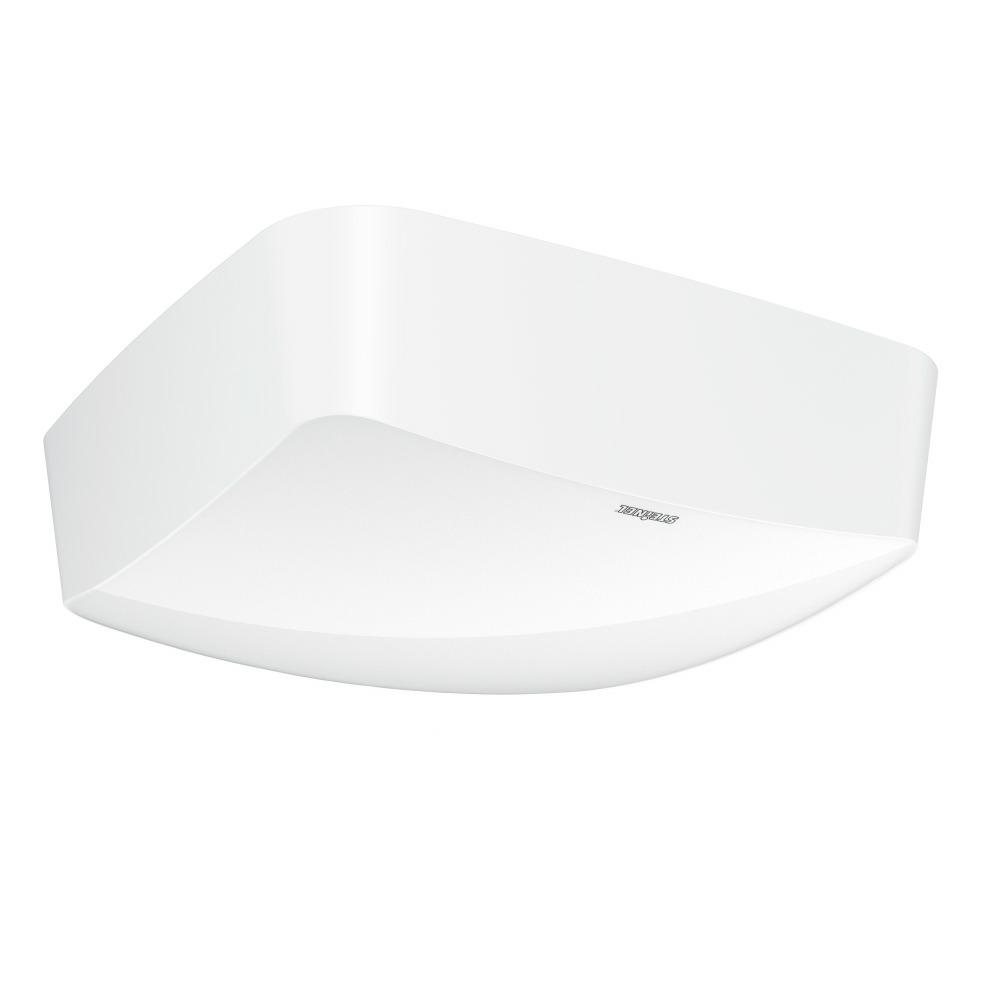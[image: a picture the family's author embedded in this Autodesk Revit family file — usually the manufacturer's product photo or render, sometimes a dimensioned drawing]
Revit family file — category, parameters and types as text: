
# Revit family: truepresence_057930
name_source: partatom
category: Electrical Fixtures
revit_build: Autodesk Revit 2016 (Build: 20151007_0715(x64)
units: mm (PartAtom-declared; Revit-internal decimal feet)

## family parameters
Cut with Voids When Loaded = No
Host = Face
Maintain Annotation Orientation = No
Part Type = Normal
Room Calculation Point = No
Round Connector Dimension = Use Diameter
Shared = No

## types (1)
- True Presence
    Apparent Load = 0 VA
    Default Elevation = 1800 mm
    Description = Type: Presence detector; Dimensions (L x W x H): 45 x 123 x 123 mm; Mains power supply: 220 – 240 V / 50 – 60 Hz; Power consumption: 1 W; Sensor Technology: High frequency; Application, place: Indoors; Application, room: classroom, lecture hall, one-person office, open-plan office, high-bay warehouse, production facilities, conference room / meeting room, hotel room, care room, duty room, recreation room, dining hall / staff restaurant, changing room, kitchenette, sports hall, reception / lobby, WC / washroom, warehouse, Indoors; Installation site: ceiling; Installation: Surface wiring; HF-system: 7,2 GHz; Electronic scalability: Yes; Mechanical scalability: No; Mounting height: 2 – 12 m; Optimum mounting height: 2,8 m; Detection angle: 360 °; Angle of aperture: 360 °; Sneak-by guard: Yes; Capability of masking out individual segments: No; Reach, radial: Ø 15 m (177 m²); Reach, tangential: Ø 15 m (177 m²); Reach, presence: Ø 15 m (177 m²); True Presence reach: Ø 9 m (64 m²); Twilight setting TEACH: Yes; Twilight setting: 2 – 1000 lx; Time setting: 30 sec – 30 min; Switching output 1, resistive: 2000 W; Switching output 1, number of LEDs / fluorescent lamps: 8 pcs.; Switching output 1, floating: No; Switching output 2, resistive: 230 W; Switching output 2, floating: Yes; Constant-lighting control: No; Basic light level function: No; Functions: Group parameterisation, Semi-/fully automatic, Lighting scenario, Manual ON / ON-OFF, Neighbouring-group function, Normal / test mode; Settings via: Bluetooth; With remote control: No; Interconnection: Yes; IP-rating: IP54; Material: Plastic; Ambient temperature: -20 – 50 °C; Colour: white; Colour, RAL: 9003; Manufacturer's Warranty: 5 years; Version: COM2 - Surface wiring; PU1, EAN: 4007841057930
    Height = 0 mm  [stored 0 ft]
    Length = 200 mm  [stored 0.656168 ft]
    Manufacturer = Steinel
    ModVariant = No
    Model = 057930
    Number of Poles = 1
    OnlyDefault = No
    Power Factor = 1
    Product Name = True Presence
    Product group = Sensor-switched outdoor light
    ProductGroupID = 3
    RLX_Detail_Level = 1
    RLX_LegendID = 2.1
    RlxData = Q
eAHsfQe8HUd99ZVluchyE3Jvz71fby/Se0/v2pJ7ky33Jhe5gFxw7wgXsKm2Y4xDL6YEQglx
CGA/yR+hGpKQ0PIFEgjhw0ACIeAkOBR958zOmIux8JvH1fPc+45+Om/+87///+zs7rl7dvbO
7s5orVnTwr81vzYFTfNvI2egXIN/rrrrsc5qcpjn0GqtXAisRoT5YxLXrPnBzHmtQy6/9LxL
Ljv36ksuv+zoay6FdcmVyzfaYH2mbrO0dWXrmtby1lDreFjLW1cBl7XON559WlErb5WtupXC
Gmrt2xpD67HtQ3cnZ8K3Zs2/z5zTOvqSiy6+evGll1x99fIrW0MzuIzZV7bObV3QOue3WmNL
ybO2tB5a+sHM9VvHLL/q4hmbmRbMctNniZ7RWt96f4KVn8g/r7ifHvfq93CD/p5/TXtbmohv
7tNqLYb1MuDyubfvfvG9l47vefu3Fvzru3YYd/Zff/GLj2afnTG+7U7rL9hn6wXj9x910fjf
/cWXF/z6vpPGia33fXjB9p/82qPE/e99eP7dd9013BU/4uLR5ohrc/bX37nHDgf907sOXrZ8
T+QNu1y0N+LaROwIO8n+0GafaKPtEfaJ/UHbI+wT+0M/l93lH6Hf5o4w1y5rmP20yxph/+16
mXi2zXa71tHE0H/Lt749XOz6mfnsL9ty6+v8XL7LRZtcd9OOXXfTB2znd7JPXdvZ2Igdd+tC
m8tjH9D2o7S5XNpcBm3G0GaMzXXrO87l2e023rUN6R/vWu449sMwP0d/jG37aexT1swfmXPS
RcZ2+4Xx8I3gM+N3+4V+2mzL2WyrK97YbpvTb9s3frtcY9v+OD956HIN32zuuOsby67+mHW0
fTDbwdmub+QX+0G/zTU22+C60f+TZW95FBjush+1tvmsyzYxbHsGsJ4FbR5hWGfJ7zwxC3Ax
tDewdZbuH+0NbYUlj1obA7MB5hC0GcdyE2uzTps5c4BNgc0saG9ubZaMI5jvYmhvYess2QZB
m0cL2iznAuzPCwDmELQZx3KetVmnzZytgK2BbSxob2ttlttZ0N7e2iy5HII22yZos12C9g7W
ZrmjBe2dLGjvbEGby2ad5S4WtF0fGcN+ELS5jCFgV8DtR9q72TpLt19o727rLF3/abt1pO22
A+09bJ3lnha097KgvbcFbS6bdZY4fBvQHgJYMob9IGhzGTMA/tvXgvZ+FrTJMdZZ7m9B+wAL
2uQV6ywPtKBNHrHOktyizbJtQZv8Y53lQbYkn2gTtCML2uQY6yxjC9qJBW3yinWWqQVt8oJ1
luQDbZaZBW1yg3WWuS3JCdoE7cKCNnnCOssSGALWByoL2jOtzbK2oM1tzzpLbn/mzAeGLGjv
Y0F7AcB9z308bEGbB1eCNuNps2Q8uUtOjVrQJpdYZ7nQgjbbZp0l22fMGMA2CNpcT4I215fr
zrJjQXvM2izdctmui6HN9llnyf7SZnmwBW32n3WWjp+03Tak7bYzbW4jxpGvrh3ah9g6S9cH
2otsnaXbp7S5nwnajhu0HZdoO77Rdjyk7bhKm8tgnaXjM21+j1hn6b4LtPn9IGjz+8S+02bO
oUD3v3/7s00+8bmfl6se+upNqxdd+z8Ldt56ZNUOr79p9VMfeenw3J0OW7Vq3k2r/+eQOeNv
uuKX4y/9f7es/tQNOz3y8K/+a/zUPW9dfdnNxz6y+j+b3GTuWz7xk8tXrJq71Q2rb375Lz9x
1ufHxhf+5UtWZ2OnDx95zNxVXzjtltUPrL7/0b964lDT5q9+XnKXtrjcf5g7Mjr3odYwl3vk
dw8d/fsnXjfM5R5/wi9GHp43zyz32Nn/zV3Z4nJ/9bNydNt793+EuX91xQrTDpf7kZ+OmRgu
98QT544m+588zOXaNh81bba2XfDRs84Z/eBXb1j9YGfm8JP37Tc6/MKbV8/b9ouPXvqmjUbf
8/ZbVi8ptljwpQ9/e2T+1beu/t77Tl3w3evHRtjm1z7ywCPpm+8c+dBVL1l97PH/teCcGUOj
e/7fm1f/6sh3P9L+s6adt879+Px3XL5ilP35m932qS/+dOO/5exzVj152foLuNwf3rPfqlP/
ZdYwl/v3P91o1WNbjD/K5X7+4W+Pjzzyg/lc7ifHxsZ/+L3bFnC5qw6/c/zRj33lES73a7OG
Vv38nB8s4HL3/cB+q9I5H32E7YxfsWLVseufWnO5p356v1Wf3+29Nf1/fN/+j3x2zUtWc9vd
uMfi0TX5Tcb+5KcPG+X2oP8f680Wxt9YauwP3bR04Xmf28zYm/7sxoUfvvDIVYxB7ELkGLtl
hlX0YoST37SQ7dK2McZGewvZLv1obyHbpY32RtkubdsHY7Pu2mVfkLuaHvYFucZmX5BrbPbF
9Z+l6xvXD/1x/TSxbIftsU+02R77RJvtsU+0bTvGtu2bGLbH9WTMb/6tXDgDlfWAmcD6wCyA
vg0A6hY1jb6NgdnAJgC1hxrFc6LNAfq2AKgr1Bz6XgBQW3is3BrgsZbnCtsB2wM7ADsC/Hyn
Z8HO8BG7AEPArsBuwO7AHoA7RvNzHuufCacV7ljpSncc4TGFcMcZHnt4HHLHLFfyeMbjmzve
uWMgj4nueM/jvAOPwe6Y7HSKPnds547pBnfImEUHJY/V9PE4x+Pm4ucJ52G5nwfceOXdb/yU
OS498Ys/GZn95q8Pt0/+ysjhr/jc/Hn3/svI6KzHFtx105+OrN5/vZGHjtjXfP6l/3vEMD/f
COMENGPaYVurEMO4CDnMc5+x5HhhI7S93v4bjnz2zSeMskTOKP1LWytGv4w2R++9aJR5jHvg
3x8cGcMy2Bfms49s/2705foNjhllyfit0Ee2x3gul/UlF84cXXj5D0eu/qNtTfnovU+N0M/6
Ja0PjTx04jYmf83oIaa+2YHJKPvPOvO+8LNlpnz51qfB/6OR5vMfjbzukE1M/d4//8kI+8uS
68H22e9sy62b9cIy6OdyuD3oZ/8uhp8ltyf7z+3LfnGZ9LM9V3K9uWyuN0v2jyW3F33H3thc
E2DJOv2MMdsZNv3cP6y/7ZQjTcn9dvEHv7yA24l+lqfWDy9gP1hnybpZNuKuOvQrxs/tzM9Z
8nNuH7bz439bZvzcTlweS8Zxe7HOknVuN9ZZss79w3xuN7bHkv72ZTPN525d3bpH57xlJAbY
n1uv/uHILcDVsOm//IKdjX98/mfn0/9erOtl8NHPknncDtx23A7MX4lY5rNkPP3MJ894fFzP
gjaPnay7Y6g7jroYHj95PGWdpfvnjrGsu2OtO84yh+Axl3Hu2Eub4DGXOc88FrvjMI/B7njM
WObzeE3Q5vGZNku2QbhjNm137GZ/ePxmDkGbcd3Hc9Z5TGeOO667YzqP8TyOs+6O5zxm0x4C
aLPc1YI22yZoUzMI2rtZmyV1gKBNPSBo72lBm8tmneVeFrRdHxnDfhC0hwDqCLXD6QXt/QDu
0/0B7pMDAPqoHbRZsv/cVk5HuF70c72pJfRTS1jv1hPaTlNoU1cI2lw2bZbUGoK26yNj2A+C
NpdHHerWINokLUGbB1zaLIctaI9Y0B61NktqEUF7DOgABwOHWJvlIgvaXD7rLKmD67o/i7GM
Q4HDANosD7egfYS1WR5p60dZm3XaR1vQPsbaLI8FjgOOB5YAvuvOnBMAtkHQZrsEbbbPfk22
P77rPpH+nIj+LAVOsqB9srVZuvOiU6yPcbTJYdosyVnaLE+1oE3+ss5yhgXt0yxo83tG0D4d
YBz/uXZon2HrLLkcgvaZ1mbJ9SBon2VB+2wL2ttb0D7HgvZWFrR5LCRocxm0WW5qQXsja7Nc
ZkF7Ewva5wL8R5s5/OfWjd/LFsYjrK9nbPfZSn71nvbx2OPiZsJiPLc9fcxzvqaNlQtZ57Zk
ndvIxTkfP6ePdbbNOo8lLs75+Dl9rFN7WOexzsU5n+sfP6HPxTOO9Q2tn9uFPv51Ppb0seQ2
YsljkotzPh676OPyZwP0zwPo4/Kcz/WPPtqMOwBgHPvCONcGfayzXyypnS7O+Vyf2S/ahFkB
5JIT5APLRQBzWd8McJ/RR9v5toTt4rg8xh9MF+IY43y06ePy6GN9DHA+1l08fey/q/NcwPlo
E+Q2fYxxPtcX9o8+1ucCjOuub2N9jHMx1H7GddePsD7GsR3GHGp93Oasc59RC13/nM/1j8ul
j/WtAca5GNZ3tj7GsS36XP/YF/pYPwpgrmtnW9T2tD6XQx/HpS6OefQtA+hjnIvZy/pcDPN4
HGGci2F9B+tjnItpWx/jXMze1udimLej9XFbMY51t63oYyx9BwJcLrcL4xjjtgvXnz7WdwEY
55bJulsu47hM+oYAxrk+sL4rXfAxjsscAo4GXByXyZjd6EKc6yt9x1of22M/GLO79bm+0ne8
9XE7M5YxbjvTx1z69gC4DPrYX9bdvnTrSR+1lXHc54xjzIUAfdz2XAbbd9tgCDb7uw+QA4xb
H3+db98u3xBsxi21PrfujCmsj7lcL/r2sz4eh+hjfX/rc9uD9dL6GMd1pe8A6+M+p491t8/J
AfpYd7wi1+hj/SCA68E6twnrbhmMc74INuNY53ZiPQboY5zznWt9jOO2Y0xifYxxvvOtj3Hc
voxJrc9tc/rOtD5uP8Yyxm0/+phLXwawL/Rxu7Pu9hFjnO9s2Iwbwl+3H0+nCz5uZy6D7btt
ANPsnwplzQriZuAv9xl9pwL08S/3GWPmswKf26/0XW19G6FkHGMWdPm4H1kftj63/+m70/qY
y33LmBHrc/ufvjusb0OUjGPMaJePHGDddBb9czyhz+VuAptxjBkDuB7UE/rGgA7gfOQP6wfT
hTjHMfput75NUTKOMYd0+cgz1hdZn+MifbdZ3xyUjGPM4i4fucf6odbHGOdbaX1zrY8xh3X5
yEfWD7c+x2P6brU+5pJ7jDnC+hyP6bvF+rZEyTjGHNnlIx9ZP8r6GON8N1vfPOtjzNHWt6P1
sX5Ml49cZv1Y63N8p+8m6+NxknGMOa7Lx+8A68dbH2Oc70br29n6GLOky8fvAesnWB/znO8G
6+Nxkz7GnNjl4/eH9Yusz32n6LvY+tZHye/QUuAk6xtC6XynWd9M62PMyV0+fq9YP8X6mOd8
V1ofv6v0McZ9V/m9pI/1FwPkLnP5nTwNuAqgbwh/ne90uuDbx/pYP4Mu+BjD7ynrLpdxzncO
bMbtjb/8np4JnAXQx2Od811gfYzjd5cxZ1sfY5zvUuvjMuhjjFsGl0kf65cDXMY2+DsKLAPO
BejbCn+db7n17Wl9jDmvy7fQ1s+3PuY534usj+tBH2PcerDP9LG+AuBymTsGcJkvBFxfxmDR
dyFA3y74Owaw7jhETtHH+iUA4+jj8Yaccj5yzfmuh824MfyljzFuuewLfay79WB/6WPd9Znr
QR/rbttzG9PH+mUAl0HfwQDrbtszxvmuhc047iP6GHMFQB85ST/rjpP0MY6+qwHGkbeMY4zj
OLlLH+uOf/vBZi7zrgGYS98hAOt3AvQxxvlc/9hn+li/DmAc64sA1l8C0Mc453PbmduePtZv
ABiX4y99rN8I0MfjEH2s3wTQl+IvfazfDNCX4C99rN8C0BfjL32s3wrQF+Evfay7/tHHfrO+
EmDcQfhL30rgpQB9++Mvfay77UIfY+m7DXBxbVu/vct3IGzW77C+Gb/41q++tXrNP635FeZu
HrT4683fd/3y6z875/GXjKx516NPfeucx9+45lf37tYZ2qk1dMTc9X9gx6amgdZpP7577LQf
b8zN27qrceGv18zFp7PWbvi3t2NXYzNgE2v/twE++uLBCYJmrZyxGWZ1YrLqGHzc8/y3UVOY
v2HN4zwFX2QeJ/4G+Mz5Lxp/90ELR45e9o0F977/tHFg5BflI0/b/K0Bn48jzsT82zYLx996
6YvMbxDXrdpl/Jd/8uKR3S98YoGzGY/PxxFnYvD5OD4zMc5mjLXHmUubm8nZbMvF0N/Vh/Gu
fo539dPE23UxMbYPxm/7bGzbT7NcZ7N99pH9YB8459LZzs8Y9oX+Ltusl/WPdLVj/DbX+Lk9
3Hbj9nbbk9ubYK6zuV783O0X5nVtzxG2a7eVsZmLfmGvPr0Nje38iDfrxRja9Ns2jW2X5bYt
+2P8tj9mO9s+mxi7LiaGy+Q/trlJftE4MDLrVV9esN1+l2JO6tEj2ap/XvBn4zeOj1111Mjf
nvfUgnd8Y+U4t++TX585bP3j9Nv4ccbbdsbZDuOf+MW+44y39ghttDfOfOa+7/KjRjqrbxz/
n+VPUSZajGMM85zNfrFdtgn/iPOjjRHXNxtj+o/PRxhnlzvi+mz9pn2ba/qAdR3HOpj1tX0z
62v7Y9qx/XE2+2BsLp9tcV24zVw7j6evMev+70uqkf/8h7vHT/n0SeO0R7974zhBmz5+Rpvt
M4f25XNnvtPZXA9nI960ZdsxbdFGG6Yt2og1bTmb6+BstmVt9u1p28XYvhm/7bOxbT+Nbfvp
bLM8tsk2uGzaaMeAtu2z8dt+Gvu8N4w/CgwzxtqPWnuY9S7bxLB9HtPXs6A909os17egPcva
LHmkZ86GgPtHm0d4gvbGwGxgE2COBe1NLWgzlnWWjN8M2BzYwoL2ltZmOdeCNttmnSXbZ84L
ALZB0J5nQZvnv1sD2wDbWtDezoI241lnyXiu6/YA15egvYMFbeoj6yx3sqC9swXtXazNcsiC
9q7WZrmbtVnubkF7D2uz3NPW97I267T3tqC9j7VZ8lySoM3zQII2z3NoszzAgjbPaVhn2bY2
S54TEbS5/Wiz5DbkfuZ24b4jaPMcjDZLt69pOw7Q5rZlnSX3Ddshn5hP0Cb3aHP7Moegze1M
myW3AUHbbTfaQxa0uS8Yw+3k2qHNbcM6S8cH2m59abvtQ5vbjHHkh2uHtluHLWC7daRNbs4A
+I/nrwT/8fyWNsvUgvZG1mbJ7wb/0XZx9PFMiqA929oscwvaPB9nnWVpQXtzC9r8/hC0XX4F
27Vfw2bfmMPvkmuH9nwL2vyesM6S35+tgQXWZp32sK2zHAEYQy7xM4L2qAVt8o/+hYDL4TLY
3l4AvwtjFrT5PWGdZceCNr9XBwOHAGMWtNkGy0XWZp32Yltnye8JQZvfDYI2+0mbJfs5EzgU
mGVB+zBrszzcgvYRAOPJCcYRtMkF2iwZdyRwFOByafNYwzpLLovreTTAzwjaPNbQZsk4rj+P
M4wlaDOOJWNoHwNwvx9rQZvcYZ3lcRa0yQHWWXJ/0GZ5vAVt7l/WWS6xJfchbYL2CRa0uY9Z
Z3miLbnvaRO0l1rQ5nZnneVJFrS5b1hnebIFbe5X1lmeYkvue9oE7VMtaJMvrLM8DeD3IANO
t6B9hgVtbi/WWXJbcv9xP55pQZvfI9ZZnmVBm22zzpLtM+ZsgG0QtMkZgvY5ALlBHiyzoH2u
BW3Gss6S8WMA9/15FrTJEdZZnm9Bm22zznIZwJgLgDEL2gdb0Ob2Yf/Z9+UWtLk9WGd5oQVt
bh/WWTq+kUMuhja5wzpLxxnyw8XQvsjWWbrl0r7Y1lm6bUJ7mQVtt760uX4Eba4PQZvrRdB2
3KDNZbDO0vGHtuMbbcdJ2uQpQZtcJmhzHdg/7h/Xf9rcx6yzdPzh9qWP26P7X/c85u75zXbO
8WrGds+Hnshc5+55zN3zmzFvmHOjR9lm93zoicx17p6fbeccm751z3XungPdPTd6IvOeu+c0
d8917p4D3T03egLznle/840XrEq2vLv+2d03/Na88/bXrl1130lnLdjpqutXb/nNa1fNfMFh
82l/4ZobVn3mqYvm33XE0/5P0P+iBy9Y9anLt1/Adp54z62rPvV3983f8r+uW51uufHH349l
0P/Sxa/8xBfe/eJV//Op61c/+MarPvGDb1y7irk/um+zR95/1Q2r2OZrd8seGX19E/+5f9rg
kaXvvnUV2zn3m9eafcL4Fe95sbHZzntff8HoQ7h/gO3f895bjZ/x5bU3GJttvvmdLx5djRjG
f/CNFxg/47vn9//3yf80/6v/eO0o2//2U0/UOyKfud/8u7nzl6PdrnUZZe5HW7svmPPgBca2
62JyD97p1QuO/vumnffffN3q/RYsWvVflxy4ataXlqzedWjOatqv+eCc1W+/Yomx7/3Goat2
PuM6Y1+/ZOiRHx108+qDNotWvfL0Q0Y/8/LGf/tPNln4hf9o4o/68JKFrz+uaedVL75u4W47
LDbtD0U3LyRnmbtLhDbmPlzTbmGZO3xpyUIu95VY5oc+OMfYW2OZ7W8eOmr6M3/Rqj+/+Trj
P2huVrMt5t65+QkL//mxTYx/r5fMWXjFPU07H/jF4tFTLmziv3rfdQu/c8PBph0uv/n3mzk8
68ExE1gfmAHMAjYANnwGNkJ9Y4vZKDcB6JsDbAps9gxsjno3tkB9S2CuxQtQEvOArQCeh3Vj
G9S3Bbaz2B4lsQOwI7DTOsbOaH8XYAjY1YL13bpA/+7AHoCL3xM2sRewt8U+KIl9LZx/P9T3
tzgA5YEWbZQHAZEFbX5O/SYSIAWo+TlQACVA3a9tnX5iPsA4gjHMIxZYDKMkRiz45SNI1m6M
oU50LA5GSRxisQhlNxaj3o1DUT/M4nCUBH08NyCo893gOQDPCQlqNEFft1Yfh/pU461YZj4D
++aqTwyfetXK+W+68k5uvhbLNw69cLje5BcjrqR/3hd+NMK4Bx/7kfE/vtU/j9z80w/PZ8m4
oTd/wuQdf9ZTw/SzpP+1xWtMHEvWT75tz1G2c8h3dubuabGk//6X72nKX5x54CjzWdJfDN9i
6g8efZIpWaefdZaf+eadT5dsb/xVt5n2d37Fbcb/kSdnjLLP7Ofet88c/eydM0dftcU/j7A/
S+LXjLDuypMPf2qYca//zn7DzPn2zw4x24HbgnW2xTy2w/Vjec+c/YfZHmMZw+3HeG4PxvNz
ts+S7TOP7fNz5pjtjRzau8DH9vm52f7wsw36uZ3o++trth/lvoheusPoh7/XGr1mve1H//L1
T4781Vu2Hv3pf/xsZLvvbGvWjyWXu/O/zDMl61w+4z7+rbcPM+99+791eKfPzzL1Fy1fz9TZ
5npfWTrM9lma/YN+cLltcIXtXfPX3zXl4oP+dYR9+fudFg1z2e0PbDD88JNvH2bJ9fj4u766
4PbsX01JnjGuhTbZ7orvfHeYn0eIZe6X8Bnb4ufsw2P4jO2z5Hqw5HIZz/4znv0hn17w0xmj
y7fbbZTrQN5wvzxx+W6jXDfy5JMv23D0rX+9nynv+8JLTPnkVnc8/bnZn69+udme31t4h2mH
PKOf/OJ2J6+4HLbz6h8PjbD84Ue2XXDMN3YxdS5vxcZPzT/0/q1Nndvvtb/szH/Dl2eZOteJ
da4r4/ba7qkRtsPtw3ZYss7txjpL1rmdWGfJOrcv87993KtNnduL7V4xawNT5/oxnuvNknXm
sc7yUzNfYcrjsb7M43Zgez89+07j/xi2Lev3zZoz+v0XPDXyk3SzUe6HB94wPvI6gHXuj6Y+
YurcL4x/Yv6rh7m+F6MvXL/rX7+JWS9+L7k+LB94wwjaGUE+y3GzvmyT68eS68W2uD5/jLZW
og32g7nsB0sunyWXy8+5XMZzucznctkeY7hd2S77w3bZP7bLz3D4a60HuPOGWdZmyXMHgjbP
IWiz3AhgDs8h3D/aPJcgaPOcgrFzAMYTtHl+QdBmLG2WjOd5x+YAzy98++POSdy5S/f5Ce1n
Oz/huQrPTQjaPJ+hzZLxvv3nOrj1d9sDrqe3E7cZwX/c7u6ciOdCtN05Ec+LaPN8ijZLnk+x
ZD/dudVz9Z/rwHXh+rvtwe1DmyW3GeG2u29/dkTuTsDOFrR5XsU6yyEL2rta0N7N2ix5zsV2
eN7FfIL2ntbeCyVzCNp7W5vlPha097WgvZ8F7f0Bxh0AuHZoH2jrLNsWtHl+RtCOLGjHAON4
vubaoe3Wgedhbh1p8xwtB9z5HM/XaPO8jjZLnt8RtHluR5slz+cYS9vF0ccvM0F7xNos+UUm
aC8ExoAOcDDAczr63Pkc7cUWtF3+obBd+4fBZl+4HocDbIegfYQF7d2szZLbgtvnSGuzTvso
W2d5NMCYYwB+RtA+1oI2tzn9PBd0OVwm2+N+47483oL2EmuzPMGC9n7AicBSwMXTZhssT7I2
67RPtnWW3N8E7VMsaLOfrLNkP08FTgNOt6B9hrVZnmlB+yyA8eQE4wja5AJtlow7GzgHcLm0
l9k6Sy7rXOA8gJ8RtM+3NstlwAXAcoCxBG3GsWQM7QuBi4CLLWhfYm2WL7Sg/SJgBXApcJm1
WV5uQfsKa7N8sa1faW3WaV9lQftqa7O8xtavtTbrtK+zoH29tVneAKzr/tyIZdwE3GxB+xYL
2txerLPktnTbidvtVuAlwEprs3ypBW22zTpLts8c7ge2QdBmuwRttu/bn9uQ47aVb3+4fbnt
2QZBm/uJoM39cztwB3CnBe2XWZvlyy1o32VtlndbvML6GEf7lbbO8lUWr7Y+xtB+ja2zdMul
/VpbZ3mPBe17LWjfZ0H7jyxo329B+3UWtB+woM1lsM7y9Ra0H7Sg/ccWtN9gQfuNFrS5Duzf
mwDXf9pvtnWWb7Hg9mUM/81oCnMMBqsmdd8W9x1z18PfmQDbpE0f6+sD7jMX53wlw2zcLFiM
5/ecPsY4H236WN8AYH1bwMU5n2uPy9sQYHwBMI5/nY/x9LG+EcA6bRfnfMdYHz/bGGAZWR9j
nG8T65uNkjY/O876WJ9jfYznMhjnfFtYH+M2BRjDzxnHGOejbtLHthnLmKMB52OcWz59bIc+
xiYAfZvh7+YA2z0VoI919sEty8U535YMs3G02eZSuuBjjPOxbfpYnwu4Zbk45zuMYYhjXxnL
5Z8EOB/jXJ/oY7/o47JcLu0XAMw/FGAcl+d8jKeP9XkA67RdnPOdbn38bCuAZW59jHG+baxv
a5S0+dmZ1sc6uejiuQzGOd9BXXHbwWab/JxxjHG+RdbHdtgmY87o8jHOLZ+5bIc+xi4G6CPf
twfY7g0AfeS28zGePtZ3AFin7eKcr7I+frYjwPJm62OM89FmLus7Ae4z+mg7Xw3bxe0My8XT
xxjnG2GYbW8XWPyMekcfY5yPNn2sDwHuMxfnfK49xu0KsLwFYNwQ/jofbfpY3w0YAi4CXJzz
8XP6WN8dcPEuzvmGGWbj9oDF+OV0wccY56NNH+t7Au4zF+d8Cxhm4/aCxfgL6IKPMc5Hmz7W
9wbcZy7O+UYZZuP2gcX4FXTBxxjno00f6/sC7jMX53wLGWbj9oPl4uljjPMdwjAbtz8sfnYp
XfAxxvlo08f6AYD7zMU5n2uPcQcCLC8HGMcY56NNH+ttgPVzARfnfPycPtb5vXXxLs75DmYY
4vh9ZCxxDuB8jHNt0MfvI31EB6BvA/zdEIiAAnC+jWHRF9Nl41zdfS+7YxIbtylKxrGeWt8c
62M9sz4eNxjH+mLrYxz99OVdPnc8PNT61kPJfrO/pfXxe8722Df3Pef3lj7W5wNcD/rIR9Yd
n1lnHH2Ok4zj94Ax7ntE35Ctj6Bke+Qic5nn+Ec+0cf6GMA4bnv6xwC37eljHH2LAMYxxu2f
g7t85Arrjms8ZjKXed3bbwvUuZ0OA9ge/3IfHg4cwQp8M/DX+a6xPhbcZ4w5hhXEMcb5jrQ+
t19ZP8r6GMd9S9+brW8jlIxljGuPPsbRdzTAZWyCv/SxfizgfOQA68fRhTjGON8p1jfb+hhz
fJeP3GF9ifU5PtF3svUxl/xhzEnWxzznO8H6HMdYP7Erjryj73br2xwlYxmztMvHOPpOtb4t
UTKOMd3LJW9PBl4KcH3ZZ+d7Q5ePXOb6P2h93C7O91br2wwll8tlntblI79ZP936GON8d1jf
POtjzBnWt431sX6+9W2Nkt+NM4FzrI9xzneW9bHO7w/r51kf45zvbOtjnd8p1u+yPsY5n1su
j2dsk8tcBnBb0cfv3zLgXIA+xjjfa6yPx1H6GHO59TGOXxL27VXWx7443yusj9uJfWE/XmZ9
e6AcAy4AlgNc7l74OwbQdwlA3274OwYw5kLA+Tq2fpH1jaF0vvda367Wx5hbrO9glIcAFwMP
WN8YSudzy6WPsYz7IOD6xzjGvJAu9I/1RQDr9wMuzvleZH2s81jD+n3Wx/V1vhXWt4/1sX6p
9e1vfaxfZn3cF8xl/R7rYxz99Ll9NBP2ocAVwNUA+zcLf53vxdbHOo97rF9rfYxzviutj/XD
Adavsj7GOd8N1sc4Hg8Z8w7rY4zzvdv6ZqDkstm3a6wvtj7WXV/oY5usvwngehyJv0cB1wHv
B+jjMpzv+i4fYxn3kPVtj5JxjLm5y8d8+tx6kFM8vt4I3ApwGcxzvpusj3H0M+5PrG9HlIxj
zEu6fIyjzy13F9jMJ0fdMuhjLusut4JNPVgJvBFgX+g7lhbwUoA+xjjfw9bH4zN9jLmty8fj
P+u3Wx9jnO8vrK+0PsbcYX38TjOO9Tu7fNQJ1l9mfYxxvo9aH48F9DHm5V2+JbZ+l/Uxxvn+
0vqGrY8xd3f5qCesv8L6mOd8H7O+hdbHmFd2+agxrL/K+pjnfJ+3vgXWx5hXd/mW2vprrI95
zvc56+N3kj7GvLbLd5Kt32N9jHG+z1rfYutjzL1dvpNt/T7rY57zfcb6FlkfY/6oy3eKrd9v
fcxzvk9bH49r9DHmdV2+U239AetjjPN9yvp43KSPMa/v8lE/Wf+Q9THG+T5pfRnK04EHgT+2
vrrL9zbrY9wZAGPeYH3Mc74/s77K+hjjvjP8fjCO9T8H+J2J8fdM4E3AmwH6eLxxvrdbX2p9
jHlLl+8sW3+r9THP+f7a+rge9DHmbQCXwT7T9zbgwwB9zD0b4DK/CLi+ON87rO8IlPSx/k7r
Y/0cW/+C9THO+d5jfTzOLQMeAt4FcBk8Ri4D6PtTgD7GnQsw5t0Afcvw1/nG6YKPy6CPMW4Z
XCZ9rD8OMK6Dv+cB7wX+BKBvDH+d7wN0wcdjJH2MeR/gfOfb+vutjzHOt9r6uB70McatxzLr
Y30VwPaYewHAZT4GuL443wet72CU9LHuuHua9bH+fwDmcl8uB7gfHf+4b53P8YDco48xHwGY
S9+FAOuOk4xxvk/AZtwx1seYh+mC71j8ZRzrfwHQdxz+0sf6RwH6jsdf+lj/S4C+JfhLH+sf
A+g7AX/pY/3jgPNdZOuftz7GOJ/rH/tMH+uPAMxl/WKA9b8C6GOc8z1qfeQKfaw7XtHHWPoc
h5bBZhxj3L7k/qaPdccD7l/6WH8M4HK5H+l7DHD7jfuSPtY/CTDuVPylj3XXZ/q4Lqx/CmDc
KfhLH+ufBug7GX/pY/0zAH08PtPH+mcB+pbiL32sfw6g70T8pY91t535PeI24Pq77zS/5/Sx
7o4RZ1of645rM3APeHMz+NP3hq+/8ae3PPywoZ0+/R9PnPTrNWs+tObjv17z1H/8+n9x8/SX
n7jumpG/fdeZf/uzMx9/16M3nH3W42984qtbPnT4jNZ9e3Tuu+Ahc4kUrZt/d6+4dGzFZd8b
Y+Uu4+Ef/1u+n059VsO/vZ2etZ21OTfAB80t5E2E//LW1vJk2tsCSWvWfH/mpq0Tb7j0vMtX
LLry3Osuueyiax+PZzTNrVz4wj2PGn38jOWjZMssEzzbBh967vnLZzJsDa9L8W7Tf7ii+SKd
dMc7hrvtLR6fu4CB3X7e9eliaBOMYTvOZn32Si4Di8BvJPzM5aBf4/scdKb54q78zM8e3XfD
O4190h27Pco45sIedjZihl0MckdcLpfl2mROszwucFaL7X73q58fpp/22bvvafp43czbfste
cddlxs8YZ/92W+ux2nJt0X72uA1baHvYxdF2y2T/1+bvjnHtMtfZXJ77N9sZplyz5kcz128d
cvTJR3GH83kG3f826qrc+V9vGCO6XNgo8SLWedftpU/8wgDXusZcnZ9dPIOawKtbxLIOfZZc
NCfwr7kK9ptAttMaw39gJfA24DHg2wAHNlsAQ0AEjAHHA1zuFcBK4C7gHuBB4G3Ae4EPAx8D
HgM+B3wJ+Afg28D3gZ8APwc4SF8f2AiYA2wBzAO2BXYEhoA9gH2AA4AIyIAKGAbGgEXA4cDR
wPHAUuBU4ExgGXABcDGwArgCuBq4HrgZWAncBtwBvAy4C3gF8CrgNcA9wH3A/cADwIPAG4A3
AW8B3ga8A3gIeDfwXuB9wJ8CHwQ+DHwEeBj4KPAx4BPAo8Aq4DHgk8CngM8AnwMeB74I/A3w
JeDvga8AXwP+AfhH4JvAPwPfBr4DfBf4HvB94IfAvwM/Bn4C/BR4Evhv4OfA/wK/BH4N8MLJ
DGA9YCawPjAL2ADYENgI2BiYDWwCzAE2BTYDNge2ALYE5gIvAOYBWwFbA9sA2wLbAdsDOwA7
AjsBOwO7AEPArsBuwO7AHsCewF7A3sA+wL7AfsD+wAHAgUAbOAiIgBhIgBTIgBwogBKogBqY
DywAhoERYBTgxZ8xoAMcDBwCLAIWA4cChwGHA0cARwJHAUcDxwDHAscBxwNLgBOAE4GlwEnA
ycApwKnAacDpwBnAmcBZwNnAOcAy4FzgPOB84AJgOXAhcBFwMXAJ8ELgRcAK4FLgMuBy4Arg
xcCVwFXA1cA1wLXAdcD1wA3AjcBNwM3ALcCtwEuAlYe0VgKtl6IEWrehBFq3owRad6AEWnei
BFovQwm0Xo4SaN2FEmjdjRJovQIl0HolSqD1KpRA69UogdZrUAKt16IEWvegBFr3ogRa96EE
Wn+EEmjdjxJovQ4l0HoAJdB6PUqg9SBKoPXHKIHWG1ACrTeiBFpvQgm03owSaL0FJdB6K0qg
9TaUQOvtKIHWO1ACrXeiBFoPoQRa70IJtN6NEmi9ByXQei9KoPUnKIHW+1ACrfejBFp/ihJo
fQAl0PogSqD1IZRA68MogdafoQRaH0EJtP4cJWD+6fis4/N64MJMYH1gFrABsCGwEbAxMBvY
BJgDbApsBmwObAFsCcwFXgDMA7YCtga2AbYFtgO2B3YAdgR2AnYGdgGGgF2B3YDdgT2APYG9
gL2BfYB9gf2A/YEDgAOBNnAQEAExkAApkAGLOu/acFHngZ0Xdb65aFHnZTcu6rxv9aLOefMW
d750/eLOjj9a3LnqxYd25mxwWGfX9x/W+e9lh3e+tvcRnbmtIzuzfnhkZ8vvHdV5+5NHd/bf
+tjOgUcd1zno/uM7n/7PJZ3XXnBip/rR0s71rzq5s80hp3Z+uOXpna8/dUbna784C+cZy34L
85ee2akfPLnzYLGk8729j+6sXH5Y5/ofHNy5+YOjnb/60PzOL79fdMZOTjsbPXlQZ6fVB3Tu
f3jfzqf+bq/O6Lw9Op+7YdfOqa1dOpu/e8dOdsn2nfjwbTuv7Wzd+e8T53X2unVu5+ertuic
sdXmnSUrN+385NebdM68Z3bni+nGndu/v2Hnyx/YoLPt7bM6j1y0fic+Y2bnyTPX67x6xYzO
K+5udWZetGZsz6/8auzTp/1ybPh//nfsx+9/auyY634+1hwD9DfsLSBOi9NhM9S/d+K0OO3P
mrAzxGlxOmyG+vdOnBan/VkTdoY4LU6HzVD/3onT4rQ/a8LOEKfF6bAZ6t87cVqc9mdN2Bni
tDgdNkP9eydOi9P+rAk7Q5wWp8NmqH/vxGlx2p81YWeI0+J02Az17504LU77sybsDHFanA6b
of69E6fFaX/WhJ0hTovTYTPUv3fitDjtz5qwM8RpcTpshvr3TpwWp/1ZE3aGOC1Oh81Q/96J
0+K0P2vCzhCnxemwGerfO3FanPZnTdgZ4rQ4HTZD/XsnTovT/qwJO0OcFqfDZqh/78Rpcdqf
NWFniNPidNgM9e+dOC1O+7Mm7AxxWpwOm6H+vROnxWl/1oSdIU6L02Ez1L934rQ47c+asDPE
aXE6bIb6906cFqf9WRN2hjgtTofNUP/eidPitD9rws4Qp8XpsBnq3ztxWpz2Z03YGeK0OB02
Q/17J06L0/6sCTtDnBanw2aof+/EaXHanzVhZ4jT4nTYDPXvnTgtTvuzJuwMcVqcDpuh/r0T
p8Vpf9aEnSFOi9NhM9S/d+K0OO3PmrAzxGlxOmyG+vdOnBan/VkTdoY4LU6HzVD/3onT4rQ/
a8LOEKfF6bAZ6t87cVqc9mdN2BnitDgdNkP9eydOi9P+rAk7Q5wWp8NmqH/vxGlx2p81YWeI
0+J02Az17504LU77sybsDHFanA6bof69E6fFaX/WhJ0hTovTYTPUv3fitDjtz5qwM8RpcTps
hvr3TpwWp/1ZE3aGOC1Oh81Q/96J0+K0P2vCzhCnxemwGerfO3FanPZnTdgZ4rQ4HTZD/Xsn
TovT/qwJO0OcFqfDZqh/78RpcdqfNWFniNPidNgM9e+dOC1O+7Mm7AxxWpwOm6H+vROnxWl/
1oSdIU6L02Ez1L934rQ47c+asDPEaXE6bIb6906cFqf9WRN2hjgtTofNUP/eidPitD9rws4Q
p8XpsBnq3ztxWpz2Z03YGeK0OB02Q/17J06L0/6sCTtDnBanw2aof+/EaXHanzVhZ4jT4nTY
DPXvnTgtTvuzJuwMcVqcDpuh/r0Tp8Vpf9aEnSFOi9NhM9S/d+K0OO3PmrAzxGlxOmyG+vdO
nBan/VkTdoY4LU6HzVD/3onT4rQ/a8LOEKfF6bAZ6t87cVqc9mdN2BnitDgdNkP9eydOi9P+
rAk7Q5wWp8NmqH/vxGlx2p81YWeI0+J02Az17504LU77sybsDHFanA6bof69E6fFaX/WhJ0h
TovTYTPUv3fitDjtz5qwM8RpcTpshvr3TpwWp/1ZE3aGOC1Oh81Q/96J0+K0P2vCzhCnxemw
GerfO3FanPZnTdgZ4rQ4HTZD/XsnTovT/qwJO0OcFqfDZqh/78RpcdqfNWFniNPidNgM9e+d
OC1O+7Mm7AxxWpwOm6H+vROnxWl/1oSdIU6L02Ez1L934rQ47c+asDPEaXE6bIb6906cFqf9
WRN2hjgtTofNUP/eidPitD9rws4Qp8XpsBnq3ztxWpz2Z03YGeK0OB02Q/17J06L0/6sCTtD
nBanw2aof+/EaXHanzVhZ4jT4nTYDPXvnTgtTvuzJuwMcVqcDpuh/r0Tp8Vpf9aEnSFOi9Nh
M9S/d+K0OO3PmrAzxGlxOmyG+vdOnBan/VkTdoY4LU6HzVD/3onT4rQ/a8LOEKfF6bAZ6t87
cVqc9mdN2BnitDgdNkP9eydOi9P+rAk7Q5wWp8NmqH/vxGlx2p81YWeI0+J02Az17504LU77
sybsDHFanA6bof69E6fFaX/WhJ0hTovTYTPUv3fitDjtz5qwM8RpcTpshvr3TpwWp/1ZE3aG
OC1Oh81Q/96J0+K0P2vCzhCnxemwGerfO3FanPZnTdgZ4rQ4HTZD/XsnTovT/qwJO0OcFqfD
Zqh/78RpcdqfNWFniNPidNgM9e+dOC1O+7Mm7AxxWpwOm6H+vROnxWl/1oSdIU6L02Ez1L93
4rQ47c+asDPEaXE6bIb6906cFqf9WRN2hjgtTofNUP/eidPitD9rws4Qp8XpsBnq3ztxWpz2
Z03YGeK0OB02Q/17J06L0/6sCTtDnBanw2aof+/EaXHanzVhZ4jT4nTYDPXvnTgtTvuzJuwM
cVqcDpuh/r0Tp8Vpf9aEnSFOi9NhM9S/d+K0OO3PmrAzxGlxOmyG+vdOnBan/VkTdoY4LU6H
zVD/3onT4rQ/a8LOEKfF6bAZ6t87cVqc9mdN2BnitDgdNkP9eydOi9P+rAk7Q5wWp8NmqH/v
xGlx2p81YWeI0+J02Az17504LU77sybsDHFanA6bof69E6fFaX/WhJ0hTovTYTPUv3fitDjt
z5qwM8RpcTpshvr3TpwWp/1ZE3aGOC1Oh81Q/96J0+K0P2vCzhCnxemwGerfO3FanPZnTdgZ
4rQ4HTZD/XsnTovT/qwJO0OcFqfDZqh/78RpcdqfNWFniNPidNgM9e+dOC1O+7Mm7AxxWpwO
m6H+vROnxWl/1oSdIU6L02Ez1L934rQ47c+asDPEaXE6bIb6906cFqf9WRN2hjgtTofNUP/e
idPitD9rws4Qp8XpsBnq3ztxWpz2Z03YGeK0OB02Q/17J06L0/6sCTtDnBanw2aof+/EaXHa
nzVhZ4jT4nTYDPXvnTgtTvuzJuwMcVqcDpuh/r0Tp8Vpf9aEnSFOi9NhM9S/d+K0OO3PmrAz
xGlxOmyG+vdOnBan/VkTdoY4LU6HzVD/3onT4rQ/a8LOEKfF6bAZ6t87cVqc9mdN2BnitDgd
NkP9eydOi9P+rAk7Q5wWp8NmqH/vxGlx2p81YWeI0+J02Az17504LU77sybsDHFanA6bof69
E6fFaX/WhJ0hTovTYTPUv3fitDjtz5qwM8RpcTpshvr3TpwWp/1ZE3aGOC1Oh81Q/96J0+K0
P2vCzhCnxemwGerfO3FanPZnTdgZ4rQ4HTZD/XsnTovT/qwJO0OcFqfDZqh/78RpcdqfNWFn
iNPidNgM9e+dOC1O+7Mm7AxxWpwOm6H+vROnxWl/1oSdIU6L02Ez1L934rQ47c+asDPEaXE6
bIb6906cFqf9WRN2hjgtTofNUP/eidPitD9rws4Qp8XpsBnq3ztxWpz2Z03YGeK0OB02Q/17
J06L0/6sCTtDnBanw2aof+/EaXHanzVhZ4jT4nTYDPXvnTgtTvuzJuwMcVqcDpuh/r0Tp8Vp
f9aEnSFOi9NhM9S/d+K0OO3PmrAzxGlxOmyG+vdOnBan/VkTdoY4LU6HzVD/3onT4rQ/a8LO
EKfF6bAZ6t87cVqc9mdN2BnitDgdNkP9eydOi9P+rAk7Q5wWp8NmqH/vxGlx2p81YWeI0+J0
2Az17504LU77sybsDHFanA6bof69E6fFaX/WhJ0hTovTYTPUv3fitDjtz5qwM8RpcTpshvr3
TpwWp/1ZE3aGOC1Oh81Q/96J0+K0P2vCzhCnxemwGerfO3FanPZnTdgZ4rQ4HTZD/XsnTovT
/qwJO0OcFqfDZqh/78RpcdqfNWFniNPidNgM9e+dOC1O+7Mm7AxxWpwOm6H+vROnxWl/1oSd
IU6L02Ez1L934rQ47c+asDPEaXE6bIb6906cFqf9WRN2hjgtTofNUP/eidPitD9rws4Qp8Xp
sBnq3ztxWpz2Z03YGeK0OB02Q/17J06L0/6sCTtDnBanw2aof+/EaXHanzVhZ4jT4nTYDPXv
nTgtTvuzJuwMcVqcDpuh/r0Tp8Vpf9aEnSFOi9NhM9S/d+K0OO3PmrAzxGlxOmyG+vdOnBan
/VkTdoY4LU6HzVD/3onT4rQ/a8LOEKfF6bAZ6t87cVqc9mdN2BnitDgdNkP9eydOi9P+rAk7
Q5wWp8NmqH/vxGlx2p81YWeI0+J02Az17504LU77sybsDHFanA6bof69E6fFaX/WhJ0hTovT
YTPUv3fitDjtz5qwM8RpcTpshvr3TpwWp/1ZE3aGOC1Oh81Q/96J0+K0P2vCzhCnxemwGTqZ
3q1Z885vb9w68erll1y2fMWms9OhTWdHQFrwb0xUzjp4+XXLL7rmsouuunT5iguWXzm0+MoL
z73qKjgQdfwhQ8efcNzQEScMLTmps3QpzMMXwR1FUZrVMJZeec3yoSuuXH7V8svOX37O1cuv
uhrORedefc2lKOPILGItf/lZN0ynmGX9rt5ZseKi5eddee4151981UUrfnnxinMvvWL5prPL
mMnXE/wTtcschUs2C7Z150sYZkJrdt2F0M3NkwFsogBKoAIYZ5YTm94wNGZszODYLJDhMeNj
JsTMSNh0woyEGQkzEmYkzEiYkTAjYUbCjJQZKTNS0x1mpMxImZEyI2VGyoyUGRkzMmZkzMjM
GjAjY0bGjIwZGTPMrsqZkTMjZ0bOjJwZOTNyZuTMyJmRcxmGKwUzCmYUzCiYUTCjYEbBjIIZ
BTNKLqNkRsmMkhklM8zOKZlRMqNkRskMw8KKGRUzKmZUzKi4jIoZFTMqZlTMqLmMmhk1M2pm
1MyomVEzo2ZGzQyzpx0PmRNHTIojZsUR0+KIeXHExDhiZhwxNY64tNjufpMbm9yGAQ0FGg7E
JrdhQUMDw4PYECE2TIgNFWLDhdiQITZsiA0dYsOH2BAiNoyIDSViw4nYkCJOTZ8NLWLDi9gQ
IzbMiA01YsON2JAjNuyIDT1iw484M+trGBIbisSGI7EhSWxYEhuaxIYnsSFKbJgSG6rEhiux
IUts2BIbusSGL3FzcDGMiQ1lYsOZ2JAmNqyJDW1iw5vYECc2zIkNdWLDndiQJzbsiQ194ubL
bQgUGwbFhkKx4ZA9lBkWxYZGseFRbIgUGybFhkqx4VJsyBQbNsWGTrHhU2wIFRtGxYZSseFU
bEgVG1bFhlax4VVijmxJRG4khleJ4VVieJUYXiWGV4nhVWJ4lRheJYZXiTmuJIZXieFVYniV
GF4lhleJ4VVieJU0x5fmAGOPMORk0hxjmoNMc5RpDjPNcaY50BheJYZXieFVYniVGF4lhleJ
4VVieJUYXiWGV4nhVWJ4lRheJYZXieFVYniVGF4lhleJ4VVieJUYXiWGV4nhVWJ4lRheJYZX
ieFVYniVGF4lhleJ4VVieJUYXiWGV4nhVWJ4lRheJYZXieFVYniVGF4lhleJ4VVieJUYXiWG
V4nhVWJ4lRheJYZXieFVYg5OieFVYniVGF4lhleJ4VVieJUYXiWGV4nhVWJ4lRheJYZXieFV
YniVGF4lhleJ4VVieJUYXqWGV6nhVWp4lRpepYZXqeFVaniVGl6lhlep4VVqeJUaXqWGV6nh
VWp4lRpepYZXqeFVaniVGl6lhlep4VVqjlep4VVqeJUaXqWGV6nhVWp4lTYK1khYo2FWxHi8
ShsZa3SsEbJGyRopM7xKDa9Sw6vU8Co1vEoNr1LDq9TwKjW8Sg2vmhOQ1PAqNbxKDa9Sw6vU
8Co1vEoNr1LDq9TwKjW8opCY7y77CfDoaJQNpdEclEYDTKBRACMA5jhsDqVGOczB3+iGkQ1m
6AwAW5DbSmcA2Ag6A1jnZwBJ255NoYTUFxFUP21ODvhRmRVFHZfwmy8rXEVRxTgbq7KyOR2C
q6xrnGnlOA9qzpPgqouyxtG4rl0eDppZWWRQubw5NUvaOG7VdZ4WOLdozhjhKqO0KssixbGo
OWy0swh6VJZ1VDennkk7S6u6zJFaRM15KFxljV7k6EXUnF4m7RxiXCbQl6huzpzgQh3iibOM
5swpaRdQV5xG5eyGOTjBVeF8AofyKGo0PU7aZZZiraMKa9Sc/CXtKqpLqDpyi+bcCq4qynCy
irbtaVLSrvMcWxNHYzRvjnNpO8L6lmWJM9ZGsuK0DZbn0OgS5z32vLSNE5soj/K6rOwqpm0o
Vo1zT5x62PPNFJumhipmMXrRnIal7RwnjtgQUQkZNcfYFOtYp2ValhFWzGzTFCtUZXWBxKg5
p0InqjKtK+heVGfNqXxzxssv4W8sZJZRXkAMscRmz6IX6D92WFXXzQkIGovKvIL6l9gZzfkn
tiFWJsMGKmN78o2dVmD3RNChvG7O0JN2XIES2GoZzjXMYuM22Id9HWH1s2Z0EbcLkAuDD9At
anZtDE5go2Otc2wds5JxGyeNeY4Vh+w3p7NRu67LCBu/KPNmS2DsC3JgH0UkUDOOaYPqeVWU
OE+2p7JRO8PJE8YeIH3VjAoifDWweJzxYnM3p/NRG3sDp4dVHRfNKKluY8Nj2djVBUhthmBY
IDqOvtZQZLOKdbvIo6LKcH4QVZUR9xq7sSxwWohtg2huiLqdYpWx7csSQmxO5Wp88aIMO40s
B69NFMYZZV3h65lnuflS1W1wFqzBvsAnZttU7RrbF2OdNMW2MSeBVRsdqHBSRzrn5gymAku4
yxDJVeTGqbDlI5yzRmmJTWvOyip8qfDFz9ET7E1zSlS1sWVwbonGKgxXuNpw4euPXYHTDXw/
+E2r8PVHF0H8OsPeaJpHB3AcwXcBHDSnJBX2Yo3DgSEqCGwSQSq0UWOPRaV14bsZ4ciV5RUO
TdwSFb5oOG+pcJjC18WcNJZt9AdnZPhKgfbmXBMufp2ws2scY8xpconvMQ4H2BEgYnPkgAvr
g4NcCRqAFWgergg722yrGvHGhcMbvhs4X8SONKeIPPsRwt0GOLRL/CR+Ej+JXy/Ez4x8JX4S
v74QfYmfRn4Y3En8JH79KX4ch2GY9xwjPw4sJzXy4yhSI78BHcFK/CR+Ej9d9tRlT1327IvR
Wi8vI0v8JH4SP4lfj8Svfy57Nj/T6Se/AR3UTUQjpX3SPmmftG/aaZ/mu4Q7D2UiwtWLGImf
xE/iJ/GT+D37VU/95DfAI0OJn8RP4jetxa+5yaA3dzpM/VXPic13aTRMdzpotNc9YpT4Sfwk
ftNa/Jq74nojfuaRMgHe6TDpyZ5Nom7zG8i5MBI/iZ/ET+LXo8ueEj/d494/o0uJn8RP4ifx
k/g9+29+GvnpNz893UxPNzMaqaebmcd06ulm/fV0M1327P6tS3YzOtXITyM/jfw08uvbkd86
nvCi2Z4a+Wnkp5GfRn56rrWea63nWvfPb3rPNcLVyE8jP438NPLr25Ff856H53q0p251eC4h
mI6fS/wkfhI/id+Ai59+85uO4vZc6yzxk/hJ/CR+Ej/N9hzIe/l+nwBK/CR+Ej+JX4/Eb+qf
8KLLnoPzG9zvE6p18ZnET+In8ZvW4sdLgnqRu17kPv1EVOIn8ZP4TWvxm/TjzTKjmnmZx1le
RlmRJPHUP+FlHd/q8Cw3uXOsidfbRkmSlkWeJHWVN69HKossL/SEl/4RUYmfxE/iJ/Hr0WVP
iZ/ET+JXF2WdRlFdRzx3gsSmcZnh1CjJijzl2RpdWVzXeVrEVRnx3ImuMkqrssT509NRWZTg
kkRZR3WUNkFZWtVljtQiinj2ibysrJOyzuM0iWLrypO0KJOEbRe2DznqSY6YrLDLK5Jc4oct
mLarMq2rNE6iOov4y02zGc22/M2ftK0nvOgJL1mUllV/PeGll7c6aOS3Ln5/ez7ahHAkZIYp
4wo3scZVnpZWG5K8zIqijkvd5K6b3I1GSvwkfkGJ39Rf9uQSddnz+RCrXi9T4qeRn0Z+uuzZ
o8uemu2py5667KnLnhxM13mOcXSaZbi4a64lpu0Il3nLsoyTKqnN+Dptx0mcJ/AmEcI4Ck/b
Ca4/5lFel5W9spu206isY8wqSJM4s4lZVCd1lsVxUdfmUnLazuMC4/Y8KpM6MiP6tF0kdVqm
GLJVSWyjyqzK6gKJES5zNkvUZc/EbPuoXURFXhVljAdZ1eaKb9TOkgJ7BJfbsd008gtq5Mfd
UbX1hJdej4qmQ3sa+Wnkp5GfRn49GvlN/YSXiYkfz2vKdveb3HnOBw9PJXGiU+tOh/4ZsPVK
l6V90j5pn7Rv2mlfJfGbdg90eaZoSvwkfhI/iZ/ET083m3ZiKPGT+En8JH4SP4mfxE93OmBa
SIpfAqIoSe09IGWWFrrTwWik7nTQfJffM99Fkz012bN/fjvUyE8jP438NPLr0chv6sVv6m/z
49mPbvN75u9n/ViX+En8JH4Svx6JX/9M9tSEl/4Zoa0rYZX4SfwkfhK/ARe/Xj7dTA94WVdi
NNXtSvwkfhI/iZ/ETxNeNOFFE1404cU8i+Y3T7P+jaXnWusBL0n2eya86LKnJrz0z+VUjfw0
8tPITyO/Ho38pn7Cy2Qf8KLf/PpHpNbV5VCJn8RP4ifx65H4Tf3Ib2KzPX/36WaTFz/N9lxX
YjTV7Ur8JH4SP4lf34rfxEZ+vZzwIvGbapFaV8uT+En8JH4SP4mfJrxowosmvGjCiya86I1G
eE1QmdVlFiVlnJZ5yQuHVRvvtO7LCS+9HPnpVod1NRKb6nY18tPITyM/jfx6NPLThBfN9uyf
iTQSP4mfxE/i1yPxm/oJLxP7za+XE1408pvqEdq6Wp7ET+In8ZP4Dbj49fKypya8rCsxmup2
JX4SP4mfxE/ipwkvmvCiCS+a8KIJL5rwMlgTXnp52VMjv6keoa2r5Wnkp5GfRn4a+Wnkp5Gf
Rn4a+Wnkp5GfRn6TG/lptqdme2q2Z12UdRpFdR3xigPGl2lcZmWRJVmRp5wvRVcW13WeFnFV
RrV1lVFalWWRpk9H4U6joi7LOqqjtAnK0qouc6QWUWQeupy0s7JOyjqP0ySKrStP0qJMErZd
2D7kqCc5YrLCLq9Ico38NPLTyE8jP438NPLTyE8jP438NPKb3Mgv1FsdNNtzXf1u1s/t6jc/
jfw08tPIb8BHfr2c8KL7/PpZ8Lr7LvGT+En8JH4DLn69HPlJ/LoFpJ9tiZ/ET+In8euR+GnC
iya8aMKLJrxwSk+d51WeplmGaT3mh7S0HWGCT1mWcVIltZl1k7bjJM4TeJMIYZzTk7aTGJUo
r8vKzulJ22lU1nFWJGkSZzYxi+qkzrI4LuraTCJK23lcpJj5E5VJHfF0F20VSZ2WaVlG+DHT
RpVZldUFEqOkmWqUtqsyrasUi62zSL/56Te/yf3mF6r49XLkp/v8+nm01913jfw08tPITyO/
Ho38Qp3w0svf/CR+3QLSz7bET+In8ZP49a348VpG1Y6qOsI89Syv4iTlMA8u3C5VVlVW4kJJ
LfHrZ5FaV32X+En8JH4Svx6JX6iXPXspfprwsq7EaKrblfhJ/CR+Er8eid90uOwp8ZtqkVpX
y5P4SfwkfhK/ARe/Xk54kfitKzGa6nYlfhI/iZ/ET+Knx5vp8WZ6vJkeb6ZbHXSrw+RuddBl
T93np/v8dJ+f7vOLSzxlvDR3GyZtPIm8zKIsLuO4uZkRTyMv8NzxKOX9jKl9Znlc4VnnuDsy
S8rUPKA8btcxH2Ie4TbHLOKxNY7bBZ6aHkd5hlsSm2eWx+0sjasKdzfmuAuS16UQlURVnuMG
xzTKK9NW1K7rMsJNlkWZN3c8Ru0STz3HvZgRn4xu7rGM2kUET1HGJfpi87KkwJ2XeKA67o/k
TPc4aidcfFynuK0yNycLURt3XSboRh0XsXkGe93GDZZYNm7pLPC0dt6cWWOB6Dj6WqdZs4p1
u8ijosrSpIiqKuUq1rhdsywS3B2aR4hmJ+p2ilWO8qIsU/SOnajbSRlluDmTj2/HA9uNK8Yq
11WSVnmWm1s46zYe4467Q7Ev8InZNlW7xvaNM8yHxLYpmsmR6ECVYEsXZZEnbL5qlxl3GSK5
itw4FbZ8lGRILLFpa+6zqp1jY2Y5eoK9GYcqfrrsOdWXFPthebrsqcueuuwp8dNlT1321GVP
XfbUZU9d9tTIb3IjP93qoMueuuypy5667KnLnrrsiQvU5uIorndnuAKd4hJpYa+X8ql/EZ7r
V2e4CN1cVcV11xRXrgtcki3z5tornreH13ua5/Dh+XymLVxLRxs1LlRHpXX53+TObpW4Lo3L
5LjEXeOVoYWdxlnldY7Lz7j83rwItMSoOMF61CUufuNauEmsIlziNleIa8QbF95WmuNFpGgv
qmKeBfTDlb/p3Edd9dRVT1311FXPAb/qqXvcp7PIrW3dJX4SP4mfxG/aiZ8GftN+YCrtk/ZJ
+6R9A659muu5tsHPdPZL/CR+Ej+Jn8RPP/lNu5GgxE/iJ/GT+PWt+HH2yXO/00Ejv+k8wlvb
ukv8JH4SP4lfj8RPNzposmf/THKV+En8JH4SP4mfLnvqsqducdct7rrFXbe4D9Yt7r287Mlb
DXHnn27z63ux1MhPIz+N/DTy69HIT0/21GVPXfbU8130fBc932XaPd8l1N/8ejny0wNe1jaB
pN/8Gvlp5KeRn0Z+Az7y0wNe+k2YpqK/Ej+Jn8RP4ifx04SXvv8Nz1cwJX4SP4mfxG/AxU+X
PX2FYTrES/wkfhI/iZ/ETyM/jfx0q4NuddCtDrrVYbBudZj0b37NkFFvNBpIYdTITyM/jfw0
8uvbkd/EHm82afFrEiV+Ej/O3k+KoorjJK2yMuNpEV14zWOMV1DGWZ1l1qVbHXSrg251mHa3
OoR6n5/Ebzr8hue7jhr5aeSnkZ9Gfn078mte7e7/HvdK7/MbyNGcjwBK/CR+Ej+Jn8RPE16m
nRhK/CR+Er9pLX68JFj1SPym/gkvE/vNT7c6+IyIpkusxE/iJ/Gb1uJHYehf8ZvYZc9Ji1+T
qAkvAzkqlPhJ/CR+Er++HfmtY/HTbE+cGg3qSFDiJ/GT+En8pp34ab7LwGraRLVa2iftk/ZJ
+3qkfaHe6TDpq54a+GngVxQRaUCp1G1+3AxVVJdJRuEsSrtlqirK4iTJijqueBBAVJ3nVZ6m
WZanhXlqStqO0iIuyzJOqqTmyWectuMkzhN4kwhhjSuJUYnyuqyiyNw5mbbTqKzjrEjSBLdT
NlFZVCe4szJGL2r+7o+28rhIyzqPyqSO+I2Hq0hwt1lalhGeXGOjyqzK6gKJURLZtqoyrasU
i62zSA940QNe+uUBLxOb79JoWF3hbuQMXynQfoJ3OugnPxxEJjqS6rc4jfw08jMSKfFLzIlH
1MZ5Xi7x6xfx009+gytO61pMJX4SP4mfLnvqsqdu8xvYEd7aRFTiJ/GT+En8eiR+U3+bn0Z+
GvmtTdyeyy/xk/hJ/CR+fSt++s1P4vdcIre2zyV+Ej+Jn8SvR+Kn2Z5pillpURVzDLy2g678
YWwbiZ/ET+In8euR+PXPZU/d5jfttVnaJ+2T9kn7pp32TfBOh+YWCT3cbCCFUuIn8ZP4Sfwk
fprsOZAC9/uuMEv8JH4SP4lfj8Rv6n/y03yXMH4++30iE+pnEj+Jn8RP4te34jexOx0m/YAX
XfYc4Hk7Ej+Jn8RP4jfg4qdHe4Y6+no++yXxk/hJ/Ka1+HFw06u3+U39ZU+N/HTZc7ICKvGT
+En8prX4cVQk8Ss04UUTXqIYryEozZP+8QaHvMwKvKSg1EsdigrPgU+jjOfJOGPQSx3q5jUf
aRtvssCbJNKqrkEXbh28uaLMqwT3+UZxVppXSyTtEm+oyPDWizKOmzdXJG28oSKpopQvr0jT
ZrPGVVzXeBVGlpSpeZlF3Ab78rqO8E6LLDLvyojbRYH3W0R5hvdPFGZ/xO0sxZs08CqLHK+8
MG+uiNt4cH+e420WaZRXpq2oXddlhDdqFGXevN4iapd1gadYS/z69rLnxCa8TPqyZ5OoWx0G
Uhg18tPITyM/iV/fit/ELntOWvw04QVnpZO9rBh6nsRP4ifxk/hJ/HTZc2BFbm0iLPGT+En8
JH4DLn7NAG4S77LVyE8jP/3mp9/8jEbiffB5kcY5Xh2v3/yyuE6LtGx+6YzaUZ0k+Omxjos4
4m+YdbvGh/i9qEqKqjS/o9f4kRE/VuL3yTrNmp8163aRR0WVpQkeh1yl/Fmzbuf4mT3Jcvwe
imj+YFm3U/zMiW1flinetMuLfXU7KaOsrtISP50mCa/s1e0YP3PWVZJWeZZH/OW+buN36iJJ
8fsrPjG/h1btGr+pxlmUpvg9tGDioE940WXPtY1+prNfIz+N/DTy08ivb0d+63jCi0Z+ODUa
VIGU+En8JH4Svx6JX6gvddBlz0EVsD9kvSR+Ej+Jn8SvR+I39Te5T/3Ij5ecS9zrhGvcZZEn
SV3lzeuRyiLDTwJ6nV/fjBQlfhI/iZ/ET+I34dmeEr8/ZLQVUq7ET+In8ZP49a34Tf19fhK/
kATsD+mLxE/iNy3Fz0yFjPWIl76f7jn11z25RF33/ENUJ5RcqZ/Ub1qqHw9hEr9e3+sQ6owX
3esQiuCE1A+Jn8RP4qfrnrruOeEf/TTyC0nA/pC+SPwkfhI/id+Ai5/udfhDRGJQcyV+Ej+J
n8Svb8VPv/kN7l3o61p0JX4SP4mfxK9vxW9i0z018lvXQtKP7Uv8JH4SP4lfj8Rv6ie8TGzk
J/HrR3Fa132W+En8JH4Svx6J39Q/4kUjP132nKxISvwkfhK/aS1+HBX16rUOUz/ym6z4NY8k
q9MkzooyrosJT/bUTe6T1ZrQ8qR90j5p37TWvunwSqNJX/Vs7g/Ea6mKsq7LpEjKSnc6hCZi
k+2PxE/iJ/GT+A34VU/d4z5ZgRjkPImfxE/iJ/HrkfiFetXzd8Vv0lc9NfAbFD2U9kn7pH3S
vmmnfZXEr2/ePLSuxFbiJ/GT+En8Blz8Jv2TX5Oon/wGUiglfhI/iZ/Er0fiNx1udNBkz3U1
EpvqdiV+Ej+Jn8RvwMXvd3/ym/xlT4nfVIvUulqexE/iJ/GT+PVI/PpnvovET7fGS/wkfhI/
iV+PxC/Uy569HPlptue6GolNdbsSP4mfxE/iJ/Gb8ANeJH5TLVLrankSP4mfxE/i17fiRymq
2lFVR1FcZXkVJymHeXClaV5WVVbGWV1rtue6EpB+blfiJ/GT+En8+lb8JvZkz15e9tSEl34W
vO6+S/wkfhI/iZ/ET5c9B/Jevm6xe6Yt8ZP4SfwkfgMufr287KmR3zNFpF/rEj+Jn8RP4jfg
4tfLy56a8NKvYvfMfkv8JH4Sv2ktfhwVTb+3+U3+Pj+J3zNFpF/rEj+Jn8RvWotfMzmyytIq
KfO6KIs8aWaRlFldZlFSxmmZl41EFkWUZFmUllWe16lRzbzM4ywvo6xIknjqb3LXbE/drD5Z
8ZX4SfwkftNa/Ho58uufm9wn/VIH/eQ3Wa0JLU/aJ+2T9k1r7evlwC9U7evlfBdd9QxNxCbb
H4mfxE/iJ/GbdvNdNPCbdjc2PFMjpX3SPmmftG/aaZ+mu+iXQomfxE/iJ/HrkfhN/XSXZmbO
cz3cTDc6PHPUozoOe0k7ITNMGVeYyxVXeVrymoBxlVlR1HEJP6+a01UUVYzH5+GReZlLLOs6
ThNM+aqzzEZhzlidRlFdu7w0LrOyyJKsyFNeNEdTaRbXdZ4WcVVGdoFpGaVVWRZ4Kp+Lwmyz
oi7LOqojTi5DHmal1ZiVVudFFNnlZWWdlHWOXkSxdeVJWpRJwrYL2/cc9SRHTFbY5RVJLvHD
Rk3bVZnWVRonUZ1FPIQ1m9Fsy9/8SdtlGeVFGueF27NpO4uTGDusquskN5lpOyrzKqniEjuj
tCTBDsPEwSwu4zi1u4OzA6sozSNMG7S7Nq5AiTrPs6RMzWLjNtiHfR2lEdL5i1IctwuQK45y
0C1qdm0MTsRVFZVJnsSZoVfcTiJMSCzTMo3yyrQVteu6jErQC9MTTVDULkGOvJL49Uj8Qv3J
T+Insfvdka5RuEZToF4Sv6RdVEmcpkkcRc0DcrGFyiyF5OPsMoVsNhuriuoyySicmBluXRWO
7QnUvcZxuHHhMI5TiTTLIPFOFyD2OP7GSZXURoHTNsQjT+BNIoQxMW0nUCGKQllZfU/bOPrX
MfQCXctsYhbVCc43YvSiNgfztJ1Dh3AWABmoIyM7abtIaigAVAsrZqPKrMrqAokRxK5ZosQv
Mds+auM8L6+KMi4hxFY0s6TAHsFJF7YbhxpxhFNGaG9cp9jcjeRHbeyNBBpcx0VsztPqNjY8
hBe7usAZHTd0DbWFaoMgdZo1+l63izwqcJ9BUkRVlZI5NXZjWSRgTR4hmp2o2yn0HiceZZmi
d+xE3U5wewHOWHiKh5M644qh93WFc9M8y82urdvgLFiDExF8Yk4MqnaNk4sY9yukODEomNir
u/xCFT/u2rJdVzg7zvCVAu112fN3xWC6CaTETyM/I7cSP4nfH36XX6jip5HfdBO2iayvxE/i
J/HTZc8Bv+ypkd9ExGC6xUj8JH4SP4nfgIufRn7TTdgmsr4SP4mfxE/iJ/HTC42m3X1/Ej+J
n8RP4te34scpXOvwPe7NkBGTljDBGFPcigTToMzkmSrC7CbzFNS6yjmXqWxjMjtmQqeYlRZh
pjNcExl9KOb5204SP4mfxE/i1yPx4yG/amMebFLgcdeYXQnNaFy40wlzjlPcD1XY52FzEnSE
ac51hhtP+KNchemruBGJM59xu03e3MGH6ci488lMS8Z0ZROF+2fQRo27m6JGip5b/Hp52ZOd
KNsSv+dPtHp1wiDxk/hJ/CR+PRI/zfbUyK9/RFHiJ/GT+En8Blz8NNuzV6OlQWpH4ifxk/hJ
/AZc/Hp52VO/+Q2KAEr8JH4SP4mfxE+zPafdBB2Jn8RP4ifxG3Dx+93Lns0EzZoPC8Sj7Go8
PriwQzpM3szxmDk8Y7Z5KDAmt2iy56AM9rrXQ9on7ZP2SfsGXPt01bP7oC+7mZMj8ZP4Sfwk
fj0Sv6m/06G5+UFvNJKg+U8ylfhJ/CR+Ej+Jny576ic/vc5PbzQyL18yL/N5xh+9zk9vNEoy
vAqpxJsS7a3quJc9znK8WwkvZ4x1m59u8/MfgT1fo1aN/DTy08hPI78BH/n1cL6Lnu/yfGlV
r5cr7ZP2SfukfT3Svqkf+E3syZ69nO8i8eu1CD1f7Un8JH7TUvya99dHeK96gde2S/36Vv00
4aV/LjM+Xyq3tuVK/aR+01L9OGSIJX5RXnBYVPWt+E390M/eDaiXOvT9BBmJn8RP4qeRX9+K
38RGfr/7m1+lm9z7XrzWNqKbqF/iJ/GT+En8Blz8evmjn0Z+ExWX0OMkfhI/iZ/ET+Kn+/ym
3UhQ4ifxk/hJ/CR+Ej+Jn25y103uusm9wrOO8ZLw2tzkH7XxXOMkTrK0ynST+/S6yb25XqoH
Ww+kMGrkp5GfRn4a+fXtyG9isz014SX039+ej/5J/CR+Ej+JX9+K38Rme2rCy/MhLqEvU+In
8ZP4Sfx6JH6hvtVBI7/Qhej56J/ET+In8ZP49Uj8pv75ZhMb+Un8ng9xCX2ZEj+Jn8RP4tcj
8Zv6kd/EfvPTZc/Qhej56J/ET+In8ZP49a34TWzkJ/F7PsQl9GVK/CR+Ej+Jn8RP9/kN5O0M
v0+AJX4SP4mfxK9H4hfqb369HPlxrFm2Kz3Yuu/FUuIn8ZP4Sfwkfhr59b2Y/b5R3rN9JvGT
+En8JH49Er9QJ7xMerZnM2TUE14GUhglfhI/iZ/Er2/FTxNe9DLbZxvVTcQn8ZP4Sfwkfj0S
v+nwm59eaTQRYemHGImfxE/iJ/HrkfhN/WVPjfw08pus0Er8JH4SP4lf34rfxG5yn/Rvfk2i
fvPTb36zKZVFUcVxgre7lBl/DaarrOs4TfI4qzPzDhi46qKs0yiq64j0QVAal1lZZElW5CkJ
S1cW13WeFnFVRrV1lVFalWWRpk9HZVFS1GVZR3WUNkF4tUxd5kgtosguLytr9CJHL6LYuvIk
LcokYduF7UOOepIjJivs8ookl/hJ/CR+fSt+Gvlp5KeRn8Rvdpy287hIcRYQlUkdmXOTtF0k
dVqmZRnhRYXmtCNtl3gvXV1kcRwlzWlH2q7KtK7SGPUs4sWr5hzCnEj85g8yyygv0jgv3GlN
2s7iBAvFCUmd5CYzbUdlXiVVXOJMpLRnSDhbKbMoi8s4Tu25SFbg3CRK8yivU3teE+Mdejir
ybOkTM1i43Yd80QnSiOk8yelOG4XOLOKoxznWlFzXhO3szSuKqx1nsSZWcm4nURVnmPF0yiv
TFtRu67LqMS5VZk3WyJqlzgzyiuJ37QTP579lu06BV/w7sYa59cFeYMb+Kq8zivSuW7OmuHC
+xxxgl/irY54yWMTpdv8+n4wyHGbG7/lcVUUepet3mUr7dO7bGdXOEPi6UpSxmmZlzxfqXDW
EU2vd9lytSV+2AiTHVyFnCfx01VPXfXUwG/aDfyqiY38ODCQ+En8sAUolfrJj5uhinARJKNw
FuakmK4KF/US/KZZ4wJcs7Fw/a7K0zTL8MOmuyCInzhx4S1OqqQ2vzumbVw1zBN4kwhhTEzb
CS4/8mpgWdlfNdM2LvvVuEKT8DqNTcyiOsGvrDF6UdvrmbrqqauedYVf5PMsNxe06zZ+4AZr
cAU6L2tzRbhq17iqHGdRmuKKcMHje9Uj8Zv6Ox3I+6odVXWEa1ZZXmE2QrNCWLu8rDAzAV+X
uhnA1RXmBGT4SuFiv8RvMEdzPiNNjfw08tPITyO/vhW/yc53mdjA71muenKBGAvqJ7++vxIq
7ZP2SfukfdNO+yY48HsW8dN8F5/BVcixEj+Jn8RP4jfg4jfpq54SP4xzQxawP6RvEj+Jn8RP
4ifx050OAytyaxNIiZ/ET+In8euR+HFSV9XG7ZdJkePmzCrG3XGNC0+4wA2XKZ6DUdS8pbPC
Ey4wJQcTveoM91xyhFXhYRl4AAXnfuFO07z5MQ+3neKJF+Z2VNymaqJw6yjaqPFUi6i0Ls13
WdsBXv61j1wlfhI/iZ/Er0fiN/WTPSc730W/+a1dFKaLYEr8JH4SP4lfj8Qv1JFfc7feJO50
eJbf/DTbc1DEUeIn8ZP4Sfx6JH6hjvw04WVQBKuX6yHxk/hJ/CR+Ay5+vRz56VaHXgrQ89mW
xE/iJ/GT+PVI/KbDZU+J3/MpWL1ctsRP4ifxk/gNuPjpsmcvRWNQ2pL4SfwkfhK/ARe/Xl72
1IQXiZ9eZavnWhvZ1Nv8zCPLozaeMp7gpYJ1XMTmrcs1XhaH1xpmeIR5gfcz84a3Gq8PxGsI
8eDzOs2aFxbW7SKPiipLkyKq8BY5E5XHZZHgaeh5hGi+irBup3iBIZ5CXZZpXhU8ANe4LS7K
8ApGvrAZr2g2rhgvMNRzrc2jrrufay3xGxTB6uV6aOSnkZ9Gfhr59e3Ibx2/1OFZbnXQb369
FKDnsy2Jn8RP4ifx65H4Tf2tDhMTv16O/CR+z6dg9XLZEj+Jn8RP4te34qcnvOhJLZMVRImf
xE/iJ/GT+OnB1nqwNV6HnKfmx3mjiyXeAl3j1/ci4tVvuvQid73IPc7x6viGEWlbE1404SXH
1JsiSeKpv+w5sZGfbnWY7OhokPM08tPITyM/jfw08tPITyM/jfyqJE7TBPPKk5S/k+P0AG9j
wXgXr01JcX7buCq8aUW3OhjZ1MhPIz+N/GaX7bLI8iJN8dKmqIrJiUEeNQ3Cumnkp5GfRn4a
+fVo5MdD/kC9z0+3OgywiEv8JH4SP4lfj8Qv1N/8dKvDIIzUer0OEj+Jn8RP4ifx029+0+4y
rcRP4ifxk/gNuPhptmevR02D0J7ET+In8ZP4Dbj46bLnIIhVr9dB4ifxk/hJ/CR+uuypy566
1UG3Opip+3yXQPyMP2m7LPFmgVQ3ubeTPKuz/8/ee8BZclRX42+1WuW4ynmU81N3dd6dmZ0n
rXLOWVoJrSRgFdAqJxYFkIiSLITISQSDCcYyBqTZ1R+TwTY2yZ/BBmP+CGODMcg2MkHfOdVV
0mNZoan53q5qZs785ry6dd+91dXd5/Xp6pg2WYkXN+hWh+fvVgc921O3VEx2RKiRn0Z+Gvlp
5DegkZ9uddB9flNHjCV+Ej+Jn8RvQOK35m91mNjITxe8THZ0NJ3zJH4SP4mfxG/Kit+af7Yn
p1h16wRvLq7KwpimLvieYj3hZcqdM5T4SfwkfhK/aS5+g7zaU+I3XUaDEj+Jn8RP4ifx09We
U27k9v8qwhI/iZ/ET+I3IPHTBS+64EUXvDRlhXcgJP6tb6abpVWOx56bvCwynqSG6ma4VLwp
sjKtq4RHzemqkqyuKjwb/emoPDFlU1VN0iRZG5RndVMVSC2TxF6Lb7p51ZiqKdLMJO3l+aZb
mKysjGHbpXsVQ4G6KRCTl256pSkkfhK/GS1+/HHUAxK/NX/By8TO+Q3ysCe3Xjrn9/866ooh
XyM/iZ/Eb0aLH4VB4ocd7NLJGi5gKWrsYOPP7jZD6XKDnXm8xKw0Va1zfjEI1yD6IPGT+En8
JH4a+U1Y/DTyG4TwxNCGxE/iJ/GT+E1z8RvkfX4a+cUgXIPog8RP4ifxk/hNWfHjOKzuJnWT
4MGMeVGnJmuP4ya4bqCq67xKcxy+tOfpmhoXBeR1kiQGCa0rM3jzepU2z3LYsz1ZqMOe0/JK
UImfxE/iJ/GbsuI3sQteJi1+baLET+LH6zFNWdYpdq+wS5Vzt4gunAvGLlWBXazcXX1pdLUn
l0xTFHWRZXmOa1rt04+zboKrW6uqSk1tGnvJadZNTVoYeE2CMC7SrGtSVJKiqbCbahdp1s2S
qsFOquGuqkvMk8ZgkadpiRXQJhYpnrTcFEllmsSunqxbmiarMjyRGk/sdlFVXudNiUTsAru2
6ipr6gyTbfLEdnWlZ1q7XujB1tzapokebF00vPi67hYVfvj+wdZr/laH1TzyW4X4cYq62nMQ
hx2f7zY08tPITyM/jfym+civPXo5icOeqxA/nfN7vkVrUNOX+En8JH4Sv2kufq2GDUb8NPIb
lPg83+1I/CR+Ej+J3zQXv98f+U3sehcN/HCM9/nWqNU1fWmftE/aJ+0bkPat+VN+E7ve5fe1
b4IXe65C/DTwW11itKbblfhJ/CR+Er8BiZ+ebqZHe06dkaLET+In8ZP4Sfwm/IAXXe+ypkdo
q2t6Ej+Jn8RP4jfNxU/Xu6wuAZnK7Ur8JH4SP4mfxG/CIz+d85vKgtffd4mfxE/iJ/Gb5uI3
6Qte2sTfecCLxK9fQKayLfGT+En8JH4zTvwmfaeDtG8q611/36V90j5pn7Rvxmmf7nSYOhdl
9gvWIG2Jn8RP4ifxk/jplN+0vZf92QRT4ifxk/hJ/CR+Ej+JH96JVeCtAHxwPd7WUFR5WTZp
VZYJLxamS+904GKok6YyOYWzrNySqeskT43Jsbxq3uuLKL3TIa94xQAWRYUXVORYQFWati+u
MF28oMLUScZ3V2R8PwCi0jptGiy13FSZfYtE2gX7iqZJ8EqLPLGLNe2WJV5vkRR4hUhS2oWf
dvMMCx1vsijwxguelEnTLt7YVhR4mUWWFLVtK+k2TZXghRolXkNgg5Ju1ZQl3ruR5FVjbFNJ
F1QvarzgrUJfXF5uSrxlI8eLTHDlA1vXOx2KVb7TYSbc467b/J5tJDXV/NjgGLd5whuJaoic
xM+kGd4ahPdd2pdicsOdZ5B8vP0yS3KvdBK/dnco60Lx8RalrG4a7CtRGfDWpqqoTZ1WSSrx
g1zWpqwru0PZQG2h2hDqJstbfW+6ZZGUdZ6ZMqnrjPLRdAvsbxq8BqtIEE0FbroZ9D4pyqrK
IM3cADd4k1iS4y1UFfYhjP0VN90Uet/UeN9YkRf2XVVNF5zFa7CwLvCN3TGouw12LtIcL3vF
jkHJn389zUd+/NVWXT3WWuf5+gVa4qfDnlav9DY/jfwMxtg4kFEYamuNfT4O1iGTWVXYwxs1
xtyJyaGaFQbVq3qb30wY+elqz34Bmcq2xE/iJ/HTYc9pPvJr79brH/npTocZd4pvZZ2W9kn7
pH3SvmmufZM+6tmK5u/c4q5TfiuLyFStS/wkfhI/id+UFT8eg6y7OB2f4GKFvKjT9kQ9XFlW
VHWd49wmrqDSKT8sgakqUqur3xI/iZ/ET+I3IPHT2/z0QqOpI7ISP4mfxE/iNyDxW/PXu2jk
N3XEZnWN4CbbrsRP4ifxk/hNc/Gb9Dm/NvF3zvnpYs/Jik1seRI/iZ/ET+I3zcVvkOf8dMFL
bCI22f5I/CR+Ej+Jn8Rvwk83k/hNVmxiy5P4SfxmpPjZp5/gKWV6vJme8JLjWXZNOWH103HP
2FRssv2R+kn9ZqT6cRMm8Zspjzcb5HFPid9kxSa2PImfxE/ip+OeU/a4Z/sktue60W/SV7ys
4i53iV9sIjbZ/kj8JH4SP4nfNBc/jfwmKxDTOU/iJ/GT+En8JH465zfjHgEj8ZP4SfwkfhI/
iZ/ET+/zq/U+P14MYt/jutJH1q0qvAEuS4sS75fliRS8vE/v87NvMUy6SWMM3qnbpGWa8OW8
TbfBy4D0Pj8+fRNvMc7xXuGsSPGyZy6cupvleOVgYcomx6uFyaUaLygsMryPuMS7BquiPZtn
8OJMEC5BmdStCy+JRBsNXj+cVM612s756S53rJjpeuhTIz+N/DTy08hPIz+N/KatyD2beEv8
JH4SP4nfNBe/SV/tqZGfRn54gzNpQKksyzrFi0PwspCc11DRVTVNisMVeHlIbo+TwYU3QjdZ
kviDY6ab4bhHVeYmL4vM3mMFV57ibSNZmdZVe88xXFWS1RWOc2RPR+Fd0rgBtWpw2IOHSzC9
PKsbvHO6KcokcdPLcQykagr0ImmP15luYbKyMoZtl67vBeoGB1YSHHppmypNIfGT+En8BiR+
sb7WQeL3bKOfmezXyE/iJ/GT+A1I/Nb8ax0mdp/f79/qoDe5z7ijnCvrvLRP2iftk/ZNWe3j
QaTV+DJb3eOO5buyaEyXusRP4ifxk/hNWfGb2MBv0kc9JX4SP53yK2tcTZ3hZGF7rrDGBdgm
p3CWlXfVCS76xznNJq159Af7FU1R1EXGS7px+pGurJvgFGdVVampTWPPO2bd1KS8ursyCcLa
KJOikhRNVbuzmlk3S6oGl4mbzODUahuV49p6nGXFdeI459q6irTMcO4zqUyT2DOyWbc0uOA+
wy0KuIXDRVV5nTclEnkBeZtYV1lTZ5hsg6vM6VrpJgdb1Z0OuG+BCyfpmgInuNMmw+IudKdD
UeGXYUwa6ym/3z/qWeuw57Qd0U10ZKqRn0Z+VpQlfsbueCRdXNpV1HjOf1WnjZX8pJubErsj
uM4KOw0SvzzJqroo3N16RYUL3bz4TZ1TfpMXPxKg6tYJ7umsysKYpi5aIcXlfLgFNsMealLb
3YCJboQV9/wcWpX4SfwkfjrsOWUPe67mc37cIYLSYe8HV7RX2AfCLpHED0tgOgi2xE/iJ/GT
+A1I/Nb8Yc+JiV+rYU2NW6FynEnA0f7Jj/wkftNB+DgPEj+Jn8RP4jdlxW9iF7zonN90EaxB
zofET+In8ZP4DUj8ZsI5P438BilAz2dbEj+Jn8RP4jcg8Vvzhz018pse59+eDxGU+En8JH4S
vykrfqv5nJ/u85smF7esSlwlfhI/iZ/Eb0Dip8OeutVh6oxEJX4SP4mfxG/Kit/ERn6TvuBF
Iz+N/PSEFz3hxWqk3mWrm9xn+E3uuuBlVYcQp6JPIz+N/DTy08hPI79Vv8tWIz+N/DTy08hP
Iz893gzbAZP/gZHfTLjaU483m4qjvFX1WSM/jfw08tPIb8qO/CZ2q4Oe8LKqjf9M90n8JH4S
P4nfNBe/SV/womd76rCnDnvqsKcOe+qw53Md9oz1VgeN/Gb6KG9V86+Rn0Z+Gvlp5DfNR34S
v1Vt/Ge6T+In8ZP4SfwGJH6xXvAyafHT1Z467KnDnjrsqcOeOuw5VQ976pzfTB/lrWr+NfLT
yE8jP438BjTy0zk/Pd5Mjzdr8ObjLEmaJuERB0hsllZ5VeYmL4uMz0igK0+bpsjKtK6Sxrmq
JKurqsyyp6PyxJRNVTVJk2RtUJ7VTVUgtUyS3LmqxlRNgXdVJqlzFSYrK2PYdun6UKBuCsTk
pZteaQqJn8RP4jfNxU8jv1WNfGa6TyM/iZ/ET+I3zcVP5/xmutCtav4lfhI/iZ/Eb0DiF+sF
Lxr5rWrjP9N9Ej+Jn8RP4jcg8dM5P53z0zk/nfPjWc2mKOoiy/IcZza5U5xm3QTnOKuqSk1t
GnviMeumJi0MvCZBWBtlUlSSoqlqd1oz62ZJ1aR5aTKT5i4xTxrT5Hmalk1jz6Nm3SItM5z8
TCrTJNzdxRRL02RVhtcx1CZ1UVVe502JxMS0Z1uzbl1lTZ1hsk2e2K7aU6crfWRdvdVBb3X4
A8/2jFX8Bjny07M9p8uIUSM/jfw08tPIb8qO/Lg7V3eTukmStM6LOjUZlQ4uXDRX1XVeYV+x
mfQ5vzaxzg0u4GsqU5qqlvhJ/PIqt0ML08V1lg2usyzAstxdamk08tPIL61w6W3lSILLc6s8
ydMqTdvhreliGGvqJOMIN3MX8qY1LgDGeDk3VWaplHablFf2Jhj45gkHFmnaLbElSpMCdEva
C3nTbp6ldY3xboFxsR3epl2T1EWBIW+WFLVtK+li+5Vg2F1WRTsGTroVLgXG6DzJcbmwHXUn
3TKBp6zSCn1xedj2YSyOq4wxYtbI7w+M/GI95zdI8SO9qm6dGJNVZWFMUxc8ElN1cTF7gevU
cXgmqVMuiekiEtN1PjTy08hPIz+J3zQf+Q3ysKfEb7qIocRP4ifxk/hJ/Fb9MttVHPaU+En8
dNjT5BTOsrKHy0wXh93y1OAu/gZH4Hh8The86LBnhUOuuLapxJMbeGyswXFWHK8FQZosb4/s
Nt2ySMo6zwyOltUZmdPguqWqNLhMqkgQzWOvTTfDkd6kKKsqw0FZHnttcL4hyXGVEh/lgIc3
WFeKI71NbbK6yAt7LVPTxSMdcJkUDkHjG3tIuO42OKyc4uhlhkPCJRPrKSt+XBLPfc5PI7/p
IliDnA+N/DTy08hPI79pLn6DPOenC14GKUDPZ1sSP4mfxE/iJ/HTYc8Zd4GOxE/iJ/GT+A1I
/KbO1Z7tBZoN75rFlb0NHh9cupN5uHizwOFnXHXcPhQYV3b23+mgU37P52BtkNOW9kn7pH3S
vgFpX6z3uA/yqKfEb5AC9Hy2JfGT+En8JH5TVvwoRbreRbcUTkZEJX4SP4mfxG/Kip8u9pTw
TUb4mCPxk/hJ/CR+01z8dNhzsgIxnfMkfhI/iZ/Eb8qKnw57auQ3WYGW+En8JH4Svykrfqv5
sGd7c7yu9pyWd0FI/CR+Ej+J35QVv4mN/HTYc7Kjo+mcJ/GT+En8JH4DEr+pc5tfrfv8puVo
LkSsJX4SP4mfxG9A4hfrfX56tGeIKMyUWImfxE/iJ/GT+E34CS96tOd0EUeJn8RP4ifxm7Li
N7Fzfhr5TRfBGuR8SPwkfhI/iZ/Eb8IjP8qtXuQ+SBF6vtqS+En8ZqT42XfdpQler1eWRS31
k/pJ/WbcFTBSP6nfjFQ/7sBL/GbKy2x1r8PzNbyKeboSP4mfxE8jvyk78pvsXe661WHGDfRW
1mFpn7RP2jejtY+DonrGad/k7/PT1Z4ri8hUrUv8JH4SvxktfrwScrqL3yCPekr8pqrYrdxv
iZ/ET+In8ZvmI79Bip+u9lxZRKZqXeIn8ZP4SfymufjpPr+pKlCrs98SP4mfxE/iJ/HTnQ4z
7gIYiZ/ET+I3o8VPF7yUVdqUExY/nfNbnaOxNdm2xE/iJ/Gb0eI3My940Z0OM26gt7KuSvuk
fdI+ad+MO+op7ZP2ma7hjp/VwLQuyySti6wiM6yrysuySSv4eWyErrKs09RkdV7lPrFqmjQz
RZo3ee6imrJqsiRpGp+XpVVelbnJyyKzj9Yw3SxPm6bIyrSu2kdNwVUlWV1VZZY9HZUnBgck
qiZpkqxtPM/qpiqQWiaJm15eNaZqCvQiSZ2rMFlZGcO2S9f3AnVTICYv3QyWppD2SfukfQPS
vljf5qfLXVYe9KjuFM4rncQP6l7WJs0ykyaJyZy6V3kGyU9qyHnudLROmsrkFM6y8q46yVMD
dW/Smm81Q1tNgYdGZlmeQ+K5XUizbgKxr6oqNbVprAJn3dSkhYHXJAhro0yKSlI0Ve30Petm
SdWkeWnQtdwl5kljsL+RoheN3aHIukVaYtelSCrTJLb3Wbc0TVZlVZVgxlxUldd5UyIxMe1u
R9atq6ypM0y2yRPbVbsPsdJH1kUzRZmlBabY7tZkXcw0JoodksYUfiarojZ1WmFPpPLLEDOT
YwFVadrOpOliZkydZJzPzO3XpDX2h7DUclNldtppF7te2NFJMPt5Yhdr2i2xZ5UmBfa1kna/
Ju3mGRY65rrA0rEzmXZNUhcFZhzP76ptW0m3aaoEC7+sinZJ6MGeWJtcQdP9Lj/OY9Vtauwd
5/hJgfa6xX1jjfw08oN0FByAuu2vxE/iV9S4AqKCEDvRzE2J3REcccBOA692wBNBDbU3bUCb
qpX8pItdEQMNbtIytQcpmi72OiC82M8pcTiDeywNHqMN1YZQN1ne6nvTLYukrPPMlEldZ9T3
BvswVWmwy1QkiGYnmm4GvYdUVVWG3rETTddUSY49Fh7fwBEN60qh902NAzNFXtj9mqaLHTbs
MmFHBN/YHYO622DnIs2TLJspD/aU+Gmk9/tib49t4mdjS438NPLTyA9H+CV+HAxWOQfrkEnq
Ow9J1BhzJyaHalYYVDfcW6y7BYbReQEZxjg+XfPvcecwv+5iIJfghE1e1Dgj0w5lIe1FVePs
DA6UNOz9pEZ+rWpiBwYHG3CspzTYJbJt1Qn2dKqyMKapC+7XVF2c1cFRkQyHZxIc9YBLghP3
MpD46ZyfPRyrw57GHnJOuhI/w4GlxA8H4O1Rdby6T+I3HYVc4ifxk/jpgpcBXfCy5kd+rU4/
18hv0oc9NfKbxiNYiZ/ET+In8Ztx4tceqWx4+VjYHe466jldBoHSPmmftE/aN+O0b/IXe0r8
JH66zU93OljZ1J0O9v4OXez5vFzvspqPerYXyuiU37S8dkcjP438NPLTyE8jvwk/2FMjP438
NPLTyE8jP93m9zzf6aCRX9x3E8QslBr5aeSnkZ9GfgMa+fEAcN3F3f+mhCjigSq4O6514eGG
eNZOhlsCS3d/IJ97lODJRk2Ox+20dxGaCs8e5MOO8JChopU1PHEIDzu0TyLCE4psW3hqENpo
8EDDpHKu1Xaxpw576mJPPdpTTzezGqmnm3EDrAe8RHOP+8RGfq2GDebpZjrsGfNoLqRvGvlp
5KeRn0Z+Axr5Tbvb/DTy08hPIz+N/DTy06M943u6mUZ+OucXMtrrj9XITyM/jfw08pvmI79J
H/ZcxQNeKLd44Jke7Tnlb3+Q+En8JH4Sv2kufpN+upkOe+qwpw576rCnDnvqsGd8hz15+clq
fKmDxE/iJ/GT+En8JH7xid/Ezvlp5Nd/rkt2e55Uhz112FOHPXXYc8oe9pzYyG+Q4qdzftNF
PCV+Ej+Jn8RvMuLHF8xPkXfZSvymi2ANcj4kfhK/GSl+CZ88gpvVK7yvtKilfpNRvyje5D6x
456TvtxTJ/100k8n/XTSz4qkHvHCra0e8TLFHvEyyKGfHvEyyOHX89mWhn4a+s3IoR83YRr5
ZUlRUhjqaT7ym7T4tYl6p9GUv6lvVSIr8ZP4Sfx02FPip3caTUuBW5XoeZ/ET+In8ZP4TXPx
0zk/v8FX+czz4CR+Ej+Jn8RvmovfpA976oIXXfCiC150wYvVSF3wogte8iSrptgFLxr5acT3
zIjPLwuN/DTy08hPIz+N/HTOT+f8krQuMvv+ZauLVV6WTVpp5KeRn0Z+er7ZVH2+mUZ+frSj
8pkRoEZ+Gvlp5KeR34BGfpW9bSJvclMWVYFXp5d2P7ru5mmVZ1WWFWleNu3d8VmeF0lhyiYv
0pTqVHdNVWQGrjRPqqK9fd0kGJJlaYIyqVtXmldoo6kak1TOldRNgt32vKhTk7X3biSYWFXX
eZXmTaNzfhK9Z0TPLwuJn8RP4ifxG5D4TZ1XufMJP1W3yQzUuEqbUkc9ddRTRz1rk2b4SSRJ
uwuJvQPss5Y66qmjnjrqGd9Rz9X8YGvd466LPXXKT+In8ZP4PZf4xXrUc9Kn/CR+Ej+Jn8RP
4ifxm6rip1N+/jSXymdO/emUn0756ZSfTvlN81N+kx75tYm/82hPXnRTdevEmKwqC2OaumjP
H1ZlXpRZhnOISZ1yDCyhiXsZSPwkfhI/id+UFb/VfM5vFeKnlzpMF1GX+En8JH4SvwGJ35o/
5zcx8RvkyE/iJ/HLq5xH0qmeVdOkuD0H99PkfLszXQ3u78mSpGkS8g6eDPf54LiAycsiI33o
ylPcgJOVaV21rxaFq0qyusJ9PdnTUXmCO4GqqsFtPrw9CHl5Vje4h6gpyiRx08txz0/VFOhF
kjpXYbKyMoZtl64PBeoGNxIluNWobao0hcQPCzXr1lXW1FmKu6lwixUXjl2MK31kXT3dTE83
+wNPN1vz4tfe+afb/KaLIK3J+aBQFUMd/C1bsRaLzrIF/Hxq5b/fPsXvVhAb9X3PWP7NAvpT
2naWrXjK5tmQ3/tYz+X4L3belxan34JtEr5uzQl9HN/BdNc9uXN1Z3HnhZ3L8bmEHmLTqzoX
dC7qnA/vBZ3L8M35naRTdKpO08lgIWIDH7GS37fAcnbPR89dijYuRCuryupiuhehF27aW5yA
qCvguabzYnjTlabd7byoc2XnEh+9crlVD60twfecHqd2TecFnUs7S+FZ0vnNU5fik3N0Jb7H
9Ob42lLfzuzrO9d3hlhby5XrXouMq7CErkBbNm7TvGMQU3VyfKZYHklfWfiWYilnL8VSfHrN
DqxXs2xLm3Zmr4Jrs1bh63f577fpd8L+EX9V7/joeVuM/e4X1t/pJC93/p8x7nn9OwBTnxvQ
gwcR2wPuAebYvLGxO2zZbi3w611xNeruNzDh0jbhPpj7XH+bPVfAs3w/Zx1+4dfbaX1RR1n7
me1R/3ao2xdnzZ1WdqA+C3/tIkFl9rLO0Fqc+w2uxq/u8pV++2OIKAD+cbvo/2Z31urMWTZr
k5aTY3CX7qv+qFlPr7GJ8ico7ufHv+Z9K3yPVl227W1uv/zOPp3OobBeDlwx9/bdL733svE9
b//u/H95zw7j3v6rr3zl0fzzs8a33Wnt+ftsPX/8/qMvGf/bP//a/N/ed+o4sfW+D8/f/tPf
fJS4//0Pz7v7rruG++JHfDzaHPFtbvCtd++xw0H/+J6DFy3eE3nDPhftjfg2ETvCTrI/tNkn
2mh7hH1if9D2CPvE/tDPaff5R+h3uSPMddMaZj/dtEbYfzdfNp5ts92+ebQx9N/y3e8Nl7t+
bh77y7b8/Ho/p+9z0Sbn3bbj5t32Acv53exT33K2NmLH/bzQ5vTYB7T9KG1OlzanQZsxtBnj
cv38jnN6brmN9y1D+sf7pjuO9TDM79Efa7t+Wvv0p+aNbHTqJdb264Xx8I3gO+v364V+2mzL
22yrL97afpnT79q3fjdda7v+eD956HMt31zuuO8by77+2Hl0fbDLwdu+b+QX+0G/y7U22+C8
0f+zRW97FBjusx91tv2uz7YxbJvbJe6XEbSpSbRZru3ATYyPoc0NGut2w4aSf7TXtVZbcuux
PrABwByCNuNYbuhs1mkzl/t9GwObONDe1NksGUcw38fQ5paZdZZsg6DNrQVtllQc9mcLgDkE
bcax3NLZrNNmzlbA1gC1lqC9rbNZbudAe3tns+R0CNpsm6DNdgnaOzib5Y4OtLmZJ2jv7ECb
02ad5S4OtH0fGcN+ELQ5jSFgV8CvR9q7uTpLv15o7+7qLH3/aft5pO2XA+09XJ3lng6093Kg
vbcDbU6bdZbYfFvQHgJYMob9IGhzGrMA/u3rQHs/B9rkGOss93egfYADbfKKdZYHOtAmj1hn
SW7RZkndJWiTf7RZHuRK8ok2QTtxoE2Osc4ydaBtHGiTV6yzzBxokxessyQfaLPMHWiTF6yz
pJazJCdoE7RLB9rkCessK2AIWBuoHWjPdjbLxoE2lz3rLLn8mTMPGHKgvY8D7fkA1z3X8bAD
7REH2oxnnSXjyV1yatSBNrnEOssFDrTZNuss2T5jxgC2QdDmfBK0Ob+cd5Y9B9pjzmbpp8t2
fQxtts86S/aXNsuDHWiz/6yz9Pyk7Zchbb+caXMZMY589e3QPsTVWfo+0F7o6iz9OqXN9UzQ
9tyg7blE2/ONtuchbc9V2pwG6yw9n2nzd8Q6S/9boM3fB0Gbvyf2nTZzDgP6//7tTzf81Bd+
WS1/6Bs3rVh47f/M33nrkeU7vOGmFU9+7GXDc3c6fPnyLW9a8T+HbDT+lit/Pf6y//+WFZ+5
YadHHv7Nf42fseetKy6/+bhHVvxnm2vmvu1TP7tiyfK5W92w4uZX/PpT535xbHzBX7x0RT52
1vBRx85d/uUzb1nxwIr7H/3Lxw+zbf7mlxVXaYfT/fu5I6NzH+oMc7pH/eCw0b97/PXDnO4J
J/1q5OEtt7TTPW6D/+aq7HC6v/lFNbrtvfs/wty/vHKJbYfT/djPx2wMp3vyyXNHzf6nDXO6
rs1HbZudbed//NzzRz/8jRtWPNibPfzEffuNDr/o5hVbbvuVRy97y3qj73vnLStOLDeb/9WP
fm9k3tW3rvjhB86Y/4Prx0bY5jc/9sAj2VvvHPnI0peuOO6E/5p//qyh0T3/z80rfnPUex/p
/mnbztvnfnLeu65YMsr+/PVu+zSXfrb133Le+cufuHzt+Zzuj+/Zb/kZ/zxnmNP9u5+vt/yx
zcYf5XS/+PD3xkce+dd5nO6nx8bGf/zD2+ZzusuPuHP80U98/RFO95tzhpb/8vx/nc/p7vuh
/ZZnG338EbYzfuWS5cetfUbD6Z7x2f2Wf3G39zf0v/G+/R/5/FMvXcFld+Meh44+Vdxk7U9/
9vBRLg/6/6HZZEH67VOs/ZGbTllw4Rc2sfbGv7hxwUcvPmo5YxC7ADnWbsc+9GIkV9y0gO3S
djHWRnsL2C79aG8B26WN9kbZLm3XB2uz7ttlX5C7gh72BbnWZl+Qa232xfefpe8b5w/98f20
sWyH7bFPtNke+0Sb7bFPtF071nbt2xi2x/lkzDN/yxbMQmUtYDawNjAHoG8dgLpFTaNvfWAD
YEOA2kON2gTYFKBvM4C6Qs2hbwuA2sJt5dYAt7XcV9gO2B7YAdgR4Pc7rQI7w0fsAgwBuwK7
AbsDewB+G83vua1fGV4r/LbSl347wm0K4bcz3PZwO+S3Wb7k9ozbN7+989tAbhP99p7beQ9u
g/022esUfX7bzhXTD66QMYceSm6r6eN2jtvNQ58nXIjpfhHw45X3vvkzdrv0+K/+eGSDt35r
uHva10eOeOUX5m157z+PjM55bP5dN/3JyIr91xp56Mh97fdf/T9HDvP79TBOQDO2Hba1HDGM
S5DDPP8dS44X1kPba+2/7sjn33rSKEvkjNJ/SmfJ6NfQ5ui9l4wyj3EP/PuDI2OYBvvCfPaR
7d+Nvly/zrGjLBm/FfrI9hjP6bJ+4sWzRxdc8eORq/9oW1s+eu+TI/Sz/sLOR0YeOnkbm//U
6CG2vsmBZpT9Z515X/7FIlu+Yusz4f/JSPv9T0Zef8iGtn7vn/1shP1lyflg++x3vvnW7Xxh
GvRzOlwe9LN/l8LPksuT/efyZb84TfrZni8535w255sl+8eSy4u+425sjwmwZJ1+xtjlDJt+
rh/W33H6Ubbkerv0w1+bz+VEP8szmofnsx+ss2TdThtxSw/7uvVzOfN7lvyey4ft/PTfFlk/
lxOnx5JxXF6ss2Sdy411lqxz/TCfy43tsaS/e/ls+72fVz/vyflvG0kB9ufWq388cgtwNWz6
r7hoZ+sfn/f5efS/H/N6OXz0s2QelwOXHZcD85chlvksGU8/88kzbh/XcqDNbSfrfhvqt6M+
httPbk9ZZ+n//DaWdb+t9dtZ5hDc5jLOb3tpE9zmMmflbbHfDnMb7LfHjGU+t9cEbW6fabNk
G4TfZtP22272h9tv5hC0Gde/PWed23Tm+O2636ZzG8/tOOt+e85tNu0hgDbLXR1os22CNjWD
oL2bs1lSBwja1AOC9p4OtDlt1lnu5UDb95Ex7AdBewigjlA7vF7Q3g/gOt0f4Do5AKCP2kGb
JfvPZeV1hPNFP+ebWkI/tYT1fj2h7TWFNnWFoM1p02ZJrSFo+z4yhv0gaHN61KF+DaJN0hK0
ucGlzXLYgfaIA+1RZ7OkFhG0x4AecDBwiLNZLnSgzemzzpI6uLr7cyimcRhwOECb5REOtI90
NsujXP1oZ7NO+xgH2sc6m+VxwPHACcCJQOi8M+ckgG0QtNkuQZvts1+T7U/ovE+kPyejP6cA
pzrQPs3ZLP1+0enOxzja5DBtluQsbZZnONAmf1lnOcuB9pkOtPk7I2ifBTCOf74d2me7OktO
h6B9jrNZcj4I2uc60D7Pgfb2DrTPd6C9lQNtbgsJ2pwGbZYbO9Bez9ksFznQ3tCB9gUA/2gz
h39+3vi77OAcMetrWdt/t4w/vad93Pb4uNmwGM9lTx/zvK9tY9kC1rksWecy8nHex+/pY51t
s85tiY/zPn5PH+vUHta5rfNx3uf7x2/o8/GMY31d5+dyoY+f3seSPpZcRiy5TfJx3sdtF32c
/gYA/VsC9HF63uf7Rx9txh0AMI59YZxvgz7W2S+W1E4f532+z+wXbcLOAHLJCfKB5UKAuaxv
Avjv6KPtfZvD9nGcHuMPpgtxjPE+2vRxevSxPgZ4H+s+nj7239e5L+B9tAlymz7GeJ/vC/tH
H+tzAcb117dxPsb5GGo/4/rrRzof49gOYw5zPi5z1rnOqIW+f97n+8fp0sf61gDjfAzrOzsf
49gWfb5/7At9rB8NMNe3sy1qezqfz6GP41Ifxzz6FgH0Mc7H7OV8PoZ53I4wzsewvoPzMc7H
dJ2PcT5mb+fzMczb0fm4rBjHul9W9DGWvgMBTpfLhXGM8cuF808f67sAjPPTZN1Pl3GcJn1D
AON8H1jflS74GMdpDgHHAD6O02TMbnQhzveVvuOcj+2xH4zZ3fl8X+k7wfm4nBnLGL+c6WMu
fXsAnAZ97C/rfl36+aSP2so4rnPGMeZigD4ue06D7ftlMASb/d0HKADGrY1P79u3zzcEm3Gn
OJ+fd8aUzsdczhd9+zkft0P0sb6/8/nlwXrlfIzjvNJ3gPNxndPHul/n5AB9rHtekWv0sX4Q
wPlgncuEdT8NxnlfAptxrHM5sZ4C9DHO+y5wPsZx2THGOB9jvO8Fzsc4Ll/GZM7nlzl95zgf
lx9jGeOXH33MpS8H2Bf6uNxZ9+uIMd53HmzGDeHTr8ez6IKPy5nTYPt+GcC066dG2bCCuFn4
5Dqj7wyAPn5ynTFmHivw+fVK39XOtx5KxjFmfp+P65H1Yefz65++O52PuVy3jBlxPr/+6bvD
+dZFyTjGjPb5yAHWbWfRP88T+nzuhrAZx5gxgPNBPaFvDOgB3kf+sH4wXYjzHKPvdufbGCXj
GHNIn488Y32h83ku0neb822EknGMObTPR+6xfpjzMcb7ljnfXOdjzOF9PvKR9SOcz/OYvlud
j7nkHmOOdD7PY/pucb7NUTKOMUf1+chH1o92PsZ4383Ot6XzMeYY59vR+Vg/ts9HLrN+nPN5
vtN3k/NxO8k4xhzf5+NvgPUTnI8x3nej8+3sfIw5sc/H3wHrJzkf87zvBufjdpM+xpzc5+Pv
h/VLnM//pui71PnWRsnf0CnAqc43hNL7znS+2c7HmNP6fPxdsX668zHP+65yPv5W6WOM/63y
d0kf6y8ByF3m8jd5JrAUoG8In953Fl3w7eN8rJ9NF3yM4e+UdZ/LOO87Hzbj9sYnf6fnAOcC
9HFb530XOR/j+NtlzHnOxxjvu8z5OA36GOOnwWnSx/oVAKexDT5HgUXABQB9W+HT+xY7357O
x5gL+3wLXP0Fzsc873ux83E+6GOMnw/2mT7WlwCcLnPHAE7zRYDvyxgs+i4G6NsFn2MA655D
5BR9rL8QYBx93N6QU95Hrnnf9bAZN4ZP+hjjp8u+0Me6nw/2lz7WfZ85H/Sx7pc9lzF9rF8O
cBr0HQyw7pc9Y7zvWtiM4zqijzFXAvSRk/Sz7jlJH+PouxpgHHnLOMZ4jpO79LHu+bcfbOYy
7xqAufQdArB+J0AfY7zP9499po/16wDGsb4QYP2lAH2M8z6/nLns6WP9BoBxBT7pY/1GgD5u
h+hj/SaAvgyf9LF+M0CfwSd9rN8C0Jfikz7WbwXoS/BJH+u+f/Sx36wvAxh3ED7pWwa8DKBv
f3zSx7pfLvQxlr7bAB/XdfXb+3wHwmb9Dueb9avv/ua7K576x6d+gyvDDzr0W+3ne379rV+c
/6WXjjz1nkef/O75X3rzU7+5d7fe0E6doSPnrv2vbmxqG+ic+dO7x8786fpcvJ27Whc+g65c
fDrr2Y3w9nbsa2wWbOLZ/9bBV1852CCI13HaK0A7Y/DxF8u/9drCfsZ1Hefp+CFzO/HXwOde
8OLx9x60YOSYRd+ef+8HzxwHRn5VPfK0zXMN+H4ccTbm37ZZMP72y15sz0Fct3yX8V//8UtG
dr/48fneZjy+H0ecjcH34/jOxnibMc4eZy5tLiZvsy0fQ39fH8b7+jne108b7+bFxrg+WL/r
s7VdP+10vc322Uf2g33gNZfe9n7GsC/099l2vpx/pK8d63e51s/l4Zcbl7dfnlzeBHO9zfni
9369MK9veY6wXbesrM1c9Atr9ellaG3vR7ydL8bQpt+1aW03Lb9s2R/rd/2xy9n12ca4ebEx
nCb/2OaGxSXjwMicV39t/nb7XYZrUo8ZyZf/0/w/Hb9xfGzp0SN/c+GT89/17WXjXL5PfGv2
sPOP0+/ixxnv2hlnO4x//Ff7jjPe2SO00d4485n7gSuOHumtuHH8fxY/SZnoMI4xzPM2+8V2
2Sb8I96PNkZ831yM7T++H2Gcm+6I77Pz2/Zdru0D5nUc82Dn1/XNzq/rj23H9cfb7IO1OX22
xXnhMvPtfCl7rZ33fz+xHvnPv797/PTPnjpOe/QHN44TtOnjd7TZPnNoXzF39ru9zfnwNuJt
W64d2xZttGHboo1Y25a3OQ/eZlvOZt+etn2M65v1uz5b2/XT2q6f3rbTY5tsg9OmjXYsaLs+
W7/rp7UvfNP4o8AwY5z9qLOHWe+zbQzb5zZ9LQfas53Ncm0H2nOczZJbeuasC/g/2tzCE7TX
BzYANgQ2cqC9sQNtxrLOkvGbAJsCmznQ3tzZLOc60GbbrLNk+8zZAmAbBO0tHWhz/3drYBtg
Wwfa2znQZjzrLBnPed0e4PwStHdwoE19ZJ3lTg60d3agvYuzWQ450N7V2Sx3czbL3R1o7+Fs
lnu6+l7OZp323g6093E2S+5LErS5H0jQ5n4ObZYHONDmPg3rLLvOZsl9IoI2lx9tllyGXM9c
Llx3BG3ug9Fm6dc1bc8B2ly2rLPkumE75BPzCdrkHm0uX+YQtLmcabPkMiBo++VGe8iBNtcF
Y7icfDu0uWxYZ+n5QNvPL22/fGhzmTGO/PDt0PbzsBlsP4+0yc1ZAP+4/0rwj/u3tFlmDrTX
czZL/jb4R9vH0cd9aIL2Bs5mWTjQ5v446yy550XQ3tSBNn8/BG2fX8P27Tew2Tfm8Lfk26E9
z4E2fyess+TvZ2tgvrNZpz3s6ixHAMaQS/yOoD3qQJv8o38B4HM4Dba3F8DfwpgDbf5OWGfZ
c6DN39XBwCHAmANttsFyobNZp32oq7Pk74Sgzd8GQZv9pM2S/ZwNHAbMcaB9uLNZHuFA+0iA
8eQE4wja5AJtlow7Cjga8Lm0ua1hnSWnxfk8BuB3BG1ua2izZBznn9sZxhK0GceSMbSPBbje
j3OgTe6wzvJ4B9rkAOssuT5oszzBgTbXL+ssT3Ql1yFtgvZJDrS5jllnebIrue5pE7RPcaDN
5c46y1MdaHPdsM7yNAfaXK+sszzdlVz3tAnaZzjQJl9YZ3kmwN9BDpzlQPtsB9pcXqyz5LLk
+uN6PMeBNn9HrLM814E222adJdtnzHkA2yBokzME7fMBcoM8WORA+wIH2oxlnSXjxwCu+wsd
aJMjrLN8gQNtts06y0UAYy4CxhxoH+xAm8uH/WffFzvQ5vJgneXFDrS5fFhn6flGDvkY2uQO
6yw9Z8gPH0P7Eldn6adL+1JXZ+mXCe1FDrT9/NLm/BG0OT8Ebc4XQdtzgzanwTpLzx/anm+0
PSdpk6cEbXKZoM15YP+4fnz/aXMds87S84fLlz4uj/6//uuY+69vdtccr2Bs//XQE7nWuf86
5v7rm3HdMK+NHmWb/ddDT+Ra5/7rs901x7Zv/dc6918D3X9t9ESue+6/prn/Wuf+a6D7r42e
wHXPK9795ouWm83vbn5x9w2/c91595vXLr/v1HPn77T0+hWbf+fa5bO3OHwe7S9fc8Pyzz15
yby7jnza/yn6X/zgRcs/c8X289nO4++7dfln/va+eZv/13Urss3X/+QHMQ36X3boqz715fe+
ZPn/fOb6FQ++eemn/vXb1y5n7k/u2+SRDy69YTnbfN1u+SOjb2jjv/CP6zxyyntvXc52LvjO
tXadMH7J+15ibbbz/jdcNPoQ7h9g+/e8/1brZ3x17Q3WZptvffdLRlcghvEffvNF1s/4/uv7
//u0f5z3jX+4dpTtf+/Jx5sdkc/c7/zt3HmL0W7fvIwy9+Od3edv9OBF1nbzYnMP3uk184/5
u7adD9583Yr95i9c/l8vPHD5nK+euGLXoY1W0H7thzda8c4rT7T2vd8+bPnOZ19n7etPHHrk
JwfdvOKgTZLlrzrrkNHPvaL13/6zDRd8+T/a+KM/euKCNxzftvPql1y3YLcdDrXtDyU3LyBn
mbtLgjbmPtzQ7mCaO3z1xAWc7qswzY98eCNrb41pdr9z2Kjtz7yFy//s5uus/6C5ecO2mHvn
pict+KfHNrT+vV660YIr72nb+dCvDh09/eI2/hv3Xbfg+zccbNvh9Nu/Z67hWQuO2cDawCxg
DrAOsO5KWA/19R02QLkhQN9GwMbAJithU9T7sRnqmwNzHbZASWwJbAVwP6wf26C+LbCdw/Yo
iR2AHYGdVjN2Rvu7AEPArg6s79YH+ncH9gB8/J6wib2AvR32QUns6+D9+6G+v8MBKA906KI8
CEgcaPN76jdhgAyg5hdACVQAdb9xdfqJeQDjCMYwj5jvMIySGHHgj48gWfsxhjrRczgYJXGI
w0KU/TgU9X4chvrhDkegJOjjvgFBne8H9wG4T0hQown6+rX6eNTXNN6OaRazsG6Wfmr4jKXL
5r3lqju5+Dos3zz0ouFmw1+N+JL+Lb/8kxHGPfjYT6z/S1v908jNP//oPJaMG3rrp2zeCec+
OUw/S/pfV77WxrFk/bTb9hxlO4d8f2eung5L+u9/xZ62/NU5B44ynyX95fAttv7gMafaknX6
WWf5ue/c+XTJ9sZffZttf+dX3mb9H3ti1ij7zH7uffvs0c/fOXv01Zv90wj7c2L62hHWfXna
EU8OM+4N399vmDnf+8UhdjlwWbDOtpjHdjh/LO/ZaP9htsdYxnD5MZ7Lg/H8nu2zZPvMY/v8
njl2eSOH9i7wsX1+b5c//GyDfi4n+v7qmu1HuS6Sl+0w+tEfdkavWWv70b94wxMjf/m2rUd/
/h+/GNnu+9va+WPJ6e78z1vaknVOn3Gf/O47h5n3gf3fPrzTF+fY+osXr2XrbHOtr58yzPZZ
2vWDfnC6XXCF7V3zVz+w5aEH/csI+/J3Oy0c5rS7H1pn+OEn3jnMkvPxyfd8Y/7t+b/Ykjxj
XAdtst0l3//BML9PEMvcr+I7tsXv2YfH8B3bZ8n5YMnpMp79Zzz7Qz5t8fNZo4u3222U80De
cL08fsVuo5w38uTTL1939O1/tZ8t7/vyS235xFZ3PP29XZ+veYVdnj9ccIdthzyjn/ziciev
OB2285qfDo2w/PHHtp1/7Ld3sXVOb8n6T8477P6tbZ3L73W/7s1709fm2DrniXXOK+P22u7J
EbbD5cN2WLLO5cY6S9a5nFhnyTqXL/O/d/xrbJ3Li+1eOWcdW+f8MZ7zzZJ15rHO8jOzX2nL
EzC/zONyYHs/P+9O6/8Eli3r983ZaPRHWzw58rNsk1GuhwfeND7yeoB1ro+2PmLrXC+Mf3ze
a4Y5v5eiL5y/69+woZ0v/i45PywfeNMI2hlBPstxO79sk/PHkvPFtjg/b0Rby9AG+8Fc9oMl
p8+S0+X3nC7jOV3mc7psjzFcrmyX/WG77B/b5XfY/HXWAvx+wxxns+S+A0Gb+xC0Wa4HMIf7
EP6PNvclCNrcp2DsRgDjCdrcvyBoM5Y2S8Zzv2NTgPsXof3x+yR+36V//4T2qvZPuK/CfROC
NvdnaLNkfGj/OQ9+/v3ygOvp5cRlRvCPy93vE3FfiLbfJ+J+EW3uT9Fmyf0pluyn37d6rv5z
HjgvnH+/PLh8aLPkMiP8cg/tz47I3QnY2YE296tYZznkQHtXB9q7OZsl97nYDve7mE/Q3tPZ
e6FkDkF7b2ez3MeB9r4OtPdzoL0/wLgDAN8O7QNdnWXXgTb3zwjaiQPtFGAc99d8O7T9PHA/
zM8jbe6jFYDfn+P+Gm3u19Fmyf07gjb37Wiz5P4cY2n7OPr4YyZojzibJX/IBO0FwBjQAw4G
uE9Hn9+fo32oA22ffxhs3/7hsNkXzscRANshaB/pQHs3Z7PksuDyOcrZrNM+2tVZHgMw5liA
3xG0j3OgzWVOP/cFfQ6nyfa43rguT3CgfaKzWZ7kQHs/4GTgFMDH02YbLE91Nuu0T3N1llzf
BO3THWizn6yzZD/PAM4EznKgfbazWZ7jQPtcgPHkBOMI2uQCbZaMOw84H/C5tBe5OktO6wLg
QoDfEbRf4GyWi4CLgMUAYwnajGPJGNoXA5cAlzrQfqGzWb7IgfaLgSXAZcDlzmZ5hQPtK53N
8iWufpWzWae91IH21c5meY2rX+ts1mlf50D7emezvAFY3f25EdO4CbjZgfYtDrS5vFhnyWXp
lxOX263AS4Flzmb5MgfabJt1lmyfOVwPbIOgzXYJ2mw/tD+3Iccvq9D+cPly2bMNgjbXE0Gb
6+d24A7gTgfaL3c2y1c40L7L2Szvdnil8zGO9qtcneWrHV7jfIyh/VpXZ+mnS/t1rs7yHgfa
9zrQvs+B9h850L7fgfbrHWg/4ECb02Cd5RscaD/oQPuNDrTf5ED7zQ60OQ/s31sA33/ab3V1
lm9z4PJlDP9mtYXdBoNVk7pvi+uOuWvhczbANmnTx/ragP/Ox3lfxTAXNwcW4/k7p48x3keb
PtbXAVjfFvBx3ufb4/TWBRhfAozjp/cxnj7W1wNYp+3jvO9Y5+N36wMsE+djjPdt6HwboKTN
7453PtY3cj7GcxqM877NnI9xGwOM4feMY4z3UTfpY9uMZcwxgPcxzk+fPrZDH2MNQN8m+NwU
YLtnAPSxzj74afk479ucYS6ONts8hS74GON9bJs+1ucCflo+zvsOZxji2FfGcvqnAt7HON8n
+tgv+jgtn0t7C4D5hwGM4/S8j/H0sb4lwDptH+d9Zzkfv9sKYFk4H2O8bxvn2xolbX53jvOx
Ti76eE6Dcd53UF/cdrDZJr9nHGO8b6HzsR22yZiz+3yM89NnLtuhj7GHAvSR79sDbPcGgD5y
2/sYTx/rOwCs0/Zx3lc7H7/bEWB5s/MxxvtoM5f1nQD/HX20va+B7eN2huXj6WOM940wzLW3
Cyx+R72jjzHeR5s+1ocA/52P8z7fHuN2BVjeAjBuCJ/eR5s+1ncDhoBLAB/nffyePtZ3B3y8
j/O+YYa5uD1gMX4xXfAxxvto08f6noD/zsd533yGubi9YDH+IrrgY4z30aaP9b0B/52P875R
hrm4fWAxfgld8DHG+2jTx/q+gP/Ox3nfAoa5uP1g+Xj6GON9hzDMxe0Pi99dRhd8jPE+2vSx
fgDgv/Nx3ufbY9yBAMsrAMYxxvto08d6F2D9AsDHeR+/p491/m59vI/zvoMZhjj+HhlLnA94
H+N8G/Tx90gf0QPoWwef6wIJUALetz4s+lK6XJyv+99lf4xxcRujZBzrmfNt5Hys587H7Qbj
WD/U+RhHP31Fn89vDw9zvrVQst/sb+V8/J2zPfbN/875u6WP9XkA54M+8pF1z2fWGUef5yTj
+DtgjP8d0Tfk6iMo2R65yFzmef6RT/SxPgYwjsue/jHAL3v6GEffQoBxjPHr5+A+H7nCuuca
t5nMZV7/8tsMdS6nwwG2x0+uwyOAI1mBbxY+ve8a52PBdcaYY1lBHGO87yjn8+uV9aOdj3Fc
t/S91fnWQ8lYxvj26GMcfccAnMaG+KSP9eMA7yMHWD+eLsQxxvtOd74NnI8xJ/T5yB3WT3Q+
zyf6TnM+5pI/jDnV+ZjnfSc5n+cY6yf3xZF39N3ufJuiZCxjTunzMY6+M5xvc5SMY0z/dMnb
04CXAZxf9tn73tTnI5c5/w86H5eL973d+TZByelymmf2+chv1s9yPsZ43x3Ot6XzMeZs59vG
+Vh/gfNtjZK/jXOA852Pcd53rvOxzt8P6xc6H+O87zznY52/Kdbvcj7GeZ+fLrdnbJPTXARw
WdHH398i4AKAPsZ432udj9tR+hhzhfMxjj8S9u3Vzse+eN8rnY/LiX1hP17ufHugHAMuAhYD
nO5e+BwD6HshQN9u+BwDGHMx4H09V7/E+cZQet/7nW9X52PMLc53MMpDgEuBB5xvDKX3+enS
x1jGfRjw/WMcY15EF/rH+kKA9fsBH+d9L3Y+1rmtYf0+5+P8et8S59vH+Vi/zPn2dz7WL3c+
rgvmsn6P8zGOfvr8OpoN+zDgSuBqgP2bg0/ve4nzsc7tHuvXOh/jvO8q52P9CID1pc7HOO+7
wfkYx+0hY97lfIzxvvc63yyUnDb7do3zpc7Huu8LfWyT9bcAnI+j8Hk0cB3wQYA+TsP7ru/z
MZZxDznf9igZx5ib+3zMp8/PBznF7euNwK0Ap8E877vJ+RhHP+P+2Pl2RMk4xry0z8c4+vx0
d4HNfHLUT4M+5rLuc2vY1INlwJsB9oW+42gBLwPoY4z3Pex83D7Tx5jb+nzc/rN+u/Mxxvv+
3Pkq52PMHc7H3zTjWL+zz0edYP3lzscY7/u483FbQB9jXtHnO9HV73I+xnjfXzjfsPMx5u4+
H/WE9Vc6H/O87xPOt8D5GPOqPh81hvVXOx/zvO+Lzjff+Rjzmj7fKa7+Wudjnvd9wfn4m6SP
Ma/r853q6vc4H2O87/POd6jzMebePt9prn6f8zHP+z7nfAudjzF/1Oc73dXvdz7med9nnY/b
NfoY8/o+3xmu/oDzMcb7PuN83G7Sx5g39Pmon6x/xPkY432fdr4c5VnAg8Abna/p873D+Rh3
NsCYNzkf87zvT52vdj7G+N8Mfx+MY/3PAP5mUnyeA7wFeCtAH7c33vdO58ucjzFv6/Od6+pv
dz7med9fOR/ngz7GvAPgNNhn+t4BfBSgj7nnAZzmVwDfF+97l/MdiZI+1t/tfKyf7+pfdj7G
ed/7nI/buUXAQ8B7AE6D28hFAH1/AtDHuAsAxrwXoG8RPr1vnC74OA36GOOnwWnSx/qXAMb1
8Hkh8H7gjwH6xvDpfR+iCz5uI+ljzAcA73uBq3/Q+RjjfSucj/NBH2P8fCxyPtaXA2yPuRcB
nOZjgO+L933Y+Q5GSR/rnrtnOh/r/x/AXK7LxQDXo+cf1633eR6Qe/Qx5mMAc+m7GGDdc5Ix
3vcp2Iw71vkY8zBd8B2HT8ax/ucAfcfjkz7WPw7QdwI+6WP9LwD6TsQnfax/AqDvJHzSx/on
Ae+7xNW/6HyM8T7fP/aZPtYfAZjL+qUA638J0Mc473vU+cgV+lj3vKKPsfR5Di2CzTjG+HXJ
9U0f654HXL/0sf4YwOlyPdL3GODXG9clfax/GmDcGfikj3XfZ/o4L6x/BmDc6fikj/XPAvSd
hk/6WP8cQB+3z/Sx/nmAvlPwSR/rXwDoOxmf9LHulzN/R1wGnH//m+bvnD7W/TbiHOdj3XNt
Fu4Bb28Gf/re8LXX/+zmRxw+tNNn/+PxU3/71FMfeeqTv33qyf/47f/i9Tlfe/y6a0b+5j3n
/M0vzvnSex694bxzv/Tmx7+x+UNHzOrct0fvvosesodI0br9u3vJZWNLLv/hGCt3WQ8/wm/5
fjp1lUZ4ezutsp1nc66DL9pbyNuI8Ok9W8uTaW8zJK237NovpbPa7GULXrTn0aNfOnvxKMkx
p7PBstn84ikeeOLtpH9/ZftLOfWOdw3325t9ae58Bvb7eVunj6FNMIbteJv1dhqYBE6C8Duf
g56M73PQOfaXuexzv3h033XvtPapd+z2KOOYC3vY24gZ9jHIHfG5nJZvkznPzNOcDtv9wTe+
OEw/7fN239P28brZt/2OveSuy62fMd7+3bbWYrXj26K96rh1O2h72MfR9tNk/5/N3x/j22Wu
tzk9/7eBN2y52TKu2pVfurVeX8yd//WmMaLPhYWRLmSdt9Ne9vivLHAQa8zX+d2ls7ix52Er
YlGPPkcjmhP4aw9vPRPIdjpj+AeWAe8AHgO+B3DEshkwBCTAGHACwOleCSwD7gLuAR4E3gG8
H/go8AngMeALwFeBvwe+B/wI+BnwS4Cj77WB9YCNgM2ALYFtgR2BIWAPYB/gACABcqAGhoEx
YCFwBHAMcAJwCnAGcA6wCLgIuBRYAlwJXA1cD9wMLANuA+4AXg7cBbwSeDXwWuAe4D7gfuAB
4EHgTcBbgLcB7wDeBTwEvBd4P/AB4E+ADwMfBT4GPAx8HPgE8CngUWA58BjwaeAzwOeALwBf
Ar4C/DXwVeDvgK8D3wT+HvgH4DvAPwHfA74P/AD4IfAj4MfAvwM/BX4G/Bx4Avhv4JfA/wK/
Bn4L8IjILGAtYDawNjAHWAdYF1gPWB/YANgQ2AjYGNgE2BTYDNgcmAtsAWwJbAVsDWwDbAts
B2wP7ADsCOwE7AzsAgwBuwK7AbsDewB7AnsBewP7APsC+wH7AwcABwJd4CAgAVLAABmQAwVQ
AhVQAw0wD5gPDAMjwCjAozpjQA84GDgEWAgcChwGHA4cARwJHAUcDRwDHAscBxwPnACcCJwE
nAycApwKnAacDpwBnAmcBZwNnAOcC5wHnA8sAi4ALgReAFwELAYuBi4BLgVeCLwIeDGwBLgM
uBy4ArgSeAlwFbAUuBq4BrgWuA64HrgBuBG4CbgZuAW4FXgpsOyQzjKg8zKUQOc2lEDndpRA
5w6UQOdOlEDn5SiBzitQAp27UAKdu1ECnVeiBDqvQgl0Xo0S6LwGJdB5LUqg8zqUQOcelEDn
XpRA5z6UQOePUAKd+1ECndejBDoPoAQ6b0AJdB5ECXTeiBLovAkl0HkzSqDzFpRA560ogc7b
UAKdt6MEOu9ACXTeiRLovAsl0Hk3SqDzEEqg8x6UQOe9KIHO+1ACnfejBDp/jBLofAAl0Pkg
SqDzJyiBzodQAp0PowQ6H0EJdD6KEuj8KUqg8zGUQOfPUAL2T9tnbZ/XAhdmA2sDc4B1gHWB
9YD1gQ2ADYGNgI2BTYBNgc2AzYG5wBbAlsBWwNbANsC2wHbA9sAOwI7ATsDOwC7AELArsBuw
O7AHsCewF7A3sA+wL7AfsD9wAHAg0AUOAhIgBQyQATmwsPeedRf2Hth5Ye87Cxf2Xn7jwt4H
VizsXbjlob2vXn9ob8efHNpb+pLDehutc3hv1w8e3vvvRUf0vrn3kb25naN6c358VG/zHx7d
e+cTx/T23/q43oFHH9876P4Tep/9zxN7r7vo5F79k1N617/6tN42h5zR+/HmZ/W+9eTZvW/+
6lzsZyz6Hcw75Zxe8+BpvQfLE3s/3PuY3rLFh/eu/9eDezd/eLT3lx+Z1/v1j8re2GlZb70n
DurttOKA3v0P79v7zN/u1Rvdco/eF27YtXdGZ5fepu/dsZe/cPteesS2vdf1tu7998lb9va6
dW7vl8s365291aa9E5dt3PvZbzfsnXPPBr2vZOv3bv/Rur2vfWid3ra3z+k9csnavfTs2b0n
zlmr95ols3qvvLvTm33JU2N7fv03Y58989djw//zv2M//eCTY8de98uxdhugz7iXgDgtTsfN
0PDeidPidDhr4s4Qp8XpuBka3jtxWpwOZ03cGeK0OB03Q8N7J06L0+GsiTtDnBan42ZoeO/E
aXE6nDVxZ4jT4nTcDA3vnTgtToezJu4McVqcjpuh4b0Tp8XpcNbEnSFOi9NxMzS8d+K0OB3O
mrgzxGlxOm6GhvdOnBanw1kTd4Y4LU7HzdDw3onT4nQ4a+LOEKfF6bgZGt47cVqcDmdN3Bni
tDgdN0PDeydOi9PhrIk7Q5wWp+NmaHjvxGlxOpw1cWeI0+J03AwN7504LU6HsybuDHFanI6b
oeG9E6fF6XDWxJ0hTovTcTM0vHfitDgdzpq4M8RpcTpuhob3TpwWp8NZE3eGOC1Ox83Q8N6J
0+J0OGvizhCnxem4GRreO3FanA5nTdwZ4rQ4HTdDw3snTovT4ayJO0OcFqfjZmh478RpcTqc
NXFniNPidNwMDe+dOC1Oh7Mm7gxxWpyOm6HhvROnxelw1sSdIU6L03EzNLx34rQ4Hc6auDPE
aXE6boaG906cFqfDWRN3hjgtTsfN0PDeidPidDhr4s4Qp8XpuBka3jtxWpwOZ03cGeK0OB03
Q8N7J06L0+GsiTtDnBan42ZoeO/EaXE6nDVxZ4jT4nTcDA3vnTgtToezJu4McVqcjpuh4b0T
p8XpcNbEnSFOi9NxMzS8d+K0OB3OmrgzxGlxOm6GhvdOnBanw1kTd4Y4LU7HzdDw3onT4nQ4
a+LOEKfF6bgZGt47cVqcDmdN3BnitDgdN0PDeydOi9PhrIk7Q5wWp+NmaHjvxGlxOpw1cWeI
0+J03AwN7504LU6HsybuDHFanI6boeG9E6fF6XDWxJ0hTovTcTM0vHfitDgdzpq4M8RpcTpu
hob3TpwWp8NZE3eGOC1Ox83Q8N6J0+J0OGvizhCnxem4GRreO3FanA5nTdwZ4rQ4HTdDw3sn
TovT4ayJO0OcFqfjZmh478RpcTqcNXFniNPidNwMDe+dOC1Oh7Mm7gxxWpyOm6HhvROnxelw
1sSdIU6L03EzNLx34rQ4Hc6auDPEaXE6boaG906cFqfDWRN3hjgtTsfN0PDeidPidDhr4s4Q
p8XpuBka3jtxWpwOZ03cGeK0OB03Q8N7J06L0+GsiTtDnBan42ZoeO/EaXE6nDVxZ4jT4nTc
DA3vnTgtToezJu4McVqcjpuh4b0Tp8XpcNbEnSFOi9NxMzS8d+K0OB3OmrgzxGlxOm6GhvdO
nBanw1kTd4Y4LU7HzdDw3onT4nQ4a+LOEKfF6bgZGt47cVqcDmdN3BnitDgdN0PDeydOi9Ph
rIk7Q5wWp+NmaHjvxGlxOpw1cWeI0+J03AwN7504LU6HsybuDHFanI6boeG9E6fF6XDWxJ0h
TovTcTM0vHfitDgdzpq4M8RpcTpuhob3TpwWp8NZE3eGOC1Ox83Q8N6J0+J0OGvizhCnxem4
GRreO3FanA5nTdwZ4rQ4HTdDw3snTovT4ayJO0OcFqfjZmh478RpcTqcNXFniNPidNwMDe+d
OC1Oh7Mm7gxxWpyOm6HhvROnxelw1sSdIU6L03EzNLx34rQ4Hc6auDPEaXE6boaG906cFqfD
WRN3hjgtTsfN0PDeidPidDhr4s4Qp8XpuBka3jtxWpwOZ03cGeK0OB03Q8N7J06L0+GsiTtD
nBan42ZoeO/EaXE6nDVxZ4jT4nTcDA3vnTgtToezJu4McVqcjpuh4b0Tp8XpcNbEnSFOi9Nx
MzS8d+K0OB3OmrgzxGlxOm6GhvdOnBanw1kTd4Y4LU7HzdDw3onT4nQ4a+LOEKfF6bgZGt47
cVqcDmdN3BnitDgdN0PDeydOi9PhrIk7Q5wWp+NmaHjvxGlxOpw1cWeI0+J03AwN7504LU6H
sybuDHFanI6boeG9E6fF6XDWxJ0hTovTcTM0vHfitDgdzpq4M8RpcTpuhob3TpwWp8NZE3eG
OC1Ox83Q8N6J0+J0OGvizhCnxem4GRreO3FanA5nTdwZ4rQ4HTdDw3snTovT4ayJO0OcFqfj
Zmh478RpcTqcNXFniNPidNwMDe+dOC1Oh7Mm7gxxWpyOm6HhvROnxelw1sSdIU6L03EzNLx3
4rQ4Hc6auDPEaXE6boaG906cFqfDWRN3hjgtTsfN0PDeidPidDhr4s4Qp8XpuBka3jtxWpwO
Z03cGeK0OB03Q8N7J06L0+GsiTtDnBan42ZoeO/EaXE6nDVxZ4jT4nTcDA3vnTgtToezJu4M
cVqcjpuh4b0Tp8XpcNbEnSFOi9NxMzS8d+K0OB3OmrgzxGlxOm6GhvdOnBanw1kTd4Y4LU7H
zdDw3onT4nQ4a+LOEKfF6bgZGt47cVqcDmdN3BnitDgdN0PDeydOi9PhrIk7Q5wWp+NmaHjv
xGlxOpw1cWeI0+J03AwN7504LU6HsybuDHFanI6boeG9E6fF6XDWxJ0hTovTcTM0vHfitDgd
zpq4M8RpcTpuhob3TpwWp8NZE3eGOC1Ox83Q8N6J0+J0OGvizhCnxem4GRreO3FanA5nTdwZ
4rQ4HTdDw3snTovT4ayJO0OcFqfjZmh478RpcTqcNXFniNPidNwMDe+dOC1Oh7Mm7gxxWpyO
m6HhvROnxelw1sSdIU6L03EzNLx34rQ4Hc6auDPEaXE6boaG906cFqfDWRN3hjgtTsfN0PDe
idPidDhr4s4Qp8XpuBka3jtxWpwOZ03cGeK0OB03Q8N7J06L0+GsiTtDnBan42ZoeO/EaXE6
nDVxZ4jT4nTcDA3vnTgtToezJu4McVqcjpuh4b0Tp8XpcNbEnSFOi9NxMzS8d+K0OB3Omrgz
xGlxOm6GhvdOnBanw1kTd4Y4LU7HzdDw3onT4nQ4a+LOEKfF6bgZGt47cVqcDmdN3BnitDgd
N0PDeydOi9PhrIk7Q5wWp+NmaHjvxGlxOpw1cWeI0+J03AwN7504LU6HsybuDHFanI6boeG9
E6fF6XDWxJ0hTovTcTM0vHfitDgdzpq4M8RpcTpuhob3TpwWp8NZE3eGOC1Ox83Q8N6J0+J0
OGvizhCnxem4GRreO3FanA5nTdwZ4rQ4HTdDw3snTovT4ayJO0OcFqfjZmh478RpcTqcNXFn
iNPidNwMDe+dOC1Oh7Mm7gxxWpyOm6HhvROnxelw1sSdIU6L03EzNLx34rQ4Hc6auDPEaXE6
boaG906cFqfDWRN3hjgtTsfN0PDeidPidDhr4s4Qp8XpuBka3jtxWpwOZ03cGeK0OB03Q8N7
J06L0+GsiTtDnBan42ZoeO/EaXE6nDVxZ4jT4nTcDA3vnTgtToezJu4McVqcjpuh4b0Tp8Xp
cNbEnSFOi9NxMzS8d+K0OB3OmrgzxGlxOm6GhvdOnBanw1kTd4Y4LU7HzdDw3onT4nQ4a+LO
EKfF6bgZGt47cVqcDmdN3BnitDgdN0PDeydOi9PhrIk7Q5wWp+NmaHjvxGlxOpw1cWeI0+J0
3AwN7504LU6HsybuDHFanI6boeG9E6fF6XDWxJ0hTovTcTM0vHfitDgdzpq4M8RpcTpuhob3
TpwWp8NZE3eGOC1Ox83Q8N6J0+J0OGvizhCnxem4GRreO3FanA5nTdwZ4rQ4HTdDw3snTovT
4ayJO0OcFqfjZmh478RpcTqcNXFniNPidNwMDe+dOC1Oh7Mm7gxxWpyOm6HhvROnxelw1sSd
IU6L03EzNLx34rQ4Hc6auDPEaXE6boaG906cFqfDWRN3hjgtTsfN0PDeidPidDhr4s4Qp8Xp
uBka3jtxWpwOZ03cGeK0OB03Q8N7J06L0+GsiTtDnBan42ZoeO/EaXE6nDVxZ4jT4nTcDA3v
nTgtToezJu4McVqcjpuh4b0Tp8XpcNbEnSFOi9NxMzS8d+K0OB3OmrgzxGlxOm6GhvdOnBan
w1kTd4Y4LU7HzdDw3onT4nQ4a+LOEKfF6bgZGt47cVqcDmdN3BnitDgdN0PDeydOi9PhrIk7
Q5wWp+Nm6GR699RT7/re+p2Tr178wssXL9l4g2xo4w0SICv5mRK1tw5efN3iS665/JKlly1e
ctHiq4YOveriC5YuhQNRJxwydMJJxw8dedLQiaf2TjkF5hEL4U6SJMsbGKdcdc3ioSuvWrx0
8eUvWHz+1YuXXg3nwguuvuYylGliJ/Esn/yuH7ZTzHJ+X+8tWXLJ4guvuuCaF1y69JIlv750
yQWXXbl44w2qlMnXE/xIulXB4vfzfXuGX9vIhj2nya/o5tLJAbZQAhVQA4yzk0ltZxiaMjZl
cMrolOEp41MmpMwwbNrYtplhmGGYYZhhmGGYYZhhmJExI2NGZrvDjIwZGTMyZmTMyJiRMSNn
Rs6MnBm5nQNm5MzImZEzI2eGXVMFMwpmFMwomFEwo2BGwYyCGQUzCk7DUqVkRsmMkhklM0pm
lMwomVEyo2RGxWlUzKiYUTGjYoZdNxUzKmZUzKiYYUlYM6NmRs2Mmhk1p1Ezo2ZGzYyaGQ2n
0TCjYUbDjIYZDTMaZjTMaJhh17SnIXPShElpwqw0YVqaMC9NmJgmzEwTpqYJp5a61W9zU5vb
MqClQMuBlgQtC1oaWB6klgipZUJqbK7lQmrJkFo2pJYOqeVDagmRWkaklhKp5URqSZFmts+W
FqnlRWqJkVpmpJYaqeVGasmRWnaklh6p5Uea2/m1DEktRVLLkdSSJLUsSS1NUsuT1BIltUxJ
LVVSy5XUkiW1bEktXVLLl7TdtljGpJYyqeVMakmTWtakljap5U1qiZNa5qSWOqnlTmrJk1r2
pJY+qeVPagmUWgallkKp5ZDbklkWpZZGqeVRaomUWiallkqp5VJqyZRaNqWWTqnlU2oJlVpG
pZZSqeVUakmVWlalllap5ZWxGzaTkBvG8spYXhnLK2N5ZSyvjOWVsbwyllfG8srY7YqxvDKW
V8byylheGcsrY3llLK9Mu31pNzBuC0NemXYb025k2q1Mu5lptzPthsbyylheGcsrY3llLK+M
5ZWxvDKWV8byylheGcsrY3llLK+M5ZWxvDKWV8byylheGcsrY3llLK+M5ZWxvDKWV8byylhe
GcsrY3llLK+M5ZWxvDKWV8byylheGcsrY3llLK+M5ZWxvDKWV8byylheGcsrY3llLK+M5ZWx
vDKWV8byylheGcsrYzdOxvLKWF4ZyytjeWUsr4zllbG8MpZXxvLKWF4ZyytjeWUsr4zllbG8
MpZXxvLKWF4Zy6vM8iqzvMosrzLLq8zyKrO8yiyvMsurzPIqs7zKLK8yy6vM8iqzvMosrzLL
q8zyKrO8yiyvMsurzPIqs7zK7PYqs7zKLK8yy6vM8iqzvMosr7JWwVoJazXMiRi3V1krY62O
tULWKlkrZZZXmeVVZnmVWV5llleZ5VVmeZVZXmWWV5nlVbv/kVleZZZXmeVVZnmVWV5llleZ
5VVmeZVZXmWWVxQS+9tlPwFuHa2yobSag9JqgA20CmA34nY7bDelVjmscFjdsLLBDO0BYAly
WWkPAAtBewCrfQ/AdN3eFEpIfZlA9bN254BfVXlZNth9KNu9PLjKsk5TiFtetbtDcFVNgz2t
AvtB7X4SXE1ZNdgaN43Pw0Yzr8ocKle0u2ami+1W0xRZiX2Ldo8RrirJ6qoqM2yL2s1GN0+g
R1XVJE2762m6eVY3VYHUMmn3Q+GqGvSiQC+SdvfSdAuIcWWgL0nT7jnBhTrEE3sZ7Z6T6ZZQ
V+xGFeyG3TjBVWN/ApvyJGk1PTXdKs8w10mNOWp3/ky3TpoKqo7cst23gqtOcuysom23m2S6
TVFgaWJrjObtdi7rJpjfqqqwx9pKVpp1wfICGl1hv8ftl3axY5MUSdFUtZvFrAvFarDviV0P
t7+ZYdE0UMU8RS/a3bCsW2DHEQsiqSCjdhubYR6brMqqKsGM2WWaYYbqvCmRmLT7VOhEXWVN
Dd1LmrzdlW/3ePkjfMZCZpUUJcQQU2zXLHqB/mOF1U3T7oCgsaQqaqh/hZXR7n9iGWJmciyg
KnU731hpJVZPAh0qmnYP3XTTGpTAUsuxr2Enm3bBPqzrBLOft6OLtFuCXBh8gG5Ju2pTcAIL
HXNdYOnYmUy72GksCsw4ZL/dnU26TVMlWPhlVbRLAkNfkAPrKCGB2nFMF1Qv6rLCfrLblU26
OXaeMPYA6et2VJDgp4HJY48Xi7vdnU+6WBvYPaybtGxHSU0XCx7TxqouQWo7BMME0XH0tYEi
21lsumWRlHWO/YOkrq24N1iNVYndQiwbRHNBNN0Ms4xlX1UQYrsr1+CHl+RYaWQ5eG2jMM6o
mho/zyIv7I+q6YKzYA3WBb6xy6buNli+GOtkGZaN3Qmsu+hAjZ060rmwezA1WMJVhkjOIhdO
jSWfYJ81ySosWrtXVuNHhR9+gZ5gbdpdorqLJYN9SzRWY7jC2YYLP3+sCuxu4PfBX1qNnz+6
COI3OdZG2zw6gO0IfgvgoN0lqbEWG2wOLFFBYJsIUqGNBmssqZwLv80EW668qLFp4pKo8UPD
fkuNzRR+LnanseqiP9gjw08KtLf7mnDx54SV3WAbY3eTK/yOsTnAigAR2y0HXJgfbOQq0ACs
QPNwJVjZdlk1iLcubN7w28D+Ilak3UXk3o8Q7zLApl3iJ/GT+En8BiF+duQr8ZP4TQnRl/hp
5IfBncRP4jc1xY/jMAzznmPkx4HlpEZ+HEVq5DdNR7ASP4mfxE+HPXXYU4c9p8RobZCHkSV+
Ej+Jn8RvQOI3dQ57tqfpdMpvmg7qJqKR0j5pn7RP2jfjtE/Xu8R7HcpEhGsQMRI/iZ/ET+In
8Vv1UU+d8pvGI0OJn8RP4jejxa+9yWAwdzqs+aOeE7vepdUw3emg0V7/iFHiJ/GT+M1o8Wvv
ihuM+NlHykR4p8OkL/ZsE3Wb37S8FkbiJ/GT+En8BnTYU+Kne9ynzuhS4ifxk/hJ/CR+qz7n
p5Gfzvnp6WZ6upnVSD3dzD6mU083m1pPN9Nhz/5zXbLb0alGfhr5aeSnkd+UHfmt5gtedLWn
Rn4a+Wnkp5Gfnmut51rrudZT55zec41wNfLTyE8jP438puzIr33Pw3M92lO3OjyXEMzE7yV+
Ej+Jn8RvmoufzvnNRHF7rnmW+En8JH4SP4mfrvaclvfy/SEBlPhJ/CR+Er8Bid+af8KLDntO
n3Nwf0ioVsd3Ej+Jn8RvRosfDwnqRe56kfvME1GJn8RP4jejxW/SjzfLrWoWVZHmRZXkpTHp
mn/Cy2q+1WEVN7lzrInX2ybGZFVZGNPURft6pKrMi1JPeJk6Iirxk/hJ/CR+AzrsKfGT+En8
mrJqsiRpmoT7TpDYLK1y7BqZvCwy7q3RladNU2RlWlcJ953oqpKsrirsPz0dlScGhySqJmmS
rA3Ks7qpCqSWScK9T+TlVWOqpkgzk6TOVZisrIxh26XrQ4G6KRCTl256pSkkfliCWbeusqbO
UpM0ecIzN+1itMvymY+sqye86AkveZJV9dR6wssgb3XQyG91nH97PtqEcBgyw5ZpjZtY07rI
KqcNpqjysmzSSje56yZ3q5ESP4lfVOK35g97coo67Pl8iNWgpynx08hPIz8d9hzQYU9d7anD
njrsqcOeHEw3RYFxdJbnOLhrjyVm3QSHeauqSk1tGju+zrqpSQsDr0kQxlF41jU4/lgkRVPV
7shu1s2SqklxVUFm0twl5kljmjxP07Jp7KHkrFukJcbtRVKZJrEj+qxbmiarMgzZapO6qCqv
86ZEYoLDnO0UddjT2GWfdMukLOqySvEgq8Ye8U26uSmxRnC4HctNI7+oRn5cHXVXT3gZ9Kho
JrSnkZ9Gfhr5aeQ3oJHfmr/gZWLix/2aqtv/Jnfu88HDXUns6DS602HqDNgGpcvSPmmftE/a
N+O0r5b4zbgHuqwsmhI/iZ/ET+In8dPTzWacGEr8JH4SP4mfxE/iJ/HTnQ64LCTDmYAkMZm7
B6TKs1J3OliN1J0Out7lD1zvoos9dbHn1Dl3qJGfRn4a+WnkN6CR35oXvzV/mx/3fnSb38rn
z6ZiXeIn8ZP4SfwGJH5T52JPXfAydUZoq0tYJX4SP4mfxG+ai98gn26mB7ysLjFa0+1K/CR+
Ej+Jn8RPF7zoghdd8KILXuyzaJ55mvUzlp5rrQe8mPwPXPCiw5664GXqHE7VyE8jP438NPIb
0MhvzV/wMtkHvOic39QRqdV1OFTiJ/GT+En8BiR+a37kN7GrPX//6WaTFz9d7bm6xGhNtyvx
k/hJ/CR+U1b8JjbyG+QFLxK/NS1Sq2t6Ej+Jn8RP4ifx0wUvuuBFF7zoghdd8KI3GuE1QVXe
VHliqjSriooHDusu3mk9JS94GeTIT7c6rK6R2JpuVyM/jfw08tPIb0AjP13woqs9p86FNBI/
iZ/ET+I3IPFb8xe8TOyc3yAveNHIb02P0FbX9CR+Ej+Jn8RvmovfIA976oKX1SVGa7pdiZ/E
T+In8ZP46YIXXfCiC150wYsueNEFL9PrgpdBHvbUyG9Nj9BW1/Q08vu/7J0HYBRV/sc3FUgo
CSUoUnKoKAjDm3kz8+ZRJPEA0aMEIYJ0wh1CUIqA0sQE8KRIsSOo5EADhuod7TzUoBT/GlAI
KCKHFAERUZoKivD/vdmNcoga4xKyu99VdrNvp76dnc/7/sr7QflB+UH5QflB+UH5QflB+UH5
QfkVTfkh2hPRnoj2lLaQnDEpmbI4kL7kujCFbRqmbXEVL6WaTF1Ki9u6I5j0NQnGHSFszn9c
ijKNbCmEZJJx70Imd6SwaFWbMXfSZUMzhTSEtHRuMN3XZBncFoahtm37jsGi94ZFy5i2b3+2
YUH5QflB+UH5QflB+UH5QflB+UH5FU35ldRUB0R7Xi6/WSBvFz4/KD8oPyi/IFd+/gx4QZ5f
IAPvwmMH/AA/wA/wC3L4+VP5AX4XAiSQ/wb8AD/AD/DzE/wQ8IKAFwS8IOBFhfRIy3Iszk2T
wnpcRxrXGAX4CCF0wzGkG3XDNd3QLYNaDUaLqZgerhk6vWGWFI4vpodrnAmpm7bBDd30rWgy
aUjT1HVbSjeIiGuWbnOK/GHCkEwNd2lbtiG54EIwcmb6lhKmY0qbVmSGN9SIa47g0uG0W2ky
+Pzg8yuaz6+kws+fyg95foGs9i48dig/KD8oPyg/Pym/khrw4k+fH+B3IUAC+W/AD/AD/AC/
gIWfsmU4GnMkozh103J0gyuZR02ULiUcxxRkKJGAXyBD6nIdO+AH+AF+gJ+f4FdSzZ7+hB8C
Xi4XjIp7u4Af4Af4AX5+gl8omD0Bv+KG1OXaH+AH+AF+gF+Qw8+fAS+A3+WCUXFvF/AD/AA/
wA/ww/RmmN4M05thejOkOiDVoWipDjB7Is8PeX7I80Oeny5olnHhZhsaGs1ELkxm6kLXvcmM
NBu5TfOOM67yGblvznLdobnOKTvSNAR3JyjXNamrScwZpTmaTN1bdV2zadZ0nVkmpSR65yzX
NZPrjkPZjRZlQSq7FC1lMMeyKMGRM8txt8U0KQWjJEtbWN6MR6YJmvWccjGZmhndzbFkms2o
xRa6oGPxrWcaNmVe0oTqlB+pIt11phlq97rklFZpuYMFplHWpUGHIXVbd+dglxolWNK+KaXT
ptnaVXKmpB3SgdOxSm56T1FqtsVsx+SGzRyHq1OUlK4pbIOyQy1GS6uDkBqnU2aWLQSno1MH
ITVDMJOSM9X07TRhu9uk0ylLx+COZVpuCqfUaBp3yg6l74I+cfvG0ST1r25SPCT1je0NjqQD
cAzqaVvYlqE272jCVF8ZLalOUXWOQz3PDJNWFNS1Un1njmZRZ5oWHQl9m3pJhR/MnsVtUgyE
/cHsCbMnzJ6AH8yeMHvC7AmzJ8yeMHtC+RVN+SHVAWZPmD1h9oTZE2ZPmD3JQO0aR8nebZIF
mpOJ1PbZS9Wsf4zm9ZMmGaG9VlWyu3KyXNtkkhWW1/ZK8+1ReU93Hj6an8/dFtnSaRuSDNVM
+Jp+f5K7OixBdmkyk5OJW1LJUNsXxulY0iLzM5nfvYVABalig85DCjJ+ky3cXdFhZOJ2LcSS
lnebqFqpRYVIaXvM0dUoIBAsf6F8jLB6wuoJqyesnkFu9USOeyhD7pfOHfAD/AA/wC/k4Afh
F/LCFOwD+8A+sC/I2YdYz18SP6HcDvgBfoAf4Af4weUXckoQ8AP8AD/AL2Dhp6JPfrumA5Rf
KCu8Xzp3wA/wA/wAPz/BD4kOCPYMnCBXwA/wA/wAP8APZk+YPZHijhR3pLgjxT24Utz9afZU
qYaU+Yc0v4CHJZQflB+UH5Sfn5QfZvaE2RNmT8zvgvldML9LyM3vUlJ9fv5Ufpjg5ZcCSAKt
HcoPyg/KD8ovyJUfJngJNDAVx/ECfoAf4Af4AX4IeAl4H97vBSbgB/gBfoBfkMMPZs/fC4ZQ
WB7wA/wAP8AP8IPyg/JDqgNSHZDqgFSH4Ep1KLLPzysZUdEoKMEI5QflB+UH5Rewyq9w05sV
GX7eFQE/wE9F7xu27ei6wR1TmGpYpJqozKNOJSh1U5qmrwmpDkh1QKpDyKU6lNQ8P8AvFHx4
v/ccofyg/KD8oPwCVvl5S7v//jruDur5BaWa+z0ABPwAP8AP8AP8EPAScjAE/AA/wC+k4adM
go6f4Ff8M7wUzueHVIffo4hCZVnAD/AD/EIafgoMgQu/wpk9iww/74oIeAlKVQj4AX6AH+AX
sMrvMsMP0Z40NApWJQj4AX6AH+AXcvBDvEvQMq2wrAb7wD6wD+zzE/tKaqZDka2eEH4QfrbN
1GWgUIk0P9UNDpPCMBU4beHrGcdhpm4Ypi11R90EaClpWY7FuWla3HZnTeEa47YuhNANx5Bq
8KlzTTd0y6BWg9Fi3iZDpzfMksJhzM2c5BpnQuqmbXCD0im9S5lMGpRZqdNRSOX3p21Zus2F
tJgwJFO/eGqyDco240IwmrnGt5QwHVPatCIzmG9bjuDS4bRbaTJM8IIJXgJlgpfCxbt4GSYd
ykY26SdFl30hMx3g8qObSGGVVKAtB+UH5eciEvAz3IEH02icZwF+gQI/uPyCF06XG6aAH+AH
+MHsCbMn0vyCVuH9EkQBP8AP8AP8/AS/4k/zg/KD8vsluP1WO+AH+AF+gF/Awg8+P8DvtyD3
S58DfoAf4Af4+Ql+iPbknKLSmKMrDfxLN120l4y+AfwAP8AP8PMT/ALH7Ik0v5BnM9gH9oF9
YF/Isa+QmQ7eFAlMbhaUoAT8AD/AD/AD/BDsGZSA+zULM+AH+AF+gJ+f4Ff8Lj/Eu5QM99mv
Qaakfgb4AX6AH+AXsPArXKZDkSd4gdkziON2AD/AD/AD/IIcfpjas6Sqryt5XIAf4Af4hTT8
lLjxVzW/4jd7QvnB7FlUgAJ+gB/gF9LwU6oI8LMR8IKAF6ZTGQLhzvRPFRwsYdpUpECgqIPt
0DzwnJlqnEwjBhR1kN4yH1yjShZUSYI7UtLlonqHKlcIyzEoz5fppnBLSxiaoAoVJlW9ELru
rVxhaFShwnAYV8UrOPd2q+7oUlIpDNMQ3C1moWt09VlSMqppYTK3Voau2TbVt2CWSfUnbPf7
0DWTUyUNKmVhUckLt3KFrtHE/ZZF1Sw4sxx3W0yTUjCqqGELy1vegmlC2jSLNeAXsGbPwgW8
FNns6V0RqQ5BCUYoPyg/KD/AL2DhVzizZ5Hhh4AXGpUW1axY0tcD/AA/wA/wA/xg9gxayP0S
hAE/wA/wA/yCHH5eAVeEWrZQflB+8PnB5+cykurBWzbXLSodD5+fqUtuc+H1dDKNScMg16PU
bZ0pH6bUJH1I/iLHsB3h+tElORnJWUn+SclNr1tTarbFbMfkBk2H7HDl1pSaRW52w7TIH0pL
K4el1Di5OanvheBUaVcZ+6RmCGZKhwtynRqGsuxJTSc3p3QM7limxZTnXmrkp7YNTv5X+sT1
hzqaJJ+qbjLOyR9qqxWDPeAFZs9fUj+h3A7lB+UH5QflF7DK7zIHvED50dAoWAEJ+AF+gB/g
5yf4ldSiDjB7BivA/sh5AX6AH+AH+PkJfsWf5F78yk+ZnAXlOpGNW9iWYUjH8pZHErZJLgGU
8wsYpQj4AX6AH+AH+BU62hPw+yNqqyStC/gBfoAf4Bew8Cv+PD/AryQB7I8cC+AH+IUk/NxQ
SB1TvAR8uGfx2z3VHmH3/CPUKSnrgn6gX0jST93CAD9/5zqU1IgX5DqUFOCUpOMA/AA/wA92
T9g9C+30g/IrSQD7I8cC+AF+gB/gF+TwQ67DH4FEsK4L+AF+gB/gF7Dwg88veLPQLzd0AT/A
D/AD/AIWfoUL94Tyu9wgCcTtA36AH+AH+PkJfsUf8FI45Qf4BSKcLvcxA36AH+AH+PkJfsU/
xQuUH8yeRYUk4Af4AX4hDT+livxV1qH4lV9R4eedkkxyQzdtoUu70MGeSHIvKmtK2npgH9gH
9oU0+0KhpFGRrZ7e/EAqS2ULKYVhG8JBpkNJg1hRjwfwA/wAP8AvyK2eyHEvKiCCeT3AD/AD
/AA/P8GvpFo9fw6/Ils9IfyChYdgH9gH9oF9Icc+B/ALmMpDlwu2gB/gB/gBfkEOvyK7/Lwr
wuUXlKAE/AA/wA/w8xP8QiHRAcGel0uJFfd2AT/AD/AD/IIcfj93+RXd7An4FTekLtf+AD/A
D/AD/PwEv8CJdwH8kBoP+AF+gB/g5yf4lVSzpz+VH6I9L5cSK+7tAn6AH+AH+AF+hZ7gBfAr
bkhdrv0BfoAf4Af4BSz8FIocjTmSMd0xLUc3uJJ51MS5JRzHFLopJaI9LxdAAnm7gB/gB/gB
fgELv8LN7OlPsycCXgIZeBceO+AH+AF+gB/gB7NnUObyXQi7i/8G/AA/wA/wC3L4+dPsCeV3
MUQC9T3gB/gBfoBfkMPPn2ZPBLwEKuwuPm7AD/AD/EIafkoVhV41v6Ln+QF+F0MkUN8DfoAf
4BfS8PMGRzomdwxhSVvYluGNIhGmFCYzhM6FJbyItG1mmCbjwrEsyV1qWsLSTUsw0zYMvfiT
3BHtiWT1osIX8AP8AL+Qhp8/lV/gJLkXuagDXH5FZU1JWw/sA/vAvpBmnz+FX0llnz/jXWD1
LGkQK+rxAH6AH+AH+IVcvAuEX8glNlzMSLAP7AP7wL6QYx/CXeApBPwAP8AP8PMT/Io/3MUb
mfNbk5sh0eFi1YP3dNszNENdGe6r7lAsl+5YXCibgNskTNuWuqB2ZTVXTbbt6DR9Hk2ZZxas
KKTUuUEhX9I0fUtRzJjkjElZsB7XhSls0zBtiyujOW2Km7qUFrd1RzDfDrlg3BHCpln5Cpai
aDNbCiGZZCq4jNajqDRJUWnSshnz7c8U0hDSoqNguq/JMrgtDENt2/Ydu0XvDYuWMW3f/mzD
AvyoU7nmCC4drhtMmkzdwrzd6PblT09cE4JZNtctu+Cb5ZqpGzp9YY6UhuWuyTUmLMdwdEFf
hvBdJPSFUeCgqQtd576vQ0UHOoxbjMIGfV+t7tAlIS3LNAR3d6trdPXRd804o9WVR0nXNZsu
Lp1ZdLkx71er0zWhOw4ThmXopnt56ZrBKCBRcMGZ5bjbYpqUggm6vCg80V2IaYIuDssB/PwE
v5Lq8gP8ALufK12XcF6mEL0AP0OzHUPn3NAZ806QSz0kTE7Ip9ElJ2x6O8thUhimAidFhvua
HLq3G0R3SfdhbxPdxmkowU2TEF/ABYI93X91wzGkS2CuETwsg1oNRoupFblmEIUUFITj4zvX
6O4vdeIFHZrpW9Fk0qDxhk5HId2bOdcs4hCNAggDkrnY4ZptSCIAUYtOzLeUMB1T2rQiI9h5
9wj4GW7fM43GeZZjC10QiH3QNA2bvhEadFG/KamhMxoyEnt1yam7vchnGn0bBjFY6rbujtOk
Rh1P4KWv2qYRnepoSbQlatMFIrnp5bvUbIvZlGdg2MxxuLpyJH2NwjboqrEYLa0OQmqceE8D
DyE4HZ06CKkZlF5AIxY1xKNBndukE++lQ2NTy7Tcr1ZqdM3SVUMDEfrEHRg4mqTBhU75CpwG
BrZa0V9ZfiUVfuqrFZp0aHRs0k+KLnuYPX8Og1ADJOAH5efiFvAD/P54ll9JhR+UX6iBrTDn
C/gBfoAfzJ5BbvaE8isMDEJtGcAP8AP8AL8ghx+UX6iBrTDnC/gBfoAf4Af4oaBRyOX9AX6A
H+AH+AUs/FQI12Ws4+6VjBS0RAHGFOJmGxQG5QbPOIyim9xZUKVjqVgmoVEwO0VCc4pKYxTp
TE2FUR9Y5sr1E+AH+AF+gJ+f4Kdu+Y5GcbCGTdNdU3QlMcPbRJlOFHPMKR/K9s2HrYKgGYU5
S5MST5RTzqHwVUpEUpHPlG5jeTP4KByZMp/csGQKV3aXovwZ2oak7CbmRdFvw8+fZk91EEID
/K4ctPw1YAD8AD/AD/DzE/wQ7QnlFzhQBPwAP8AP8Aty+CHa019qKZi2A/gBfoAf4Bfk8POn
2RM+v2ABIOAH+AF+gB/gh2jPkAvQAfwAP8AP8Aty+P3c7OkN0JRqskCayk7S9MG2T9JR8KZF
08zRHLPeSYEpuAXBnsEi9i48D7AP7AP7wL4gZx+snhfe9PG3NyYH8AP8AD/Az0/wK/5MB2/y
AyoaAWi/P8gU8AP8AD/AD/CD2RMuP5TzQ0Ujt/iSW8znoieU80NFI8OkUkiCKiX6UtUpl103
LaqtRMUZdaT5Ic3v9yuwK6Vaofyg/KD8oPyCXPn5Md4F87tcKVb5e79gH9gH9oF9fmJf8Qu/
ws3s6c94F8DP3xC6UtsD/AC/kISft349o7rqNpVtB/0Cln4IeAkcM+OVotwv7Rf0A/1Ckn5K
MuiAH7NsJYucgIVf8Us/XzYgijoEfIAM4Af4AX5QfgELv8Ipv5/7/BwkuQc8vH5J0RW2HfAD
/AA/wC/I4edPpx+UX2HhUtKXA/wAP8AP8AP8kOcXckoQ8AP8AD/AD/AD/AA/JLkjyR1J7g7N
dUxFwqWb5M80mtfY0A2TOyaS3EMryd1rL8XE1kEJRig/KD8oPyi/gFV+hYv2RMBLSfe/XYnj
A/wAP8AP8AtY+BUu2hMBL1cCLiV9n4Af4Af4AX5+gl9JreoA5VfSQXQljg/wA/wAP8DPT/Ar
/vnNCqf8AL8rAZeSvk/AD/AD/AA/P8Gv+JVf4Xx+MHuWdBBdieMD/AA/wA/wC1j4FU75AX5X
Ai4lfZ+AH+AH+AF+gB/y/IIyneHXAAz4AX6AH+DnJ/iVVJ+fP5Wf0ppCczCxdcDDEvAD/AA/
wA/wg/ILeJj9msq71GeAH+AH+AF+foJfSQ14KXK0p1cyYoaXoAQj4Af4AX6AX8DCDwEvKGZ7
KVVXmDbAD/AD/AA/P8EvFHx+KGlUGLAEwjKAH+AH+AF+foJf8Zs9ofyg/IoKWsAP8AP8AL+A
hV/hktyL7PPzrgifH3x+MQqVtu3oukHVXYSpvMGqSUipc8PSTWm6NWCoSdpCcsakZOryoYW4
Lkxhm4ZpW1xdsKrJ1KW0uK07gklfk2DcEcLm/MelTGbYUgjJJOPehai0jBQWrWoz5tufKSQd
hUVHwXRfk2VwWxiG2rbtOwaL3hsWLWPavv3ZhgX4AX6AX8DCD8oPyg/KD/CL0blm6TanUQAT
hmTu2IRrtiG54EIwKlToDju4JqgunbRNXWeGd9jBNUdw6XCd3ptMGa+8Ywh3IPHTE60pmGVz
3bILhjVcM3WDdkoDEmlY7ppcY8JyDEcXNBIRvhESjVaEyUxd6Dr3jUVMm8YmjFvMktw3rtGp
hh6NaizTENzdra5JXQ10GGe0unIp6bpm08hKZxaNtZh3XKNrJtcdh87aMnTTPUldM5hjWXTi
nFmOuy2mSSmYoLGVsLw9wTRBIyPLAfxCDn5q9Cs0yel6odqNksbXtrpuKIHPsaTlqMtZekfN
1ET1HGmAL6iqIxV59C6FNL+AF4NKtxXoN0t3bBu1bFHLFuxDLdsYh0ZIarhiCJ0LS6jxikOj
DhZatWzVaQN+1AlFFVcleT3AD1ZPWD0h/EJO+DmFU35KGAB+gB/1gEIlXH6qGxxGRhBTgdN2
B8WqySGjnkE+TUkGOG9nkf3OsTg3TXJsFhgEycVJhjfdcAzp+h25RlZDy6BWg9FiakWuGWR+
VNZA4fi8mlwjs58kC42h7DS+FU0mDfKy6nQU0mfPhNUTVk/pkEfeMi3XoC01cnDTVUMWaEtI
1yLsaJKsyrrJOCeLsK3u746f4Ff8mQ7qunc05khGNivTcigawXtCdHaWcCgygX4u0ivgpEMx
ASb9pMjYD/gFp5r7PUoTyg/KD8oPyi9g4VfUeJfCCb9LWD3VDkkLwuUX8JZQsA/sA/vAvpBj
XyGF3yXgh3iX3yOuSvKygB/gB/gBfkEOvyJbPQE/0rklGWB/5NgAP8AP8AP8AD9kOgQt5H4J
kIAf4Af4AX5+gp8K6nI0Sr80bIuSMx2dsuO8TTTDBSVccpoHw5YqpdOhGS4oJIcCvaRJOZdK
YTk0WQZNQKFivyjT1PI68yjtlGa8cNNRKU3VXYpSR2kbkma1YMLXhHiXX7rBo/2XlSvgB/gB
foCfn+BX/MGeRY13gc/vl6EQKsAE/AA/wA/w8xP8Sqry82brFSHT4RI+P0R7BgscAT/AD/AD
/PwEv5Kq/BDwEizA8ud5AH6AH+AH+AU5/Pyp/JDq4E8AXcltAX6AH+AH+PkJfqFg9gT8riSw
/LlvwA/wA/wAvyCHH8ye/oRGsGwL8AP8AD/AL8jh50+zJwJeAD+UssW81i42Uc3PnbKcaTTL
uEFFBaVu627VZUnF4qisoUlTmNtUn1klvEkqH0hlCGnic8lNb8FCqdkWsx2TGzZzqIqcu5Sl
C9ug2dAtRkurUoRS41TAkGahFoJbjq1uwJLS4phJJRhVwWYq0ew26VTAEPNau1NdXzivNeAX
LMDy53lA+UH5QflB+QWs8rvMRR0ukeoAn58/AXQltwX4AX6AH+DnJ/gVf6pD4eDnT+UH+F1J
YPlz34Af4Af4AX4BCz/M8IKZWooKRMAP8AP8AD/ADxNbY2JrKodscdc573JRUBVoSd53mynr
t2pCIXcUctctKh3vvSK4hoAXBLxYFHpjG4Ze/GbPwik/pDoUVR0F83pQflB+UH5QflB+UH5Q
flB+jqFzblBcucGVn5yGB1SNhfQulU3hNL71NjlUaQWpDi42ofyg/KD8YoQmbNOyOaeiTczR
1TURzKopGM4Nyg/KD8oPys9Pyk/d8oOqnh9SHYIY4oAf4Af4AX5+gl9J9fkh1SEYlJq/zwHw
A/wAP8AP8IPPL+TMtIAf4Af4AX5BDj9Ee/pbNQXD9gA/wA/wA/yCHH4wewYDrPx9DoAf4Af4
AX6AH8yeMHsi1QGpDm7ovqoloF/0xDUhqLIAR5K7ZlimNHXJbSrcgFSHK5fqgLk9kVJRVEUI
5QflB+UH5ecn5YdUB+T5BQ6MAT/AD/AD/PwEv+JPdSic8kPAS1HVUTCvB/gBfoAf4Bew8Cv+
uT3VHoXmMKpcLGzLMKRjqTrFmOEl4HyGgB/gB/gBfkEOP39GewJ+waIGAT/AD/AD/AA/RHsG
nHL7oxAG/AA/wA/w8xP8EPCCgBcEvEhbUA0EVlD1zdC4Lkya9twwbYsrJzVRl1OouLS4rTuC
Kau5ahKMO0LQ3Og/LmUyw5ZCSCYZ9y5kckcKi1a1GXNj8Q3NFNIQ0tK5wbzh+YZmGdwWhqG2
bftKMVj03rBoGdP27c82LMAP8Atp+Kkfh+Mn+BV/wEvhfH7+NHuquxd8fn9UdZWE9aH8AD/A
L6Thp8AA+NEA2/ZhjQJYLIcG2PRwh81EOtOgwTwVMbMN4cDnVxLA5Y9jAPwAP8AP8IPyKzT8
oPz8AZ6SsA3AD/AD/AC/IIefP/P8oPxKArj8cQyAH+AH+AF+AQs/pcMcjTmS0cSMpuXoBvfa
cRnFDQjHMYVukvnS9dNJh4ICTIcxZtAK3iZuUOV1octfMHt6nYUwewZlJCjgB/gBfoBfwMKv
cAEvRYafd0XAD/BT8ZiGbTs6Da9oSGWqYZFqIl8wDaksGmKZvuhLA9GeqmekZTkW56ZJMa3u
7MdcYxTdKoTQDceQbsgp13RDtwxqNRgtprqUa4ZOb5glBQ1T3S7lGmdC0iDVUENV34omkwZ1
ua7b9AV4V7R0mmlZWkwYkrlfD9dsQ3LBaUZqmrHbt5QwHVPatCINgX3bcgSXDqfdSpO5h3rR
nNa+o8DE1upuqzNMbG1JFXztaJagH37BxNbFn+pwmZXfJeCn9ohoT3+YHa/0NqD8oPyg/KD8
glz5ea2XRTB7XgJ+8PldaWj5a/+AH+AH+AF+QQ4/L8P8Az8oP3/B50pvB/AD/AA/wC/I4fdz
5Ve4eBcIP7LxXmlGXa79g31gH9gH9vmJfcXv8itcvMvP2VfIYM9LwA/C73LBqLi3C/gBfoAf
4Ocn+GF2M0ztGThKEfAD/AA/wA/wK/QEL4h3KW6Fdrn2B/gBfoAf4Bfk8EO8y+UCSCBvF/AD
/AA/wA/wK7Tyg88vkIF34bEDfoAf4Af4BTn8ihzw4l3xfyZ4AfwuBEgg/w34AX6AH+AXcvAr
cqYD2BfIvLvw2ME+sA/sA/tCjn3IdAicoMwLgeXPvwE/wA/wA/wAP7j8gjaX/ZeACfgBfoAf
4Af4AX6AH9XEsqgqgJq4nqo1WMK0bakL22YqWFg1oaaD6gaHSWGYCpy28PWM4zBTNwyT+stR
ub60FGo6mEJFDFBXCCpQYVIHCV33Fq4wNCpQYTiMq9oVXNUHoKV0R5eSes00BHerSOgaXX2W
lIxKWpjM7VZds20qb8EsKiHCbLfzdc3k1OlUycKiihfKKaPrGlVssywqZsGZ5bjbYpqUglFB
DZvKELgLMU1I26a6G8wU0nA3xTS61C2HCrwJOhbfeqZhU5UNkwqZUOSD2jpqOliXrOkQCjnu
SPP7JSUVaO10wzF8tyeqSOQQ5AA/Q+dUNYjqXbpFMdWN2+SEfKp+yZlZQDrAzzsc4hoRn6oo
cUdKGispMlDVJmE5hqMLpgN+hEvHsB3hDigl0ZaoTaCW3PTyXWq2xWzH5IbNHIcrfEjNovGm
QWWwLEZLKwJLjRPvmWULwQnN6gYsqZIYM6kKlaAxhOH+iqWmE++lQ/XGLNNya1VJja5ZKoNF
3wV94g4MHE3S4EI3qdgrDQxs9fN3glz5qV+t0DCtNfx8FwIa8IPZ0+UVqvlB+RmkscmQYRmK
rQ6N+ZRYJ0xyYbnmDYc0NzNMoqYgUX2pan6hoPwQ7XkhQAL5b8AP8AP8YPYMcuXnzda7UPkh
0yHkXHwXcxrsA/vAPrAvyNlXZKunF5r/k+IOl9/FEAnU94Af4Af4AX4BCz9lg3Q0csczClYw
LUf3OuqpiXNLOI5Jvk2KoILLj3ogUCF1uY4b8AP8AD/Az0/wQzU/FDQKHMgCfoAf4Af4+Ql+
xR/vAuUXOLC5XAquqNsF/AA/wA/wC3L4Fdnn513xf3x+CPYsKmxK2nqAH+AH+AF+QQ4/f/r8
EPBS0iBW1OMB/AA/wA/wA/wKPbsZ4FdU2JS09QA/wC8k4efOfkKzlGF6M8zwYtJcdtIuNP1g
9yxpFCvq8YB+oF9I0k/dwgC/UJnezJ92T8CvqLApaesBfoAf4Ae7Z8DaPb0zsf1Wol+RI14u
keUO+JU0iBX1eAA/wA/wA/yCHH5QfkUFRDCvB/gBfoAf4Af4wecXclPAAH6AH+AH+AF+gB/g
h3p+Dur5qWAQt47rRU9cE4IqwHHdsqm+rHKkUPE+1PNzqxgyjUnDoJq6Urd1porzSk1SMSDU
81Ozb1IVY5PqCnNLp2LPqnMcjZtUctAybGlSaWF1LTlUoNDiVI/YplqDwvJ68wwqnEkXHKNX
5nibqEgkbUNS+WEmfE2XzeeHLHf6YoLV9AnlB+UH5QflB+UH5Re0kPsleAN+gB/gB/gFOfyK
HO0J5QflRxWc1WWgUGnbjk6FQ6hYiKliqFSTkFIncwUVDzFdOxk1UUVoyRkrMI4ZGie7h7BN
w7Qt7uZYUZOpU7URbuuO8OYcU5Ng3BFk5+A/LkW1pCkBVUgyeyhzCe3P5I6kmtPSshnz7c8k
G4iQFh0F89rrDM0yuC0MQ23b9h27Re8NMqwwMr14N2UbFuAH+AF+foJfSS3rAPj9kvoJ5XYo
P8AP8AP8/AS/4i/rULg8v5+nOqCSe8hZOS/mPNgH9oF9YF/Ask8ZkS5jMVvkuFP/XgyNYHkP
+AF+gB/gF7DwK5zwK7LVE/AD/ODysx2KpubkLPT6Ch0KwDZMBU5bFDQ5jIL+yacpdUdZf2hc
IS3LsbgK6Sb3o2riGiMXpxBCNxxDun5HrumGrqK7hcFoMe9Shk5vmCWF4/Nqco0zISlM3OAG
uVa9S5kUW09eVooTJ5+rt8nSbU6+TyYMyVyPLNdsgwLuOaUoUAqHbylhOqa0aUUVQO5d0RFc
Opx2KynKXDVdlOTgvkWmA+UtqM5hmmGRg1uXnLrbQqaDJeiXYRh6SXX5/dzq6cDsGbSKrrDK
FMoPys+FMuBnuAMPplFol+XQPP/C0aWLfKaZhk3DEYqzokED4GcyLhzL8mXrWYIC3QrgFzgu
v6LDT10AQnMY5XQK2zIM6VhekFI4H6XAchqhMscdBhT2JozlroxpFfAD/AA/mD0D1ux5mX1+
akBEpKPRD0W0CxoD0ZAI8KMeCAZgA36AH+AH+PkJfsVv9iwc/LwMkw6lQpnkSSBrf9GVH+AX
DOBT5wD4AX6AH+AXsPArXMALfH7BAix/ngfgB/gBfoCfn+AXCj4/KD9/AuhKbgvwA/wAP8DP
T/ArfrMnlF9w+N+uBAQBP8AP8AP8AhZ+l9nnhzy/IAluuRRcAT/AD/AD/PwEP5g9keoQOEoU
8AP8AD/AL2DhVzjlV+SAFyg/KD/M8IIZXlxGopYtktxDPMkdAS+XMiEGYhuUH5QflB+UH5Tf
pWvZQvlB+UH5QflB+WF6M7oPGOavKL9QiPbE9GaBqPIudcxQflB+UH5QfgGr/AqX6oAZXi51
8w/1NsAP8AP8AL8gh1+RA14wtyfMnjB7wuwJsyfMnr9l9iypqQ5QfqGu8i51/lB+UH5QflB+
Qa78AL9L3fxDvQ3wA/wAP8DPT/ArqQEvRYYfoj1h9oTZE2ZPmD1h9gxUsyd8fqGu8i51/lB+
UH5QflB+flJ+8PlhejNMbyap8jFnTEqmLA6EWK4LU9imYdoWV3MkqCZTl9Litu4IJn1NgnFH
CJvzH5cymWFLISSTjHsXMrkjhUWr2oyZviYhDSEtqlXJdF+TZXBbGIbatu07BoveGxYtY9q+
/dmGBfgBfoBfkMMPyu9SyifU26D8AD/AD/ALcvjB5xfqoLvU+QN+gB/gB/j5CX4lNeAFyu9S
N/9QbwP8AD/AD/DzE/zg84PPDz4/+PyUV1NalmNxbprk2VSDYp1rjHycQgjdcAzpOh65phu6
ZVCrwWgx71KGTm+YJYXjc2tyjTMhddM2uKGbvhVNJg1pmrpuS+n6Ublm6TYn5ycThmRquEt7
tA3JBadyDI6h+5YSpmNKm1ZkhtfbyjVHcOlw2q00mXuoruv0oieuoaoDqjr8ytyeJRV+/lR+
mNszWBQjlB+UH5QflF/AKj81nHM05kjGdMe0HN3ginTUREFzwnFMQWNFWWSfn3dFxzQogE8K
wzaEA/gBfqYwXWlhaBRnKSnO0qKrzPSFWhpQflB+uqDQW+G7SCg8V5jM1IWue+WtoZGMNRzG
lcLlvkBe3aEAYNLLpiG4eynpmtRVZC8j4WsyJSx0XbPpTqQziy435g3k1TWT645DetciXezK
W10zmGNZJHk5sxx3W0yj+xcj2W0Ly6uBmSYoFJjUOTMpXNhV3UyzGbXYQhd0LL716N5HWpyi
jEkxQ/n9ivIrqT4/f8JPXV5Cc5hhcGFbhiEdS1lihEbB7BbFqZN5hjm66olggUSwngeUH5Qf
lB/gF+TKz59mT8AvWGAI+AF+gB/gB/hdupjtJcyegB/gB7OnYSpw2sI1lxkamd1M3aAsfkkW
OGWfQ8ALzJ6CTK4U22TTzA3KNibJzkr2WrpAJDe9ll2p2RazHZMbZC1zuLpyJMUtCdugMCmL
0dLK9io1TpZeZtlCcDLKKturJH8DMylKSU3lQJM3uE06WXqlY3DHMi03lklqNKUDhUmRCZo+
cU3CjibJrKyT9ZKTSdhWKzoBCz/VE7/t84PyCxZg+fM8oPyg/KD8oPyCHH7+9Pkh4MWfALqS
2wL8AD/AD/AD/GD2DLkAHcAP8AP8AD8/wS9woj29AZpSZc1SZK+k6YNtnzOPgjctMj9T1LF3
UmCK7Lww0wEuvysp1vy5b7AP7AP7wD4/sa+k5rj70+oJ+PkTQFdyW4Af4Af4AX4BCz+FIsS7
IKWwKBAF/AA/wA/wC1j4IdgT4CsK+NQ6gB/gB/gBfkEOP5g9iwqIYF4P8AP8AD/AL2DhB7Mn
lF9RAQ34AX6AH+AXsPC7zGZPb3I8oj2DMgsC8AP8AD/AL2DhVzjlB7NnUdVRMK8H+AF+gB/g
5yf4BU6an4M8v6BUc78H1oAf4Af4AX5+gl9JzfPD1J6/BwqhsizgB/gBfoAf4FfoGV4wtWew
wBHwA/wAP8AvYOFXOJ8flF+wAMuf5wH4AX6AH+AH+BVa+SncopC7PyF0pbYF+AF+IQk/t9ad
zqi8nm1bDugH+oF+IRcBA/qBfiFJPzWAB/xCpZgtch2ulLwqyfsF/AA/wA/KL2CVX1Gz3JHq
EHJC72IOg31gH9gX0uxTosgJOfYVPc8P0Z4XQyRQ3wN+gB/gF9LwU5GQwQ4/f1o9Ab9Ahd3F
xw34AX6AH+AX5MrPn/BDtOfFEAnU94Af4Af4AX5BDj/k+QUqoC7ncQN+gB/gB/gBfsh0CLkA
GMAP8AP8Qhp+CHixhS7tQsMPPr/LqcaKc9uAH+AH+IU0/EIz4AWZDiEn9C7mKtgH9oF9YF/I
WT3BPrDP0Aw18HMZqDu2zXTH4kJdGW6TMG1b6oLalW1ENdm2o+sGd0xhFqwopNS5YemmNE3f
UtIWkjMmZcF6XBemsE3DtC3uTq1haNzUpbS4rTvCO9UUNQnGHSFszn9cymQGGSSEZJJx78ZN
7khh0ao2Y779mUIaQlp0FEz3NVkGt4VhqG3bvmO36L1h0TKm7TtB27DAPrAP7PMT+0pqNT+E
u1wsevDeR7gC0gF+RHfbMXTODZ0xg/voLkxOyGcO4dz0cdRhUhimAqctCpocZuoG0V3qjqpq
RtuSFk0ayblpEuLVfUHnGiPYCyF0wzGkS2Cu6YZuGdRqMFrMu5Sh0xtmSeH4+M41zoTUTdug
QzN9K5pMGjTe0OkopDug4Jql2zR0sZgwJHOPnmu2IbngQjA6Md9SwnRMadOKzPAOO7jmCC4d
TruVJnMP1R1DXPTENdqMZXPdoj16hzVco5OmndKARBpWwUkKyzEcXdBIRBT0IZ2MSR0kdN17
koZGJ2M4jKvz5L5xje7QeIh6zTQEd/etazT0ooEOo9M3mdutumbTyEpnFo21mHdco2smp06n
s7aod9yT1DWDOZZFJ07zdznutpgmpWDU+bawvD2BiT3p21RfULBn+alzFJp0aHRs0k+KLnuk
uJeD8oPyI3RYSoD67r+AH+BnORQBIQjEPmiahk3DEbI40KBBRTvQjKCGYq8u6bIRXuQzjYYi
BjFY6rbuGimkRqMOAi+Nc2wyZ6gRi6RptInaBGrJTS/fpWZbzHZMbtjMcbjiu6QxjLANGjJZ
jJZWByE1TrwnVAnB6ejUQUjNEMykEYuyb5BFw23SiffSIcOMZVruuEZqNGCjIRMNROgTd2Dg
aJIGF7rJOA+ViT0BPyi9n8PetW3Sz8Z9hfKD8oPyIws/4KfEoDCVWCdMKr4rk4RDmpsZJlFT
kKiWarToaBbJaNMiDJOO14u/jruS+Y5GQo6Rw8a0HPLIeKUsod0SDnlnyFAi1dEXSfl5qUkD
GDI2kK3HNmhI5G7LYTTSEbZlGNKx1LhGaOTVIasIJ/MMI6sHNQE4JbsPAD/4/FxzLMyehmty
ZhrgZyhhCfiRAd61qlPpPsAvGEEO+AF+gB8CXvwU8FL8ys/L6d9SfkU2e0L5BbGCBfwAP8AP
8As5+HktlVKFj/2+DHdYPYNFBIJ9YB/YB/aFHPuKHuwJ+AF+SPNDpoOLTWQ6uPkdCPa8IvEu
l9nq6Q2UgcsvKGN3oPyg/KD8oPyg/Ao9sSeUH5QflB+UH5Qf0vyucKYDlF/JziYoyaCE8oPy
g/KD8vOT8lMGYEej7H/DJijShCqUHedtoskNaa4dTimBti8/UM17xGhmI2nSdDveLEJD0NyD
arIjmmTI8mKNZhyiyQ7dmYhohiJ3WzRrEG1D0oSGTPiaLluwJ8yeCPbE1J6Y3cxlJGY3Uzdg
TPBSYnLcC6f8vAzzz+xmMHuWZDX3e44Nyg/KD8oPys9Pyi/o0vyg/KD8oPyg/KD8MLVnyZvd
DMoPPr/fo/YuXBbKD8oPyg/KL8iVX5HNnpeY4EXhliY8w9SeAZ/+APgBfoAf4Bfk8Cvy7GYw
e8LsCbMnzJ4we8LsWfLMnir85DIWdQD8AD/AD/AD/AC/kge/wvn8oPwu9HXhb6+fFGZPmD1h
9oTZM2DNnoVTfv6EH3x+wQJPwA/wA/wAv6LATxWYD5BatoBfsADLn+cB+AF+IQk/pmYeoWR1
QfVKLQf0Kwr9SkQl98LZPYsc7gmnH5x+cPrB6edCElO8qLstpngJsCle/Cn9MMWLP+XXldwW
pB+kX0hKP3ULg/LjzLIVGJwgV35Fhp93RdQ0CvikvktBFvAD/AA/mD0BP9Q0CkrAXQp6BW2A
H+AH+AF+QQ4/+PwKbvh4/Wk+OMAP8AP8AL8gh1+RzZ4IeEHACwJeEPDiMhIBLwh4MRkXARbw
AuUHxfeT4ivoCyg/KD8oPyg/KD/4/ODzY7pjcbf+sstFYdq21AWUH5QflB/mNwvU+c2g/ArU
Dl5/UoBQflB+UH5Qfn5SfsJNmzCladiWsKh0uu2Oox3N1IXJBeeWbtrSmx3PTdNilmFL09J1
RSdHM4TFDWrSTSYsb/q6wUiScZ3RK3O8TbopaBtSSIMJXxNzJKNhu2k5usG9uRuMdiYcxxS6
KSV8foDeT9Ar6AvAD/AD/AA/P8EvcEq5qxl+hCa5QTQWurRh9YTVE1ZPx9A5/SQY8w4haXRA
Y1YbVk9YPWH1LHlWz8s8sTVy3BHsCZcf4Af4AX6/Bb+SavUssssP8AP8AD/AD/AD/AIVfnD5
Fbi58PqT6w8uP7j84PKDyy/IXX5FVn7eFf9nak8VdCM0hxkGF7ZlGNKxvP5DYZuWzTn5EJmj
Kw0M0JTsPgD8AD/AD/ALWPhdZp/fJeCHog7BAnXAD/AD/AA/P8Gv+H1+hYOfP5Uf4Af4mcJU
lnRFTyGlTuk5lE9jqurOqklSfg9nTEqmrjtq4ZTnQ3YBw7Qtri4f1WTqlIDDbd0R3tKi1CQY
dwTl9fAflzIZZQIJISnNR6UH0XomdyTlEEnLZsy3P5NyfoS06CiY7muyDG4Lw1Dbtn3HYNF7
gxKJGKUaeTdlGxbgR53KNUdw6XCdsqkoxUp1jtuNFz1xDbObYXazX5ndrPjh5838Q5pfsACp
OM9DgcpK9NAj441w9eLJaKaez1/8OHdeffaG+lf2gs/VsuoRRv8uXMW7nYw3zrvruYv87Km0
b52CD2rWVX+p/Xv/qW2qf973F766jb/y1M5D+y3VwTPM8zdPf89Aer5Htah/FYZ5elNLT/rX
23MvfdLTwzyWR3ikh9NftERMwRIXtRdsQb1GJBcsXXEobSONtnKptTTa71/pE9++K6V47vMM
opbhngHUql+0b82T7hnsubtg6YtfqyTT1u6hz9X+7qOjH+7p4+nnGUot93h+ON+PntUZDabP
aX9RBe+GFmwnYoRnhCdRvQv3vZa6n9a4j3poEG3LXa6C6TFoGeEx6Vmn/mAXvFoFWyoprxFD
qRd//Gb9dlRh7pYqeCIucYWFXaLtwqaCz6te2Eh/f6Z+VVnLelRK+t8P3HaPh/3d135MLXdF
H/Vp7xV/xxHMpGWT6d8M+hflrpeUNMF99d4t6Nf7xjB67/sNFPrV3YTvSa37W4+431rgFz6P
ilYfFHxvd16w1O3u3z/djwruS6pZu2A5988aFzfQ+zB6eLvkxw8L+/1enuUq/3gc588fjijv
ufW+QcMHp/S+r/e9fxv2t/uuoq/w4p5W9+iCx0+nUopQkeBrvnCJgiX/99XLlf9t++lddffP
S/ey+iguQ303v3Zc7gYKni760W7Ka33zpry8pgUfX/yefpRJHk8i/SvKQx2191F14Pkd5/d4
4m5veVtL93u/KewmOuqPPX/2RISrh3qOoEdkdKR6lI6OjoouUzompkzpMmViylYoGxNbPrZM
mXLx5cpXiIuLj4spW7FSxbhK9Hec2kiYWjMisjStGBdbJpZaf+fjfK4nvnTEZ/RfWLwnPD4s
Ij7s/DpPdfdQ1WVacP17wsIjIqOiS5WhT/8SF0ZvI2m/0aWiI0pF0PcfFh4fEfknPapicvvo
3kMqZT72j8q1jVfWbinFb/nzHWl7r73v8TePHR83959VrjOtFh22/vWJfaWb9xk6njaWcOFO
vH0WFk7tV8X/z+7VJ/Fhf9LP7/SUjQijI42I9zTznPd0zPWug2f0AHoAPYAeQA+gB9AD6IHf
0wNhddJqn7Qzhi7kz8w/2mfvxmfMiEpz3rn1q0GHW7+3p8ypL2o+1u28583YU+/cfU/1nhPG
9nqw4XlP9vrznmdORhwe8mFEQtMtZzJP7XJ2P9rqvGdChfl/e/XDjqO2NJthXZ236PCpydd+
cE/5Jz9sMWpLx9TDIjrj9xxYoZaN1vXBx+bNrvhq/2kn7VKzK006cHjrxJx/n5hya17NUaez
m/ZMm3zj9KZ/rX7TpoMDvu/89ffZnwyWbT6fvV28cHJBg8QjSY3br258R/kZZRIP3Zm7P0Wm
Dsw9YOa/NveHtTlDXvns+6t2PHZgk306YkX1W0Xbrzv0/Pbls5k7pzWo9dq722sO27T2s7f2
Xd263Sct+NmdD+451Xx9+1F96zTOvbFQB17IhSI2zdx39T1rNvFOTYd8bx65+VzusX3Hq2/W
nuwaM6fB3fsqmHnbm2xvvb3pwUGJtMXl4xd7jiY17vB+jdph11X/vFS1zHeyhs74qyfpuorP
zrph1uSc7NH59owH6LDzmr4ycv+KIQ99XqFF9bQ+X6+u+d0Nx+bk1Xzu5uufWHrbuk/nHJwy
5ptSc2d9tkQuWFJv2nH/fXVh7+rPrn1n7/fdxrTKnvPce/1Kbcg73m3M9sNvvV6+Vr85i2/+
V/6uax+Oj38x5vA14RkeT/jW8ssjVni+ShKex8sPj5iadCBFvjfTINmdkeGJfPCug9mn3hux
NfmTCo1nv/Vxzb6NU5d+XWrutIaTqqXt6XDzsE2v31GhZa3K73T6Jmdh+YdmNUscNfj44FfS
Tnd+8sNa74roXOqyP/wYcfqRimvfzn+3Wc+EBd8tb3720PKosaNr6VNnrf/mo8lncg7XqDtt
S0SDLctWH2m15LFl6uKoH+F+S1vL5V43/vle+1OcbWXb5r7tyWiVmKiOJsL+4Hi1jSn3v7W5
77HXN6T9e9r2dmJ3hba1rtow/YO97Ts9zwep76nBk0tvP7hInut3NvPztza8uX7K3rQO3R6q
v+satYk/9Biz5PoN/XOffffTg/XW78z5dnIzWfH1Gp8veXndkpdzcrK/Tm389uTyy2OnbZv8
v99QK/UNpY6f2j35nay0+6OTPBWTXQEZGU6v4Tt3i2lZXz3y/Ka9Dz63vkONnO8+GdHUGXN3
grl+bfbSRn0/SRy17PSSO16rl7NIztk3fUPY4XlVKyTIZcfrLmmc/8e+qLB6ObPqzjqSUzd7
5pq8zY95zp73VNyferBh5uM5/d7cuahN9tK2Ww5eP2bHRHrsaJlV+dbW+qL7szp1uV+ZNqJe
rNGvVHrY7jlJA+3IGfctqp5eql7m5qykME9kpNvJSUlJ6nXF/FnmzCPVWk07PfLswYQn929q
v/ONxT8kH35rf+qGmTvi1ZXY4czkr3sf7/ZCnSe6bWm6UP28ch69Xb92dvlX0//Q72vIpr7L
jBEdps5cN7n/9Eff6zct6+yHcftGnG25sM1nayd9t/qBTzYvOTd5ulk7fXxKzLXZV60+2ip/
cWPfb+vJiNc8X7US14R3VF+d+nFtzs3wlC7tNeBkZISrk0ssXS+s9Sa+if7trrOVrsSKm/fe
O/W9GgunnPekjDq2ete9UzNvXt7m3B0VelSN/799h6/a0vqbhZ//QHfEdev3DfJkqW383keF
qvH7Zla/eUrq18fTpy98pNKiM3SrODhULhpzsP7+vgPWnJq4dVaf5bfMi5u4LVyd14jRU6Zt
m9poazna0U/3jGvCW8k7y1sRTyUdSszwlEl83HdeTxz0/lH6iYEZ4zI8HuuRSZMeFm+uy5n+
5abMz9/c91Fe05tmDbn2zNz8E6WWxk7ttXnmjtQth2p1adZsRtMRd61ZefPMzqdaf/Pa/D3l
c3/viXkqPLV+xParGx848cFS/cMVNV8fm3T2QGqnSd07r16xafiHIufl3V3+OnVLlwl0KVbL
aF9t3pDuh6sNf7Ea7cd7MYpSo5JXRy6ovtB7d18Qp+w17lGQ+cd9jb+uozK8ksk2rU4DffDw
Nzf1HfxQ6vTu+s5vp0+Y+PXe48+tb5S2t323B6YvrP3aiG596naf+/oYupPkf1qhR007wRza
m24lD2QPLJfhbqWwTxXGr1/9dfaipRWWdl+4ftoLHc+cWXT76fYJ3246+EPyilviu1SqNnVG
SnpkShdRtYY6JXWnolO6sdSosN0ZA7UyiQc6O3QZRlShiy7xujPupeehW6I6irDecXEp3gMJ
iyv93b82tc5rPXzq2sNv7rtr1zVkTdqY/vWZL+nyqz7/njFlpjeqc95Tt9Sq2Il/Pb58Xs2Z
L2zv30zvoTZTyEffVw+/lT1gyYLsWWknuT0xY+zdU4a8c/KZd/96MIfZOa/Nr5S//MEjFV//
a4u57y9YNm7BtoGT51qlb7Q8cxs0njLt1Klqw7N850b3Du/XNWOI99YxOZOMl2Wik9SBxFVM
do8nrFJSsttA7+LpxlIlP1afnvndc+mfnZiUv3fZ9L5Vq+VtyW5QOe3W03+96aOHN9z31OFJ
mx5ptqnq9Edjvum9v3efW+2E662NJzatXeZu7zefqv/r6kerZ5frfObRVnMnP/BsqQPOnKob
9w2/r3nbmj3qnNrywdJGb1x/6+Smkf1b0HXYsXOLfgnx1TI6xyf36pQ+KoYolkF7WD7+JYJy
4/fL5V6ftL+zs833vXkeL0M/NPoJho/yeH9i4xKz6L16lKbbSYwn8U+VzPcoikX/wJwxavDq
Fx6IvWfgiKPdeh5aveLo2v3LN888XanmsDbnknvsqn6uQ80tj0xvc+jFw83KVPnMu5FffQ47
9N7d/zzbLHzIySo77eyZu18+6jn794cm9nWeFis2zu7Q+ofWzvN1zx7adNfghxPM6Mze0U92
/ntq6jUTEsKap1w7pPtnOzp1aaHcEnRV1i01quCHNkD90BaOr7Q60RMe5ruFJF73yWDfj655
gQE9LK6cMu3Tj/DqHXckf1hKzsrNj62Zk9aox/FjM0YvG/Flg0Z99uR3fGD+bTHf9jp+z9Pa
6Rc2j+40/71eS7tbHTq26JjXul3nKkm/eoIeT82br1934iwvtTPtPWt4/5bV265od+Bghbf7
nnz20XNNDnKrx+KXJ+6ceLSccSB6akRKTLmkutn1jQEp81rVj7jFk7Rk2z1ao603LaCdNEg8
TF9f+VPjB5dJcT5w75HrvqSvLKMVDa7o8bjnunHuH5MS6VvzPkonllmdmBUe7nk8KvO6FE/y
NW+tX7929t601ObnPfV31NxV05r9Vn7VZxKa7Ms/kfDa6iaDbpqU3cDq/d5zPW5O7vFF/Xuq
9zv45vrs1SdmT97h2+IlXyIOHR+oZ7557Oig/tO7PdjamfPcNxlj/1xLnz57w0L92XWzjtfb
PfrWftNm5NfPtTxZ799YP3Hr1FtiPVtja2T+w5PYqUvUxvQWw6ZmJnk8XZK3ZjyQVeOzUq2i
00tVW7sh674F1Q8Npp36sB05I4mWokfLFu6Lekr20M8xMlJ9lZGeJE/nZ7PTcvqm9ek/de2R
tfv+vatG06VN7l/a84W9Pb6oKcffOfN0avumhz+IWjq2/ICGM39oa1kje/bMWJL14+Yu/qPC
UxtGHKxVbv6OPSf29U2fWvdw8wcWnvi8wv91mjRp6qQ7b7aG9rh+6Kic5w8sujulWnQW/e6i
khe0711lQXyvasm9KrcIjxo+b8iQDzK79+lF98OEMDq/eYMfePGajNsz31w2ZAGN+eUujycy
4m3fzeVqT5x7BMSEgiOJTA5LiUuhIUySckSF0ecReTUX1bz++dytz/XPadxp6dfq+txZZ8vM
tTNPzh1E3+RpuWtJn9b10/ve7f4UaQeXeoQdH3Go5vxrx2TfkbYob8O/1vTeOGfOM9/NalbX
Su2emtYpNbVTx905OR/0Hf32lJjJ5W5dYHm2RSRFpMSWmZfSa9n4pFc+i6k9LnfxltV9VkS0
fUUNlGNbNUopf4pGKIeviahyT3nLHaDojTPU7aVVojoE9UJvPZ7aI2PcV/X3RE+lmr3eVpdp
Rqvw+TM84Z5E1ew51evQyRG1Fm7M+e/8zmceHn1sxBdHZ+Z+u6XZhHNpH/6nFLHiaOU+HSo1
rbd1bNpr3jXc1X58qvDIxtVn/zr3vrvqzV2U90POqkdvPHv29ZuHje1w17M5ffumz87L2933
7kU0Hnlzbq4Vv6NaRnrYgvD4Lg+3mHDnhM7JWemeqLjMrvMHbxzV8vn+O+imEZUxTF2ao0ZF
DNlx9cJeQ5Ykq+tTOdw8t0WeinT3m0Rfk3o0rzwjyf2Dvtu49+PKzHAvUc8OgmKYJy5KLRzl
6TSv4ey8A0ev6ry9+UNlj9TyPFi9vNXuo029T5z3NG208a0RZyZ/13nEk2lbquz9sE3HzfmV
RkRn+Lb540utUtNPjzPGfFR9ans5aeur3z5KYr9h4ti2Dbl6iGefXZP3bfvV8Quin0oI66XO
MKvzyRapLf8RlZEe1zk6q3JSQlS6KHv/i/0/eD4z64Lrs0ajiCoRU0nryI5l2+6h3WVEJNKz
GpJ5v53w0moc5n1MLO1JzKJRaHj46PU9E5O812hUZJTnzpfL3tOhAp/+xNKdB46sOLedf5P+
9fR1bfZ/eezLa8evG5y9qNnC7tU6Nd+8/L39NdNe6+XbXMELDfwnNmlxdY97/n7L6uc2bP+w
2oZaz3z7+p6xbRvtPllwagui97TMqtaxc/S8FDqdalETUjumX33nUwlx292Tazx528Dyy6c2
vkMNM5eVp9FzRbpAX7ynbEd1dfY6kMLomvRQuIR6+EbPnozrxhXcQD3hdbJcCCaW9oRn0TKJ
N2Z4YkoP99x5eJf+j26vZL/Pl0Zd/cXAWrPni/GLtjTrMmff/EX19n971VU7Rj5avcmYektb
Xq93p1F4w9IuhdVuvI8K742Yvo4/eXDvmZjznlUzz+VXbPZAjXlnXj+w9syN0zcPLEd3ym2l
t0XcPoV+dCmxnvfr31Lulillp94yNbEbjTLD7hRRpdKjn+8fnUs3zftL3R62ewbdN6/tlZY1
eBGNNOtG017Cwq7zJKnX6yomea/OyAsGLjSeiUuhgSgNYLZ16J7kiascVzksLMkTfTj64SEb
d7YcfoIPffXw9B0j0nJy9ozsnzN82ohvWwzt0+XBH+9LtGmPZ0yt+NPjP6u8+S/Xd2ybvvq7
7YOuav/Jh8tH//Dn46+MfFY91uQd4U0PtF9dZUH0vKT0yHStXL36ESnliHWxpRfXqz8ya1vi
snJJ9UtnxbxC39Dye8P/k3JTL6W5X0p0xyuniAQxazcsG/pCVi7tL7GiT+u8nUjv6DGJCOf+
QU+1w1t51JAlsUy/iOSk+rVjPKVSiB1hyZXvPBxV5VBe28eN02f+/d9OtVbvcca+O/5A3a8e
qTJm+NkOqacKtqBew443abEvxulRa8s/86v0PX5tq91s/+n5xx5ee/qF9CM5A5SqPjQrJ3sQ
ndZd6U0rrf96wSk6uZfpR7YvLJUAoCiQQqOwllkJYQsUAzx3ZnmGzes9ZGdmd9p8Z/q2dk7L
PZVSLpenOKR2xj+flEvtiR6f2snLIKzTo9WkRZMz3L/oKTyxZi8lfRKrlfaULpXbMaKXJyJ7
TxLddMPjym146/YKWt9hT1w95p5d6w+k/nBN3Ye/uG+10+z7EcPyj03oRH3w46NWrXXVH6ow
odf3TbQuJ0c89sPzlVboZ1NHPkgiu86RYyv2pfVJ+3Dq1O6p+zo12Z5658kGfwpfFTc+5aaU
chv20RVZjzRprLoiY8o1vz+5RXpk5+QFURntK5eussBT48Yd3e5/sRMdUrWMgTMemJfVeGu5
Dbmbkvaq0ebw4e4V+ZMK990ml7188MdDSyyT+MKeKDue7o50MUbOaBoVVj96X3iGJ/azPw3M
bFVl9Y7UGSNOdnhxiXFmyCNHT47obL+xfF32nEd3dDo14YJTDDs54qtqa/f8u92A1IUb1q3p
3fuTo+1GnpiWdW701OlTZ21Yyp9d91zrbre9ltqu5+FP86+LGBK+qnT9mG30qk6QBigf5G5L
3P5k2IKoCdUm3PmP9nRjmeDJ7OK5JqsbmRloR+7pzR/8QNY1GX0XeymeE02nTSfnven/OEpJ
qphLX5n3Udu9dm9M9GR4MuhmeSOJ9J1a7YH1JoZPmZr74hcVyqcP6/a3A3s7j/146t9uPDql
yhjrbNRDST8Nczylnph0vP6qMu90em5T6ov92+ivDR82sdTJR7+Nyzve+r8j87Z3WrK49syd
k0d1oLFku5ypb5Z786bBseGr6DayK/zNed6vrVwSfZlz37zpFiV/aqxLiUqslhH2qqhCV+a1
vVLCGl4zrm2f8OmrpjYftT0uSp598aHvn2t4fOPB8jtGfvFSh+w+Fc6mVOhbU6vRftSASRnD
p7Tun7gpaX+PPS4l6DzDyRDhnuwTn/r+KB3e6rrJvg4gQTEuPIuGo+pSv54W96jfaAxdYOEv
dW2z7sP3Nr2zz9o7uen86m8tPO8ZOPnzM12PV/l+2E/fbPWhdy0q+3TPStasdY82qe8czHm5
1Mmx1oah1QdI5/RjZu/2I9a+9cZH004eajq2XN+Ww/e9dOvtKcMy0qM2vJ8elR45MGxB9D/a
96o2nfVLiOvfYkLqwy0mvtpwaultiVnbwifGvDI2NyvaaruP7j6p+3vvXf/5wl4jhpzenFBj
f/kXRk4fVr9m2R4Nn1u/Zkun6x5qeOjf8QfWrduwfva+fakdz7zz6PpKjY8Mrj3t/dgvvh+X
X2WLyH715VO7aj6qXb+O3f19kw9ueKnDpm/nl/pPxLp/v9qs58Ntr7u1y7DHK8wbv/GfcvrC
7h0e7nhqSYOTH1X5/ODc1QfnLpj5fHbY5gW+6ynS7bu2Wb47w0XdmUEdrhagKypsYC79kRV2
zZSpG/a91LXVrDP//r/t7b84NrCWiMvr81D5qg039DlR5btTP/Zm9IAljzaqt87VzH379t0S
v6vW5jF/2Vft9Ad3f9Srdf4Taxd+73y8M/Xs0NO3HvwgrdPbL7X/YMaw+UkDZyavbpEeRnfz
bdUyq02JSFmwrFxE+2VWHN3N6029pV6uGtir/lwW41m9vfF458yswf12dXo7r++QIYeOdnnh
3fiNTzftmL6z68DPGl7Xc3PyvZ+k1J7d4svIDf/NSj2wdUvNW67Lr+GZNfzzMu8eyBIPT5me
2WSHs6L9/Nu2Jh99c//IyebGN+dXbLxx+5y3SbzUfWLD8tHt7u6Uvu+Tpo/1WPBB7QWz1x3V
l6tf3CxfzySqn5t6TKqd5b6qp/BEGo8SJeiCpHcZdIPJqvxludxF+9qOG3Dg4KH7H/umSZVH
7mmyu+Hx1BbNSs/ZZM0/PEOt5z7G3noqc/2Ad/924uxNMS9P2pT34RT9bOWP24157/+GWKff
6dJyT426ZyJeTNyVftNgddvstysi5doUhbykbeG5Zmxpc+6b5W7NMsedGTdOdVJM2f192j8z
f9bLr3VP7PR/G9cvrbkkfX7bybzyx/euTat9b9ZCven9X9ZeN6BX3ani2/ATh5dVX/lZZId+
mW17rIw7kP/GkDvyWe28Fks/fLXefd88u719nYlfRy97RT9W57TzVPumI+8+VupfsY/22aK3
tWs4j+2+edG5VksHVqj4Ttq5k4+P7pRw5osKrQfEd2yz7/6ZH1xXucC8EVfGZyqNTPpJg9CI
NjzZE1lZDSjivD1RpX/0nk5N7vpu7oBPD91w/xO1Xjo2ttYNMTn//uGglTpmbrPI7Rt3/XT3
eujmH67vval6h0f6nFoa8+q1566edN5j7Btw8tQXWxvdUf7J8S/dKDy7YpZN3tXKqhq/ICM9
osvDrj0tPSw5LS49rM/bNHaNS2lfOaxLRpNM/fiCd7aMWrH0xfurnHhlgOqyl5pPHrVza7nm
Y5IOHH4/oXadQfbKlZ/Xrfxxz+SEPsmd7r1n3H3fL92WcO2Lb/59duk2K1s0OPK32J5/uf1P
/afW+W5yl4eYHP7aP9rXmTlp5vLuVeS1Yx+f13l4n15tjg1Jnzsm+82mnbt15S1nrh6279YR
0+46MzaJDHJNsus8tf3O6uc9Zv/jEzrlzO7UzqrSouO32YM8T3gvuLLkHnC7acK4Vgu8/aWe
EzMqlvYsSLyRPlTXHg0zGyTuuuemp+0nJy197Lnnd7Ye+9ZbI8a+N+7AvDWpnTa8/PTw+fk/
rlxq33nPbTN12bbWs6t2bFxY/rxnd/Z5z4FubcbePrX/3x/bGrZ1zohGHY4nv/pg8uovJ29T
RHuffqNTn6l0J936lHGyQ+v0sBS6+6WH0aCkcvTcOn23VI3cmNf+qewtuvPEiaob85a8+srC
WQvb124QvqL/2bgG19Rr8Nid+feuCp/5Ran6O+s0GhgbP2JK29wuo8K77Hx7iv7gw3Ua9dhy
TdjAlZ/06jxx5rOr/hIW/8GeNk3v3RY7MlNfcEODo1WjDhypGjlr0INmZM7Ewwsq5/eovr5z
amrzDfmVeo0afPrpgZO+O9m2QbNN1c72SVHGpS5vfNChB3Xr5LDDcxc16fx6+eut8577h58e
GNs/gzqCHGNudyRVHP3TEJ2GfYoo9LNPdD8k63Ar6/1OZUe+f3fPWqLxkiXNRr81+Ifp5d/Z
O3x+9MQ5XW+5aatvOY+nQt65Gcf6VH3rqbSPv77q9Ig5Vx9wL8tjIxptabv42hU39/pv4pG2
sxJ3UWemTH5fhJvlbtmXrobm9FsmW039OlOT6ie+T4bE8MXm9m4n8sP+fnPao4t5y+qfVFr0
TbUxHz27Lic9Z5CxoEXTb6LnNvxs8so1nau+Pvnh7Bve+eylV5v3fD9h570nIydOPBl1YFXP
wZUSZrSaNHtX1SXLan+cn3dHfqOWWV3sZQkftno/tlV8/KJWDbX/DNpVvmvXt0tP+jxWvybv
yzL/V/VcRte/3B8168GBZU803/zE4Ls/OjJiTeeajzY5ODTGWndo2vaN4r3BD8ybtDdvXdqe
1HYjswfVKnN27WfzajWc9I3+8hv9t47tdVjX17QODx/oI7YnsexPwHZ7NsGjLLnujz4sKd2O
fpVcnM9fd3fPa/XW+9Ja1mi83e7e7aGW2bVnTk5rEJ8wIfXHzi218fjYUlubWOtuXPXR2ufa
HctLPX3VrHP9n569961+X3kOt2p0Cw1RaBS8OEnED2mSHta7PY0llUKNUsOu3tGZC5KTs9on
TK7z7+WjP71zqHx1cN3n6pc7NOrhERbp9we+zHmlTfaJ8e1rJq155Xh8n+Q7tqyYn5eQ/+DK
qOV5u5MbJK5cuSxq1Yzui98vPbVJ7orvRobNT6p9fMRrmcPICfKn/rujGnx5ImrizPyRkcs/
GfR2Qm7XlDo39KrdcMCDe1Y+P6hq5IFtCVujluYPvm3utUvzrp41aFFupUde/Dy2xYjT4pvO
KzrEb/1uTNju586ZY1fFzFqz//P3Pi2/7e77vv6Kk2XNHJt0NIH8sDnKD0t3TfUIi6uQ+KPR
mEaKSZ5Izx3NVQv9Tx8v2HHn/F4jOQ1u+dLybaffu/6+1fevaWtVPfX63DeyameoZdzHySHV
K7w0+OwHXdLOfRy9pvGofFbhU1lt6fiaU//5TfP7S7VKfrXXNZldJtC/jIFl25BB46kWE6o9
TDrkzxue7BwVPTeun947KjpzTRO55IHlLU9cdWDmpnUdHKdRhw/z+n86uc6oiI75nlcqLd9R
9eleCfn9I554iDVo3HLPKwPC+i27Jr3MG3/ZkVB7Z+aHAzIH7lk58bOoFa/Nf7/MxJPLaj4Y
NvLBxuF5I8O73hVe++RDgxssP7K6+utdR2b2f6NrZvzW/4aNHJWbcCJq+XtrKl7bvWnuyk/e
uC3847ZZLRq1WSsHvbQivP+a3blPPNJ21crXMmeundX3VN66b6eGffDchr5Tj9BF3OLc6PEv
yZ3Dv5lptXg1X5yJWOycrnJ0SnzTnPyvSv2l/+jDiV1ULzeZcJuyrxQ8yF72fpxHdXEY2Vqo
zwdG3bWjZpNth296dPWxss0GbLzvu/7trA5fZj90TcwP79xYsJrH02zalvFX37O5z00DRlfv
cuxcldZjyxlfxQjP4da1V3l20U9+ca6l7gRzN8yfTzZbJc5rr4iZUtrybJ9B4u7GNaNvP/T0
xM/j39JnPdfui2PLsxvF7K98eFHMysOJ2xfP37yny7f5g7u2HvZ5KW1lxLFt5bs3yVh1146E
/lN2lZmf0mDEjM4TdyatWPl6RpebE1u362V/m/lu/tsJibE9R4bv7pqp89YDVtdo2iis8tEF
2tPLx6xNa/j6t+E7N+xZuTq+akTnrXtuXfxiwv1HshImfiC+iHq1+eeR+UtmhQ0YsKBB9neZ
5tGRJ3eUmfZ8mKw7u1/ZzWXbranIjt/47HONcuZtTd5KvT1nRXy3ketf3zN8vmh+eNIj3W+e
07lG3aWxlW7X+z97dPSDe7Z3Ht5hTetRude/GNf8sZ96mu4OkWTxWuYZ5bsrN8zKsK6ZvOKe
CtH33Rv76H9GtJ02tsGkbhue7PXehr7NcswfMn7q7Igz7a5e+12ziaenVVm1cdZ5z/qv30h4
5Zl6vW+9feD4F2N2JW5Ld28Q4fUjbqd7LRkOkm6s/0CLfi3oRvFijZffyp784BJz5wuP7eq2
cbY+c2nCvdU6XJO0qEWjo80m1m/xzdS1Cwf0atA4s/LHCxo27DyH1W7YaHNWh2pJ8fGrkmrX
uT/qwBvfh8U/NDjhw9tmyOS0Rlujsq3Z4QOu+Tz23u/fjlf31qVJXVssPRh5786Bkbe2/Wdk
i/2Du7Yk4OmNd8S27lI/Nt5q+234xz3C+t6wq0z8Z7GN2j4fdv+RmllPT/1u3Hfh69ocbTxu
U+ON6yomJmxZmXHfmfC8/vqnZd59sEH/qFV/GddCX/rCnrbV2/W6+6Me3yU10Kc83OyjtNTW
92cnb+VXnTr3rwrl32jcZeyd0fP0zE4731o3b+v2sUnbRlc77+k0vfl7/We3y0tYVP32tLP/
GvhD2JRWiT92KA1uS8c8PUNZij2RUV1Le2K/ipo/5M7FmSeHPjF3f8N5e/Ia77tbv3d5+9Zj
vjpdrllKxo9reprNOr0xdsfp+dX+M/Y/sRUqHXj33J2vPD/mu47DXiKb0P4tVWjQ/0W5pKm5
VrVxOZZngRVDWnnbVfVo/F+J95uS9dW7LbvM6T9l8Z1bHxta855uXY7nzMp5Pqpv3dNvi/im
GZOHbdVi7735WIP5u2MHvHcwttrGGdet+zZqZUaX/NE9dic1H7Akt8uJ2H47Ku4c8GBm3wY1
cieeyB9cP2rxgw3EsoTdySMH7Yrt36tB01XhdfPbTRi384GpGRPXDPCsPHLzsb+0S0r/MPLA
pNn9lyV8UeqpL2NfX/Vt2LuVXlpSrmvPmdf/Z0zmyDHnEvu/nnHfpvnd1/at49n6ffhOz4dL
slaeeiGrS+PPI5t32bPm1fQy7y7NqhRfaeue+w6v1ju2WHHeM7hvv0mfkDtmTd3Xa16X3/Tw
7IilW/X9R9tYG092qDV2z7Y+e1NfGlGlw6HW5yrGnvc8sPCL/c3bpc/N/XDLkZmvJSxp9nTa
2D1DZ9Wbf9uU8C5Jvk5u7gmr8KeU8qrPw1YnVI7bVXUB/U6e+qLCM889v/2Z/x4bnvB2n7TN
X/dpPXrutSdbzhnjW00tfrrW1vJl228w7poy9l/h/c57ynVyRyr77tja6NZZ5XJF6cVJxNEa
6/pVo4Ez3e8zUgYmlk5eGJ4rWlRJS323eeu88dtvfu+Gaq1Tp5yY0Onxl3NezX7169f/M3lb
h0W7Ypuv/09Et+df2/P0VoLfp1V7ECzjD6yudurLyG93Jk2+d/Havg0ORjbP61z+rjm3hedX
Sph0InzL1j1dP419d/72z6K+3lX16Tq9ypwK39Lo88g2391TalGmvWLfni7vx1be8EPuC7n/
+Sxq3u6olasT1nRdFl/jhsENlnwTvbjS1qQVh5ZVqvF11OTRR5ddPy9/gVVt1DfhOz+LXkWc
GLeu6/y3Kzb6JKVn5/Br2/y12swpPXJb9/8hTCZvlM+uffvAK3xkzhm2bP+sl1ccrbnnodo/
1BnxxPX7cv65umbN4z2GXvv0nmdnDVm9oelVO2bKbjfmbGlb/oZ/ztKPD63SgiTx4CPZg7pb
nV6vntqh5/h5p97a98X8icfve6Hi5kND/mnta1m+59+Pl2/9Td+0unQ3emVa+pChV63oX6l1
Wpurhq3vtGTAwfllKr6RtffcTOfgn9c92y7m7ibNMjec3HF66NEFe4ePbrKhZ62n631TZW9q
6ohuxzdVP3nVyTbxuvX/7X15XFPH2nAIRMQoGtGgyFZQECUiZUeWcIuAylpAlrAZKhBCIAoo
IEgCtbKDrQs7uahA2VG2YoCgAayyrwrIEgVEFIjsq9+cpNza3vb2fb/f+32/948mv5OcM2fm
mWefZ+ZM8jQrWovWF1XfXv9y6ZiSw5nv2DHGQwKtZM9l9e+cVa7t++FWvLuBrM6hAKHI6yai
lTfNtLr3MJuz8H5GurgnAdO8r4U/wR4E1Jw54ZHldlxpD8teRkFINU1BSGhCqpptbNynili4
gC6d1KZ2HGmyLMdYjp6tDVAoy3WdHLaw+pD1w8c25LDpHMtiJu8j74uR7oJ9c2Y3JxapGl4k
VmTitMg6Y1y5+wDjEKSVu2C7sOa7GbAtjG1bYfyVe2CeN+yYffq9P7d0V2XpWo4E65juCLdh
dzs6zxpf3do5CZpsvnQPrBjU1QjvbOp/j++9Hjqtb7ZsI+ScmO1BEJPTq9xbCQ4wCzGoA1He
3JZ8ziIiHxg2417s2/u629MvYtD97pE5m+jrd7LIxSoZfTni3vZZeS2zlQUXbdGvvJEk0sDW
bFzr061xnW+RRBDCSWn6z/NF1NIwBZr+8L4me4b9sDFPOeXhYD+1l6wcK5uDyq59gyRe6kL6
UZyc7iyF2a8YU4kfXGyzXHHUCZi+BzJr5S1fYwJ66YVgeTqtfAJWIpzmipWLnJQk9BQwKhLR
xQrHhstLCTT0e0RWTzrFRzEHU0p3QPcOtQk7LVQeqlqDlRrcXoQzCffnppAeE5Xo6VAKCv0W
iSK07eCZWaqlBks0skuUtFyfiKqpJDEz8488VDmfs8A+adWsoo/X9+0M8kzscD2FWq76BPtH
jchzV8vkYdEzkTPB9sd1Yk1lELa2laXn7KU87kpICNK91Ec73+EtPfr6MNIfNULbrsdqKZkJ
3n1y9YuRwJjtx6SvJ7NumArKnFFiXpwz8e+8nUp8ffFcva9x855OY5vgU4WBeYWeqLVV5j67
oV0zx442qGMcDlwbLVkqVHVXqptR0hmKAKuI+8oMDrZIdBdJiLglZm+LGhc8zlLOZF935AtO
l/7+tdaV+p+895s6XyeniovFRiY8LtpCJit+edMi2qaiMFXewaPoRe+eZuvX+EG6R/JPrrdr
7J8s1qDZ4q4SKgmMmfio2QFDoe+6dU8v7O8bS5dz1PV05xfPt//STtNH9EUnyvpSuZiufWSO
rnWdrtHGcSZbxvB6i5rg6/2mcrcam75Zv/11fv6Yu2CuFN1B9HSJ7MakYWmm9r12FRZ4NCam
YqnVZr+w5D736jpL59DNn98Ea0cyi32TEp816G5LbcCoWxs75ZbISvBuScxKTEwusLYUIeQ7
btvI2/Mu6uF1Ef8M7KnHWa5GfDEC2fZ+GXJbsvID4ntMLPpyagcFlK7Mjr7NUKcbKSm7NE0a
HNK54FkreYrxZD3VI35anyHbfkH2vX3RVPfu7dbhkYZ9mbkheEb9PRDi88H2wgaBeZjDFikw
FdPHJdGlkUXxaWldV3vDz60eE7qZ/QnGyiqKcWafvILdNCMYTCKZvbGzdNgCbNZ6mJhZGzvB
cfRs26BO8ai4kvLhCbBerWJUgFWBDWzt4i4sMXmxxVFzow9+iBbv3B1Ifh04/dZjMjpeyKyE
Eeeg3mmaU2ihDyagss+LUaiQKeTzrBSe5wXDaFe7BCm2GDai1lxGnv8O8MvAClxMKxAVdnBp
R6lL8L6WChjaNUemmopfgevb+5BxTtjeckZNNTZxwuWMPhZTVkapeFQsb9jDe/sjkmg/7CP8
QqDWXC0RkRjZAYvoNceZJaIpGDH/90jiUwWFM4YkRopTMCMRLvWKJmwyj/hYlomNBSOtixSG
/g4sLXyC2cNba2DF8paqbVsnBrbGFSOJg5eK0dOwcQPclhj7kh8ZmYpHok2CS5oVxyUbLn/3
Rj2Ob7Ty9hmF5Lo0950Sgqmn3V9p8s6+jG+/HlZSfOHB8tW9kU+KlUTZ0dee+Aa8lJc3vTLr
axHuqNytFFjN8gncrSsd/gk2MfTE4YQQ/85r7rl50neaDFwxN1tHTHXEz+YkJksLHi4STLcn
oWOMCof23gvVmxm/ph563bPV7fiFktnAKdnY/TELl5UU1X+KYiVmpnxkWpoot6NQJop7mAa9
SUnhH+zl5WrNMCAOBbOcQXPEo0Ysppom/L2mw/4Fv5bytt351UpqiGzk7oyHkVbOTQIxZ0IC
MovsXae3uO8UvNrjpDuS67I/tYZvnpn9avf2FtOkVfUuECQbMxQ15H1evsnryNly5Llr50Ix
MZ6s0aw6YIRrkrIP4iG8F3DhwcL27BLJPufAzup6mrz008seP0fFdST/zpcu7dfW9tTrbj3p
9avW8bDXHMM/rGmkZw65RTBBfGFhMyyyEUgtFMM8mN4Kwgsw56nYtQMLZj45xVHgOYk4WNCs
HyNtSVx0+WbicXa/W+nkHv+btq6vu2OzX971xKNso0IGaV1fI1HeNDpN31YQ17wA7/SIhj9F
Iyqe7ibAe/tp6NkETEAKnIlFR0y0bY2INkLDVaf4PlzxQhL9KoUKO33MpdJnEKWVQkMziMRZ
+Ks5eG86Rd8/soeHNAgbnZjivb3h8hDdI6NHWnVkTBejl+FrklvjHlHF7u3wK6vLqXWOEK2F
KU8hnwmgym8jSq0r5fWfConAmQ5IeJ9qsTiNXhI6T8OUzoFekSSVPj03hftUKZW3SMKkT4C8
ZdnYDJ8l+yNitNd2kffsLCIinaGPexcG4voDPPezi+W/Ru5hLsKlz9iipR0rJmD0Epi+Mc/z
rNpdTkZ9DNM9hOzblNaSLHwP/LibTlPTlTq3mFODeSvvtptut14oLh7fOMArdPNx2oyU7iMr
huJZQ/57eMvpyDWeqAfKpH3dhgW6XftSY50fxuqvDPIk/ew6FyULhO0ulxQ/YK1zg4zPF7XX
6dl7YdLkWzy7D0vfNuAluD8SLMaOdhqWt7q49H9gtZs14PeE6v26CAt2IznJUefS96c8/wSb
GsZbsLNcJJ5/+UPwvttJQYRpsh9YOThLOxBRrAJX2SICPQsD61ya5871xtrIiCkpHdaJE0cL
GkjlFjipPdtW0pKbV5+X/NNNy9s8+BSCi2c/9to13GU4XkrBJwFdjG5DEgPgUj5FLtLPp+C9
iAr6TnW+UuPBqy4lwhRYBQ1diY6fl7TvfYt0wYQuICrMzxCLj/UxqS6YHliUP2iOlmp30XBz
x2KU7rUmYkrLVniIXkgXKWma/Mk5vvLbpd5I4UE9EokSUXxgbh6R7LcrNigKDMmTbcK4CRep
9DuIxDhKiekjbzCnQPov8vhgeNwwy1QUMTCs0USTihpURkSABY47Z/wRGQGYzJ5yWsk4zF6m
8wX61RtBp5IOzXALVP8wooqhIgyX0g6iEpbW6n6MSOHx7lzXw2szLAM7sTh7NioQERFPQSPK
K+CDWHpFD6NEDDYad8PlVKZmmOne3fzFWUHwEJHENMmdrooLnrnaB/enHhlTKQxZCRe6VbMU
4Dupzyuhn7mQuk22g73IG6e74zmrs8zWd1CGPcv/7Dm5yVhc7WbP0bt9victRoV0w+7OP6X9
arJwH5ru98MjLc5CwhjdqsJcHSG3pCDJAxwRglhr2AB63AXmyRPPv2H7SthL344rO32038Q2
YM+qfCnxRHePhW2Um9tsflg/TQVFopJImFosZmgK3t6FtOfBy6zC9U+OkVxw4GGMYp8eqcMv
AfNc0QXTtTWOoQ/mvoXD9q98JC++2PGBhp6AFntA/F/LQJosIEpXqCjSOjauB1HKEH3YtYNK
Kuzlq7DtADNsKrGZUfpU3jL0uG32+ACSWP4JdlxK9hls8kskIY2R/gqW2GlXjMlkZ9HsMZXy
J+djefAqvYMChEpM2SCjPHqyC90TzUOgO4/xK5g7n4Cv+cE7wcChVEAlbTCIQmQnu4oBfky1
Vh3pwAt074TQGKK0dwrYbW0i5m4+vG8Y7BGPlX3uUSwmNVzeP40of0RF6cIcFSrMMWJvRCq8
e+DgycFxZLYL5j4NjXHBEfKpPpJ2FB5sMXoKiXqDpMF4VbpPKgaNSUmKe3mN7qnPyVp4tzMt
Po2Zu5jb3ifz+MRMjGaJ4nr+B2PjoV6zJsWFz20PFnqcFeD0JI69XWEjs+r1htzYmn2Dw2sL
3LcHYuvBIzUQHP/TIucVWJYnocRHJQwxT14LJja0EMQOT+r8ePYEC98djTJR/tgu9sXexEwp
QKNH9SdYDqYgB0OnJE5IPkRP1jCMzcw1CeIJfPVjKvC+k1TXEEoFWOEYXJyD93vxLdRQcOuM
0rlieZ7nOehiIdRbRCFfQw2NdnvoFCKuhIwZykGnTJJtowPhxh5IugeitLa1WF6fIVr1gQ1X
btsBcRVJvBLG9I/myfqIKBgl40hXaReZk2hEqV8so3yBggmhkrIo+sT+JuGbwqYblBtCWcAG
wZyyFIbuiVWGv9pwodNKxF2qCFdpfogBtNSKIQ1l3Odzggd1zwOpWJAFi/IrbUxUISnDpS5B
QfkAWnKHtAcigk5FiYH5fLG4LwwsjEnjwvpkAxAVWE2eIqxtLI8XP9Y2nXaFise07dojkBhB
78MMiL5rOtd5z0w5/DsZ7+rMQL1RZgPYi7KmN9LsLvckMiKvTfRBUnDDld1gKczM7sOAmXPW
s9G3z0YM9orMJ01LPfrVysBj6uXeKHL1nUhfJZ9ei+vOayUS4XYs4hPYQBBtgPdCZQG0JLIt
7mVw+TG3GmMRGff8uW8lLJEK1BvR9SWKj+bi9R1OZ9FP/5SXdMM+og0tfZ+K16K6P0X60GCE
Hm1GzTCmgFJO0zeezgHb4Kr0nUIYOLMnTTAMqaxYTA0RsRh2sdEOUfZochqusI4dTZlmI0oJ
LjIYGrq6ikpSg0v1AyWVLnwE7+t8IdBfS3ask5IuKEQ+f8OPYfUAv6rhipVtgUX5CIkFMyrs
KDifAXT7cX55P6D9nojSsjJ4H444D8a40AAgfNhDsRoszkT6FLzdxXZCqAvd3stCEpnYQwUi
INxjKX/QDGP61dJEq5x6EFGuoXThnIN+pcA2is7AmThznPHQmbD+JgEKLpCHRHqBbr+fpYeX
2nDRx5lFYACCfcRlHm3wJyCOK28RdGrIMA2XjXW+RMPVJMDkL/Gy4a++EekCfQYGhafZxRyR
cU2e7eN5lt/sq3tWKpFfJA9sJsr9RvRdIdD9J8KKe+qnYcsvY+atbfapo9RvdZcpwua/URc8
pm0Rn5qykH3vKl5Xj3rn8fPO59dNHrVeADucPnvxjwT7Xvu54cGLdcUv12pHckOXj8nUaB0e
kCo7EE7ewYg1WOBve0Z+ViLd7yb7cmRhUuadm/ZGR9ThBQ1PjcOr7Vn4uIc5KnuGaOgt1T5v
+e/ZY0v9VykR5cMnqSTvRx6IbBo6vaJSnumzm/8OFhNYYa7yAnkZMUFiVIRSRGkXNy4jKhrJ
RnR4s2oCJkRBDY6XxtmiXSsGEZmqcLmaV9jEaRjuVFIE3AdWku/EsMcAcVdiiqb5pmcR5T2D
2NGIHga9okPBB4sR8UDUYKtZsFIPPmeyk6MqRTqEtIuvgVaezrAfoihgFuBSfU1AZgnaeqR7
Q2A80w+EMy9VYrRhYJOhOaIMOGVYhcfHBJx+GJPYcSJscooiJV1L32mEKANusOweuo/YhsYv
ljP0/RERpfbYPtJuJKqXxEMaddGclCzv6IErkKVegctihTMMTIEkDHkgFKsZ1l+p0R1/zeCh
4/hT0bxm61Xlj42B/Efycn9c6XbYV5McZu1wmf8I29UlgD1bem5okjS28xha3DfKxutA+/We
n+IrDYdGBg4ofJ992sdqPTfb7oazgZQUZhd4XPr5ay0+fqb241rjTHek/ipLduYWs3dc+rwI
5+FH0MWXDl7dwZXKxovpCdKTLt88eKlQ4Fhy4ap5+H1/62i1wpDHN0xvF6ugQAzhAn4DKE8s
oJTVBTlsHdhaVg3Ek3PQAKzggiBUnKav74d4zzdxD44rlmfqh00YO/HIvNJzU3khENFPO3yo
NN4cRyBjSFLawyXCKdTsM1TUOMwsAMygvtlR/g5x1zadUoJOkOnsPPUCaWZuF7EYRB3tJ2M8
al1wzjQwrog0M2IZpWAps4OEjjeXkZr1pug7qXahJbdGTEray/jce4qp0h8QHuDTf4FWnUMk
vhcgBjKOdapRpDCrkjUz0tkM4WL0HDSWSQRgHoUxCQNbP1LsOgZdfIBL7cCW4sydaLh7fglS
6yGMnhS/AUEnRtV7/jMDMBy1TXgQQb3cI7nbLdm/MCdiNsG3SOWaaWco9mKRisN6YpTra8lx
R39josMGrLl6WJ/ppCdDersdLCC+26mj6haFd/OkBNMdFlSJQi++mUh+1zez859P1nRV+oU0
bLRx/QuhObp64XeeMLLkMhOjeT97Cs4Roq7Ga/qxqzuvR0tUNVnaVOFd2deYvW88+g4ZjPA7
yMsb2/90/G1y9lObWl7Z249zZU9El9NLN76UfjsyNnMk++V5majDH0ROH7UwraipntqBw+KI
ZNuVh2/4CDXD5b2O2NJLiLKKMspHihpctZxWntgzrG8kb4hb08OAZXgPBE2wDUlSfscvb4QS
qwtxEeArW0zABeuRCMDkwCKlUEAlurcNHUwpDXQQtIWh8eAnswREqRPjB6EXwCKK6EhiJbp8
Xc9NmoWoBqowxXeyAkXK9zhysgreFGKHKEanDA7bXwaNJouA/zQbRqKIT1Eh2c5kYRDd9CLK
FnlbhhLlVxmlZj0JGvjeTnO1F2iVCZG1OhIIm2toJWLyfI1nphDVw132wXWaDug+260RYGGp
Zxg+eII6hajwptiDKYuLdJswYZ63bX+ekGB8mcNJ6rP8V9pySRM5Gqbu6ILcKNenomNu7nb0
ZaoQadyJkeKBeH2FOIYY3k2MthVVVGRJuS1QApQcTseISflYzcXWxVRsb2WfZtGveslrTPSE
Sl6Nln588aWmVPLhCP4qKbBB7HPrA+dgzoi79oGumxIxmJhVe81Cl/pdLep2HbMhSypKxs/R
8EFMueAeZ/EawocD2ybOXpTKcKeKlryRjlexJloNHIiV7rwXXi7uKh59kWV2733U3Aj7yN0P
I8wVE+rbu9p3CklWzWrT8BOWTmIXRG912tyLmhCZzBG3lAxqoVRNzPDFM9CdJD0vRFXTgMDH
NCqpfBj3TAoLBSEgfMvnfzxcPsVfRHZa5XmGqPJ7z+eFZPNVgHGUTpmrYCBPliFKbQUial7B
IhARCRhVRFkVj7aP7nGZE1gMpdZclthAMywcLq+mREzxdXZmDZeDNVR71beIR1PIUZdjSI80
b35zlch53lMJdhGDfSAaweLA04e5NvBUqA2pvAKNyz1xHgNAcVQnYOUVKy92yiGKUcI92DJG
BGIe/NQB/spN71IaNeQbwe8RpQPC5hgS9QgzM3GlW/9K3bP8QTGleyZOw755Gk7lmdItes/y
vew3un1zFANiqd58xsZTiDUG3K2dAJ7ksWQ6B0TzGspWeBuTWPtsFYMmK+jiohqtbPvli6Ut
4ns3BjbEukIGD4y8305fdbBNZutGFXyCZe4sMRDbd8ETz/j3H3YI7n9Pd/sYsGwXkUG8bi2y
zNDdmVafJ7se0/mcJIMhHtFCxaq09i0enjCuL6P4RZW92vLTI5MaffRiCvOFSCTVfizuxjQK
71MeUdjlVjIzl73bvXqe/+7OiF4JH0HZDi/BOfeP8/az1krjsGnTQ3vXY05/I4Lo2ulEqbHo
gjleeQrze7GjDFF2t/XpjhNYlHHrLWoQ6SNvC09Q0DtERSK832Fr9AfYxYUE2+jmu2P8jnqk
QkoyEQ2XJuP8u5AmRWTcyQ8kLFi97cFW4OB9DH2DWZqCRzEatjWOdvJRGHgQeIsxfcAW3fuW
j6hD8RHh6WH4iKfAG9a16FSwjrwMbxiklMdRymuxZy7Be4DwpviHkSQ9vALdfvg2ogI480p0
xSlE/HGMpEE/D+p+HXgEqyPZbJvoRzh7MMhBNK/lnOWCjw5l9Ozl3VebFYWHcsBIGHl2vqX6
mODlWUTkBxdJ4ftUBbKCeAV8XYYU4sd7r38aTizW6I41NniwU+eYZ6qmm2fuIG05kf7VAZXI
91/a+uOttV095m8Z1l4PIAqhcxpZe6+crhjNeCiRWNThcp5cLCUVdamd3+V31gld8j9/7cB/
tOF4dsqqlkd8XqRE/MW6tcWoN+pF19m600t7TZ0WYoIUlFdXr/TNZ4jOqH8neCgr9bRnZHnJ
F07PFCdyFS44SlWm8Ab3xEWo7MWqNKMXt5VY2YpEFahWYHHLfSwVP+vqKmDERJH4h5E2dLG3
LPV2xWYTpY8Jl7IjRlpujXSb0TTbU59bqy7cniBE85aptNu8zD0yl8KQ1zdcpV55u2Vdzxsp
EUqWLitHzN7YaZZ4vxo7l+DUvhgWFOSBJBUJTSP6K4WEB/3gPS+EO/zgCRiyMgj87aKb7wld
/R5RDtZtFGA4U1r5cthcWTlcZ9goEaxWSqnC+1ZAF309lDPA1ONWscfu8LasvAArnqU83mkH
0SogaPPi8ynlIamBbWHDyOw3fE1T/I/MnQPEP/CQhHnpPNpUfBt/jjz2UNZKS1qdl4D6TYv7
1o3ptHGN/H0dR5LmwP8vnCARntTmh9+yo3sWPbeyHN0l6BsZadNX6FkbyNfZJDyVoJB9JiyY
UlNRCl9oQw4qhGAjp13ONAWGzXoIKO0W9Gd1HgiPk3FLVlDSmQkeaNwTWfTy/ETq6XGjKPwk
f3AGTwtb5K6wtkO74Yzl0lPdU9+P2DncQhmg9yp6t4W/JIJti3/w4lUZaY82bo/UtzaxIERG
Mxm6cg26hloS2tZ2cQcinQWbTCvqegXdW8APFc//KPFD6xKxfmC3W+5HxQxGtpdDYZl+YLvm
2rEy6fo7rwNUetX9bZ5Hmt6ysLrYLTS+e+9c8cNKf0OwV3iiPisoPN8msHvLTyzN1bqcvHyn
E9t6le0xbJT3Dv3mit4m9JG4B1Hdr11s0+h1riQqvrCijAr2c2ijslQsvVfCC7S+Esko29Nd
gQ2SY1l9cNrDXDap60hdcHK1z5JtOShGaHLpXrjgsRR+Id9JZgYpTqvyKSJjuv7RF1WxQSMo
qSbgiGAgnKimdOCPIb1vv0NQIqI9EHeNSnnUJskqYLl5ckB4fUoApQnvvxe2SimjYoEjPzkf
sQzv09OE1vp4s7E4I5RIP0mTKkYllTHKy8uoeFmPBEwhpRhsFMnqyaOhQYCMBJHburS5NNkp
xVZgCV5fd6Qw2Sfox8h5fo1mF8vVy3NgjW5hD2FPtyRzfHzh+N0hyXq7Js8qZhBWozs60rmv
8MePSS/29yxQpM0WebEKQpKPWobvdOLCBvt4rtLu9I4hr5iwVBIUXBQC+ehwE6eggf15u+Xa
RC/4KgqnhI+7BRQoW78vzrxwNKlDSs02djRAbTfL33fMjUwed7JNc/+oJZE5soaUvZHZda5+
pdXPpiMKn1h6kor9A8XgFPE3s2rEhlO9051kn5AvjPVEjaXYiN8yKGHzv5kFg0KfRxJz2MH1
AG85Gq99X/xOR85ygdGSRgv/a8EdShqFQmeJ2zIGR48sZHxcL/p+wJReKRqq4Oh7PdL5ITP7
VGblaK42/h81t9Gh2x6FuATJNUSV56IcpR6Bh1t7C8meRzs6u9DJRQX1nkcjJnNi67H0p3l7
ndqQgbHTlbH6jXo2ieiFlLB6i84czN4mopCii1+2UqxBSbR1tV5P6gJeLTe52kXMNYJ1tUdM
d5dfdkT7ve6TFhM5mpbpz1tugUc1MztCjirYTBNWqZX1dWnS6KQP89RH9aUpDHQlphBJfM8X
eIUy+UaqoW+bPmGCpvB06zzc54r+GnigMYgtp1O9MyKEdvOZJsOXGyj6YDKGxRRk6V0aMuIt
FhJ5CwKxcl67NFXEhIvyhHC85EG0q4leUm5EtIlfY36YqQ4fQb10TS8+6zxLoTVwji91ao/B
zV6dYXzANd2H13R34X1fPCxTZgbxCiU15soEjhfeQG/RLjzk7Plj2pUwfWrAFOINer3uGILR
SefRhUkFXYU558h332fpKZwIG7rKuBNZYS6Tk6BBVWBTNOh1USUuQEGUO4WTinUu6e7N8lyw
3dNyyLdMub5H8KWTQH3AzfrAqHFewVC3NObV69dntsf9I3H0SWRefsvHqBWrThNFj2jeP9UQ
SE128u8e1joQY/Ezc8nbWbGPmCmTM5f2emDns/FPsJM/7a+R5WMlpd5yPFwYUijx2B9SEbva
bUut3zZ1z2nJb4heHbSvLfCZ6iYsOXrLOmuma+zbV2vYMoI/X+K6GDBnsjf44NG3w2xRUaNo
G9hce7yJxf1/VBkctM5R2zudi9xrUvDljpO+lQW+C4tbu6xLV9ttkjGVCqq0ASs+q5wuE3Dp
Jpsjb32/KqyhihpYXZfXnyM61AVsVdI2CbiL2EgRg0MWo007GnzE01xFioLDLdKbiPN31xRz
1Mx2NcSyErzV42QdjrgPIj/BPFruPI5n81qx96XNhI5tuRvRXm3rf2kArf6dxEy3BMw5e9ik
tFCb0eX+gJ1VIpaP3D9Av9rVWik88VMoa5lnbqD6Q7MuTCeNqrSQPYyce49s7Mnwg4eowWVP
Zw/zdz5gH+ieQaxc4vPLc5Y0yx6e3tM7QznVOjL9sw19d0CMPgFohnTEkNfRK3WyEXjTrq8F
NNaIuO/TV+Gml8E2H8/EOYqbb8DsarMWbd/CUrdPtDNz/1iuf1Il6krYEPnM4Azy6itYp20S
RSZoQDiQtwdbGwKj49qQy9QrYbMnyysPmtwTyJBUGPKAswtpvidrcHDjpkmyBqVStI/QJpTs
zzc+qeiCz7eNddN7IqxmggrKYszgL4D1S+3bZ6NKSmTvK/pHzI9qaTMrv22QuYIm56QFyg2x
LFaOSTA+amyTOl5MqLUrf1v0TxQKHQHtNvqPL57x5jdfan21jez7Uku0QXSjBYOyCj4okdy6
EbN2IimpSHouTsJhnsFcAYsx7JkHXfHhqesSSxnSQZWXrmAyMnXdHg33LjHXzhEkJJTiG9RN
XkfPBA/aSweNxXnpsi0DUJ0KDR8r52bPvba0cZTZalMVMyiGMw4+eSnGI70q/IKDSZmRyr4S
oveOesc36KN9q1H0dqBmNpNVO05e2pKZN4cYi+4bruiZJdvmDpfYmA6XgOH/igN6lo2oqYB7
ziLocCYTzmxy2Jo47SOJowb20xRUKY+oISB6WK8Kq/+ar2m+nOaAXpdHsFbh85WiHVuSCZUo
yRLVSuEaSomm/TdI6tSA8BQf3b9S3grxOoCCm88wVyh4z69MDUgrT1AI+UYgDUPWKNuglah1
6GkU9Zo7eVTfpQnzjZW+5Vez44uiRE2foKoYMFJXPPjVBvm6O7GmHlsCWdKnthxtjHK16xJ3
aEQ9eTJYSQkkNLn7dl9882DeJkQjC3OaGaKV8e1Djciopdt40ol20wSLFdE7W5++8YgiH5eL
PyFVfZvzFzf/UXjQzYNM0x+E+Zmsq9tmGtFJRSqPyQRm3mKlxfvJpU5CRlBXfKsb8A6zJ98N
r12RQJbtT5bera2ATly+GX8jaaY2Vp00dlE98Jn0woPKEqUNkQJdZIFpjX+wu9ChyPcBt3ES
co4fnsdfU788V2lTxBs1ysZrELPwwVOYoJzmc90i1nxihIbI2CPL4ReihUR4LZwiVJoLh0si
A8FjLxvFe1bSFk7FyFbNbfSnCsrzKfB6S2GKbe56XU6ulBpvul5OHo6nOUQhR0EVjC9nEWOI
qCpqAFhOXb8nnMwT+MiQgd5w8fWLRFRnBvHsvYxISrlUidJxPm6bcGZQDVFDc1KFL4INaGXw
g2g2cWD3Yhd68R2/WgJm9Z2AUHaigrKHQPMsIirLP6lNIBc7VsrTJKBCqBQF8wvrPmxyQbaL
qUf6I2pziDdfL+pAmC+0Hb5IuJoynrby9CArMFwpFgX2C4Dda0+yFL7cKaiw527K99HdVhN7
OvPzDR1qt79ONcV71C3s8121np5R1+n5qu6l8f5sIQ1H2/lGtpd1yHvR8i1O6Q7ymoT4w3pd
fynGzQr8Wg7bReuFrsWHGxwSqlbpFBKaSggWXaRoyaUn5QZY7w8aX/jYbbpnTa40+JynIbP5
ajT7+JjniI5kw91lJfULkRIige7TchJHFUfMRMjLSdmH7rS0i11caheaKRw6VJnW2NLA2j8o
MR+QsaN5VItN9gQ/03u7t5839vwFlkyMvWctgb8wZkzMIqBQ56CNR2NUWWTSlrvCjgcPxJh+
DGtQwBLTNV+ILFR57/CdyD0yCyZ7hX4py7nyeEKlyl5HRNT83sIQKTfsWK25bS4PvvABv9YA
+kgnsJlBBn0IplFQy0AfqelFjHUhB4TTMTTRvrChFtjYLG9KKbW5nEZvHxD0mMwRbddmjH2C
neVNeSVZYsXTxK9rrlE1IEjkUfF/y68uuhCrzJsqlNEk6DHF10uW+qmsTnb3jIB6goDKPOUU
M+5RmOlBg/4gXqVoVJfoZMu5zlKGVuKAaZTbQL+f7b59WriI5geBmsvuC3kdgtKT57X2x0Yr
RjIf+ur+bJBgHbJ2h2/k5TYS9XamLL0hR7sdJaL/x/H8prz+7VtAUQidWKlz9srjGlGWWurQ
lmc2VtMO5+pVQqMwul/eYD/Uvasj4PST6OAVWW2pGKegq3uZrc2ehk1NV+OWpviGvmh4sMRe
U3/hf661QWERIz3uOmMm/MbN/UC4dazx1R7n3ckbNlE1J03ptqlf0wssDEKPxt5Oy1KceXd3
mlK45GCGiSRko1W2zVkkZxbkRe6tusC6lOCdSpwMTdpSXdgZsETrwreSiX0EAiLGKL0Kq7Iv
3aUk8i1yb1SJ40pr7g6Dg59guxRK33+x704Pq6xVjLFAKYksKOTXphZemefNMMFjx3vJTi62
uVqUKFZ/2KopxZc5z5t+4h2/NmUcsZAgAHaQto7xl/YE8XxQ6BIoVE0wI7zhL+VLPWMk3vEK
m4o1Ys5SzAi7BD64muBhC30+XUJ9TLM+vlRi4MC+1HrFVeyo08Vk1w/yhilCUe3N79/mJf8I
FnbPCi4H3xFlSSwF3/Lr1C2LvCcqYXN0OL/hUC5r/0TEpKkobuyWs8+hkRrUjTLbQHvPQl3P
2oLDOreUO40vdhrrGxptofyboP66YAvxyd3dSZlVUrnuAYl0Ix1Tn8fi+1uauuPrHrRbTZ8V
02kpilX9/gZ7FogU5TgundE66n7P4KCN2eOcJBB9LSd+gt2t0aUGPmXTy5X9sg9sy9W5oBJS
L/0keqRI5LzsJJku32TosD3IfdRGvsCUHlCZ6iynpDGFzKiLGPyRkUuIDz5Z4zJ6rfGBf/fz
Dz9GflAixJNt8nZGuHSXHww2svH0tWqasK73VEINHIgJ2FJdkYzc19Oxcri3vJR4WB7fGFIX
UpTKaxE7iI2x/dgm3Be2SujTc0Ur8/Y1nkIs3K6pGbHpc+oM+QIRY5eem34j2kfvrOKVp9fL
YikLdwYs+xa/3Umgz1lp5xsspD9O7y3S118oHzxpx4wb/iF61z/V273ZUgdfE1EhbdqlJH+r
BXaXfuoVwoVTjbNb3BV7WLIVEe+2t3gmlj+6YZs6qqjrIerJAv8HaFHFJG5Rv33ZOP2MhHCL
XEqw6c5/UkdMdZN7RfLlq5XWLJt1t57WKbRhJB0hnb2iEpuY3jua/eZrnUGzcHLTt7ij3z++
2yLXy4pa0NcnwWh/LcI/qQG3FVXS0v0iNc5h8Ayv+An8uXrnAB0n3bDgo4mrDkIK18evCV37
BNOv+1rnktrbXoqN2nM3pWWfKddZwzX21x1atrV3HZollnRRLH2/GC+69WzUj6tRht/XwgPu
Iuc13n+nHKrcC35v0qkb1EFsdf4u2Dl8odJNHFM18rp9gxA20pshLM2Sr5hcQl/e2K5L+AQz
YU7+HMn0fB7KerAcI7jRCxRlie/Jazt5M7DRLLhw72D6F+FgBrUUjburYXiaFTL8SiNnwqYp
3CI5+z629hSIZJK6hCe0jyHnKDoJyLnEKT1XxUE97dokxIq+w857C2nYFdN2MdiKQco7gbmM
MbiSYhkjpglH1rkjVpfUbFCVcKq5kb3rVDMTHqK0fkmyaVw6R/FsUAarOM6XSWbhtbOqpVai
PoSLfqXk8Wzm/aD85ewtP8bH5u+8xH9dyyw57UsUVaj3AFp6VPj7kd52xowsitmrwZx5G1dy
Xb97NuWQ9MT5NeRj8geNVIcGvOtS3mj8t7Z5wIAZSwamQ4YjS8pN/sk+uvu7+avkIqL1/7sO
949EDOfx4E+R+I480Lshe320pHaj6Yjn6rC4vPPWJdcDH8jyN82CjuOTlm3vBSpq8Y54mbhe
h/55R0bnYGiSp2GG0Jwvw7P2YUPrOeelC9Pg79FPGY04v+0/VFTyev+70Gpl6w1bOdGj66Ju
of4skUzdDEzorJ7Ra5u3szHtK4Uqt4tWX6hYLv0MSih0M9PKwBYxmwL/xuXzBJWWYCHWM2mv
a6GvGvLYWdsMNemHWH2qT4d71weCQnfH+QcQ6+c+wd7esp5IfPwJ9sZBkzkjgba86s0TP1X/
OKMqM9th/NuAZOU8itt6u/HGIU0zJFvWiT/tE4zHIPT9EMr5E+yL1tCF8DxRNabvJ9g/3WtX
XUoea505O4BUEy9tHNvRyMM2wZG1QkP8DIcsTKsMvwu2s9mIdQh6PRL6Ua73dLAs69niyJzl
+vsgXQG5nokZmyjP9cGv46ddr5p/TSzQ4WVjLOZntXQyPsE6fgJ/DHb2hMWKNmvecCHVBmO8
fK7b5s3XJyxX1JvNJtXXdW6Ohq513BiMb2+wWRxwVbEKPaTcuThwL6i41pC+Lb4H/NahtjbW
ZwW/zbCCt25Q5Pl6+t5rjrWLbhd03yXJSZzhvf7mYolXuRnvNt0fBOVWbzh+EPvz5ZM/UoG/
y/43coCva8//RrT+xulvDvzNgb858DcH/ubA3xz4mwN/c+BvDvzNgf/lHOD59HITQygZIvSi
6EKfn6dK5ZxzEhxCdf7fpVeFHdzsH8KBossDLqGDixO37Ndzzo0/+fgP6VV3WMEugmSi52GS
4LeLF8E3lB7VGyQq5SQl3fIHKVXFLDk1fEES0oswDKh/GSQk9eOkNj0P/rVHkpOc1A+c+XBq
SIKEnwSQ8tSDm1b10+gWK1ggJ+mp5h/0KQnanQc1zwN4fpz2J0AtfQABSv3qDXqDkp9C35Kw
wzBj8AmlRrX55dsIJgeDoCrDVH4pUQT/96n0u3MSgAVBNQHJVKFksxAsMoB6GfRwEZz7An6Q
wdsL4AlB+xK8j4NvIUnoXJlzfhZcK4BD5V93VDlnRrAgDmzzz+C5/oKxPyfZq98vFECQFcFh
w6n/OU8lYVYc+j0Abj4ACx/APS4mRqAtxElJmBtHVhc4koOkFciBovcL3gRQcg7wj8sreVAf
ouYcKD3PoegUgLwpH9+/aAklwPUBmEP4unKg+AIObZZCsL042PoBXCD9kQT4nQNlXjDoHiSr
80BLoCS3F0E76BoqdQNvCMvzv9SC7ntz6kF4/lEdj19ox4BkuucAvZJAXlAy3POgP246XC4s
Mgc3KGUvpEFcDkD8gqgnAKwgXSWAVr6cnrmycQPXECSu3ktyIEA0c2UMaR6kk5CuuIOyz2mH
+oa01et35RD/udz4vDaElR8H989LoXqunNq/yuy3vXzD6Xuz/03+crGDUuqe4/ATagPRBV1D
soD46PcLlVAbCPtNGJ/3TwSlm/YLScsPvLm89AVyg6zcD0D9rVy5OJ8H93/lMWQPkLbiwTuQ
068N7CtQBpVDsvIFkvq83z+W37/rJlTCpQrSqs95BHkDCFeubkKpoyH5QnRC9v1n7aDalhwO
cbUC0lnIh0GJlTfbGsEMOL4tkNPz+V/0Xw1QBaVbNoRt2vlJ0CPXV0GUeQMIruC+L/iEbOAc
4MSmznEt2A7U5lqcCacdVy5ce4V06M9bmgL4XK8FaTskWS62kFwgyrkeFqINwhDyVZDvkwSY
Q63MfpEUCbSF9JoEoP0VFHmY+r/a64M+IE5/blNcjYLoh3pVgnE9YPEv/gTiJHSPa+2SgBdc
H7DpJ/69jSWg6jyoRwSchzRIEkDwB9cXga+Cav/Ku6840H7L3c1+SOCeL4CxyR2ITj/QGrqG
7OgSOCA7hOQD8fs86IU7tkBaDvWzyemvOdhAKbshTwbZE9QeagfVegEORc44A/HzMDhXA2+I
sw/AKATx/LftIauEeAJ5GUh2/7dwIP/2+Sj9X8Plz0d5rteAvKPHv+jS4NABUaXKSSz+K01W
HEv5dUTnchDyGJv8toKdBH/T/xWwkN/K7K9aQrV/1VwokTk05nqB8R3ipRWAD0np9/1BraA0
8NxyV/ANaT63hMTBCWptycGa6+M28eTqBfkX7VD8RcYQZwnggOi5BPrjYrWJzeZY/WvE85+g
eQPYJKDJ3KgCGvMkQcRyEkQzkDeFvKIboM8fWCJXotBoCOkGRDU3MTxXHyErJAP5+IIk1v8d
aiDoPgDSpmwgWjZ1+6858uV/5AiXw/9VfnBh/RE+n9s0N67j2okf8AG/atkml7mjtR/gFxQX
fU7PPwCdkOQgDfi1HXR+niNHyNbdAK+hER7iB9TX5+0NfnePy3lDTk9QNAhJAPJEkFy4nhAa
LXzB9SY0yEdAURykdRggXag3aLyC/Bg0HkPRLOSboPquHN4agzOu196kD/L+kA5APUE4QjCh
KBXSJK6/MgMS5OoOdIYBft0AvKF6pqAlFx4etITGfy5UDOgD4heXit/zgNsS0kAIN69fYEOe
HrIB7jgBReRcvePGBly4kA5DvvQch4//AG2hWQREJRQReXBa2ID70DnXx0BjDgQZiiMh/v+R
HE9xyiGL4daBRoTfSuxXjTkFZiwYUPO3Gg6VqgCvBWEM8Q7qEeLFpr81B5hCusKVA1RLD9AO
jdOb1ge1IP0yWkHtuXEtpC0Y4KE2ZwLcyL8YeDoIxleAIsjaoLpQzcuAam5s8vu7EMe/Bn0a
c+ppcPyc0r+whSTNjUo2+70IkwXYQvMESCs2ozpuNAHNcgIBttAdblRxlkPt5iwJwuQroCMm
HM+KAVd/FfeYw6zBSAbhCHlxUw6O0IznOBjb1AFXFcGZCjjX4PhYKMn7Z4cQNIP04YyuRMA3
RZjzb2ofg3kCrrp/3uL354hfPd9ncKFa/Jc4VEJW4Q9o/d3d/5/X27mxKBRNQHz/BnhlPEdf
/gQnXqi+1/84hjwciDthvH8y5/9PxTzQTTgMJvy7SkuctY7fFf7B5cx/sd4fNP0fKpIHcHb/
N2Algrp64EgAB3cDMxb7Lac9dw0HWsfxA9d/IsM/LeeA+OUDavtXr11/WgH1x3e2/2nXoDu+
40D5IOME57zc898TwIU6DrQEyBv2fwCfJ/o6
    SensorDataFile = <blob elided: 365386 chars, md5=6bdf4b68>
    Type Image = RLX_057930.jpg
    URL = http://relux.com
    VarID = var1
    Voltage = 0 V
    Weight = 0.00 kg
    Width = 100 mm  [stored 0.328084 ft]

note: [stored X ft] marks values corroborated as IEEE doubles in the binary element streams (Revit-internal decimal feet)

## geometry (parser evidence)
native form markers: Blend x2, Sweep x22
no freeform markers — native parametric forms only
